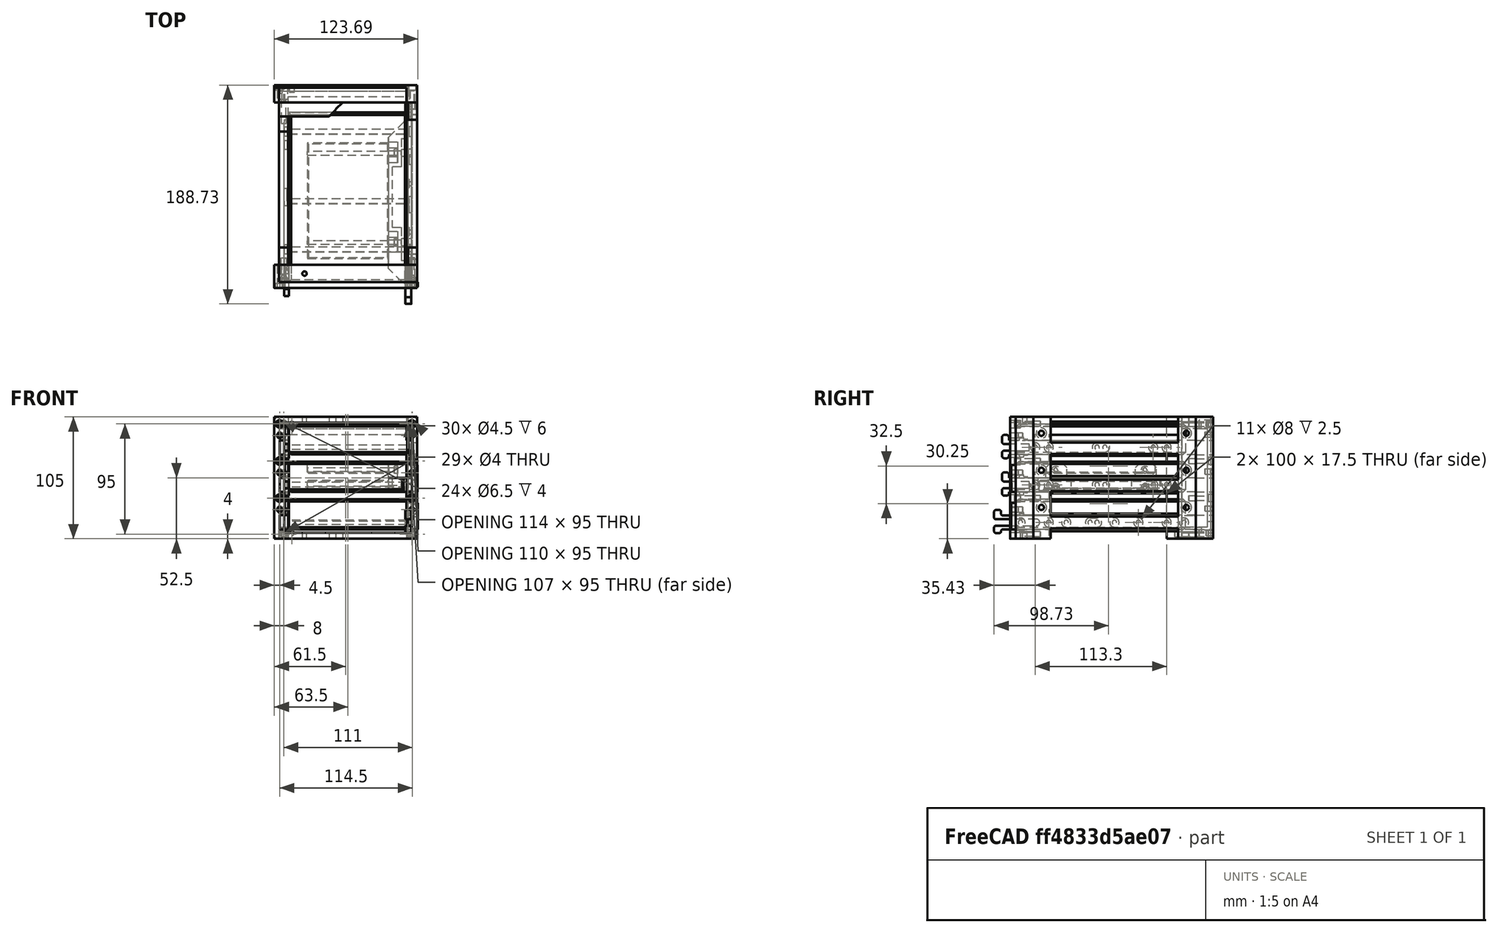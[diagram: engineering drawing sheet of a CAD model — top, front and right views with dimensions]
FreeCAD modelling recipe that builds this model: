
FCSTD DOCUMENT  (FreeCAD 1.0R39109 (Git))
Label: HDDEnclosure
License: All rights reserved
LicenseURL: http://en.wikipedia.org/wiki/All_rights_reserved
objects: Sketcher::SketchObject×66, PartDesign::Pocket×42, PartDesign::Pad×25, PartDesign::Body×19, PartDesign::Fillet×16, PartDesign::Chamfer×11, PartDesign::Hole×10, App::DocumentObjectGroup×3, Part::Mirroring×2, Mesh::Feature×1
note: 465 computed .brp shape members not serialized (recipe doc carries the construction recipe); baked Part::Feature solids carry a one-line shape summary decoded from their .brp

FEATURE [Mesh::Feature] HDD__Sled_Mk3
FEATURE [Sketcher::SketchObject] Sketch
  ArcFitTolerance = 1e-06
  AttachmentSupport = -> [XZ_Plane]
  FullyConstrained = false
  MakeInternals = false
  MapMode = 5
  Placement = pos=(0,0,0) rot=(1,0,0;1.5708rad)
  sketch-geometry (28):
    g0: LineSegment StartX=4 StartY=0 StartZ=0 EndX=-144.5 EndY=0 EndZ=0
    g1: LineSegment StartX=-144.5 StartY=0 StartZ=0 EndX=-144.5 EndY=-1.6 EndZ=0
    g2: LineSegment StartX=-144.5 StartY=-1.6 StartZ=0 EndX=-147.5 EndY=-1.6 EndZ=0
    g3: LineSegment StartX=-147.5 StartY=-1.6 StartZ=0 EndX=-147.5 EndY=0 EndZ=0
    g4: LineSegment StartX=-147.5 StartY=0 StartZ=0 EndX=-163.728 EndY=0 EndZ=0
    g5: LineSegment StartX=-163.728 StartY=0 StartZ=0 EndX=-163.728 EndY=-3.09041 EndZ=0
    g6: LineSegment StartX=-163.728 StartY=-3.09041 StartZ=0 EndX=-169.728 EndY=-3.09041 EndZ=0
    g7: LineSegment StartX=-169.728 StartY=-3.09041 StartZ=0 EndX=-169.728 EndY=3.2 EndZ=0
    g8: LineSegment StartX=-169.728 StartY=3.2 StartZ=0 EndX=-130.5 EndY=3.2 EndZ=0
    g9: LineSegment StartX=-130.5 StartY=3.2 StartZ=0 EndX=-130.5 EndY=8.8 EndZ=0
    g10: LineSegment StartX=-130.5 StartY=8.8 StartZ=0 EndX=-169.728 EndY=8.8 EndZ=0
    g11: LineSegment StartX=-169.728 StartY=8.8 StartZ=0 EndX=-169.728 EndY=16.6996 EndZ=0
    g12: LineSegment StartX=-169.728 StartY=16.6996 StartZ=0 EndX=-163.728 EndY=16.6996 EndZ=0
    g13: LineSegment StartX=-163.728 StartY=16.6996 StartZ=0 EndX=-163.728 EndY=12 EndZ=0
    g14: LineSegment StartX=-163.728 StartY=12 StartZ=0 EndX=-147.5 EndY=12 EndZ=0
    g15: LineSegment StartX=-147.5 StartY=12 StartZ=0 EndX=-147.5 EndY=13.6 EndZ=0
    g16: LineSegment StartX=-147.5 StartY=13.6 StartZ=0 EndX=-144.5 EndY=13.6 EndZ=0
    g17: LineSegment StartX=-144.5 StartY=13.6 StartZ=0 EndX=-144.5 EndY=12 EndZ=0
    g18: LineSegment StartX=-144.5 StartY=12 StartZ=0 EndX=4 EndY=12 EndZ=0
    g19: LineSegment StartX=4 StartY=12 StartZ=0 EndX=4 EndY=0 EndZ=0
    g20: LineSegment [constr] StartX=-177.942 StartY=12 StartZ=0 EndX=14.5003 EndY=12 EndZ=0
    g21: LineSegment [constr] StartX=-144.5 StartY=27.4193 StartZ=0 EndX=-144.5 EndY=-18.7719 EndZ=0
    g22: LineSegment [constr] StartX=-163.728 StartY=22.481 StartZ=0 EndX=-163.728 EndY=-16.4674 EndZ=0
    g23: LineSegment [constr] StartX=-169.728 StartY=19.6726 StartZ=0 EndX=-169.728 EndY=-22.0842 EndZ=0
    g24: Circle CenterX=-66 CenterY=6 CenterZ=0 NormalX=0 NormalY=0 NormalZ=1 AngleXU=0 Radius=1.9
    g25: Circle CenterX=-6 CenterY=6 CenterZ=0 NormalX=0 NormalY=0 NormalZ=1 AngleXU=0 Radius=1.9
    g26: LineSegment [constr] StartX=-174.191 StartY=6 StartZ=0 EndX=-2.85094 EndY=6 EndZ=0
    g27: Circle CenterX=-107.6 CenterY=6 CenterZ=0 NormalX=0 NormalY=0 NormalZ=1 AngleXU=0 Radius=1.9
  constraints (76):
    c: PointOnObject(g0,g-1)
    c: Coincident(g0,g1)
    c: Coincident(g1,g2)
    c: Coincident(g2,g3)
    c: PointOnObject(g3,g-1)
    c: Coincident(g3,g4)
    c: Horizontal(g4)
    c: Coincident(g4,g5)
    c: Coincident(g5,g6)
    c: Coincident(g6,g7)
    c: Coincident(g7,g8)
    c: Horizontal(g8)
    c: Coincident(g8,g9)
    c: Coincident(g9,g10)
    c: Horizontal(g10)
    c: Coincident(g10,g11)
    c: Coincident(g11,g12)
    c: Coincident(g12,g13)
    c: Coincident(g13,g14)
    c: Horizontal(g14)
    c: Coincident(g14,g15)
    c: Coincident(g15,g16)
    c: Horizontal(g16)
    c: Coincident(g16,g17)
    c: Coincident(g17,g18)
    c: Horizontal(g18)
    c: Coincident(g18,g19)
    c: Coincident(g19,g0)
    c: Vertical(g7)
    c: Vertical(g11)
    c: Horizontal(g12)
    c: Horizontal(g6)
    c: Horizontal(g20)
    c: PointOnObject(g17,g20)
    c: PointOnObject(g14,g20)
    c: DistanceY(g0,g20) = 12
    c: Vertical(g15)
    c: Vertical(g17)
    c: Vertical(g1)
    c: Vertical(g3)
    c: Horizontal(g2)
    c: Vertical(g21)
    c: PointOnObject(g0,g21)
    c: PointOnObject(g17,g21)
    c: DistanceX(g16,g16) = 3
    c: DistanceY(g15,g15) = 1.6
    c: DistanceX(g2,g2) = 3
    c: DistanceY(g3,g3) = 1.6
    c: Vertical(g13)
    c: Vertical(g5)
    c: Vertical(g22)
    c: Vertical(g23)
    c: PointOnObject(g7,g23)
    c: PointOnObject(g10,g23)
    c: PointOnObject(g13,g22)
    c: PointOnObject(g4,g22)
    c: DistanceX(g12,g12) = 6
    c: Vertical(g9)
    c: Distance(g8,g-1) = 3.2
    c: Distance(g9,g20) = 3.2
    c: Diameter(g24) = 3.8
    c: Diameter(g25) = 3.8
    c: Horizontal(g26)
    c: PointOnObject(g24,g26)
    c: PointOnObject(g25,g26)
    c: DistanceY(g0,g26) = 6
    c: DistanceX(g24,g25) = 60
    c: PointOnObject(g27,g26)
    c: Diameter(g27) = 3.8
    c: DistanceX(g27,g25) = 101.6
    c: DistanceX(g25,g0) = 10
    c: Horizontal(g0)
    c: Vertical(g19)
    c: Distance(g-1,g0) = 4
    c: DistanceX(g16,g9) = 14
    c: DistanceX(g9,g18) = 134.5
FEATURE [PartDesign::Pad] Pad
  Direction = (0,-1,2e-16)
  Length = 5
  Length2 = 6
  Placement = pos=(0,0,0) rot=(1,0,0;1.5708rad)
  Profile = -> Sketch
  ReferenceAxis = -> Sketch [N_Axis]
  Suppressed = false
  Type = 0
FEATURE [Sketcher::SketchObject] Sketch001
  ArcFitTolerance = 1e-06
  AttachmentSupport = -> [Pad]
  FullyConstrained = false
  MakeInternals = false
  MapMode = 5
  Placement = pos=(0,1.4e-15,0) rot=(-1,0,0;1.5708rad)
  sketch-geometry (4):
    g0: LineSegment [constr] StartX=-161.489 StartY=-6 StartZ=0 EndX=29.2517 EndY=-6 EndZ=0
    g1: Circle CenterX=-107.6 CenterY=-6 CenterZ=0 NormalX=0 NormalY=0 NormalZ=1 AngleXU=0 Radius=4
    g2: Circle CenterX=-66 CenterY=-6 CenterZ=0 NormalX=0 NormalY=0 NormalZ=1 AngleXU=0 Radius=4
    g3: Circle CenterX=-6 CenterY=-6 CenterZ=0 NormalX=0 NormalY=0 NormalZ=1 AngleXU=0 Radius=4
  constraints (11):
    c: Horizontal(g0)
    c: Distance(g-1,g0) = 6
    c: PointOnObject(g1,g0)
    c: PointOnObject(g2,g0)
    c: PointOnObject(g3,g0)
    c: DistanceX(g3,g-1) = 6
    c: DistanceX(g2,g3) = 60
    c: DistanceX(g1,g3) = 101.6
    c: Diameter(g1) = 8
    c: Equal(g2,g1)
    c: Equal(g3,g1)
FEATURE [PartDesign::Pocket] Pocket
  BaseFeature = -> Pad
  Direction = (0,-1,-2e-16)
  Length = 3
  Length2 = 5
  Placement = pos=(0,0,0) rot=(1,0,0;1.5708rad)
  Profile = -> Sketch001
  ReferenceAxis = -> Sketch001 [N_Axis]
  Suppressed = false
  Type = 0
FEATURE [PartDesign::Fillet] Fillet
  Base = -> Pocket [Edge5,Edge1]
  BaseFeature = -> Pocket
  Placement = pos=(0,0,0) rot=(1,0,0;1.5708rad)
  Radius = 2
  SupportTransform = false
  Suppressed = false
  UseAllEdges = false
FEATURE [PartDesign::Fillet] Fillet001
  Base = -> Fillet [Edge65,Edge63,Edge61,Edge59,Edge31,Edge58,Edge56,Edge3]
  BaseFeature = -> Fillet
  Placement = pos=(0,0,0) rot=(1,0,0;1.5708rad)
  Radius = 0.75
  SupportTransform = false
  Suppressed = false
  UseAllEdges = false
FEATURE [PartDesign::Fillet] Fillet002
  Base = -> Fillet001 [Edge83,Edge85,Edge87,Edge89,Edge96,Edge94,Edge92,Edge95]
  BaseFeature = -> Fillet001
  Placement = pos=(0,0,0) rot=(1,0,0;1.5708rad)
  Radius = 1.49
  SupportTransform = false
  Suppressed = false
  UseAllEdges = false
FEATURE [Sketcher::SketchObject] Sketch002
  ArcFitTolerance = 1e-06
  AttachmentSupport = -> [XZ_Plane001]
  FullyConstrained = false
  MakeInternals = false
  MapMode = 5
  Placement = pos=(0,0,0) rot=(1,0,0;1.5708rad)
  sketch-geometry (73):
    g0: LineSegment [constr] StartX=0 StartY=0 StartZ=0 EndX=123 EndY=0 EndZ=0
    g1: LineSegment StartX=123 StartY=0 StartZ=0 EndX=123 EndY=105 EndZ=0
    g2: LineSegment StartX=123 StartY=105 StartZ=0 EndX=0 EndY=105 EndZ=0
    g3: LineSegment StartX=9 StartY=5 StartZ=0 EndX=114 EndY=5 EndZ=0
    g4: LineSegment StartX=114 StartY=100 StartZ=0 EndX=9 EndY=100 EndZ=0
    g5: LineSegment [constr] StartX=190.257 StartY=65.8 StartZ=0 EndX=190.257 EndY=40.4 EndZ=0
    g6: LineSegment [constr] StartX=190.257 StartY=40.4 StartZ=0 EndX=291.857 EndY=40.4 EndZ=0
    g7: LineSegment [constr] StartX=291.857 StartY=40.4 StartZ=0 EndX=291.857 EndY=65.8 EndZ=0
    g8: LineSegment [constr] StartX=291.857 StartY=65.8 StartZ=0 EndX=190.257 EndY=65.8 EndZ=0
    g9: LineSegment [constr] StartX=184.257 StartY=52.4 StartZ=0 EndX=184.257 EndY=40.4 EndZ=0
    g10: LineSegment [constr] StartX=184.257 StartY=40.4 StartZ=0 EndX=190.257 EndY=40.4 EndZ=0
    g11: LineSegment [constr] StartX=190.257 StartY=40.4 StartZ=0 EndX=190.257 EndY=52.4 EndZ=0
    g12: LineSegment [constr] StartX=190.257 StartY=52.4 StartZ=0 EndX=184.257 EndY=52.4 EndZ=0
    g13: LineSegment [constr] StartX=291.857 StartY=52.4 StartZ=0 EndX=291.857 EndY=40.4 EndZ=0
    g14: LineSegment [constr] StartX=291.857 StartY=40.4 StartZ=0 EndX=297.857 EndY=40.4 EndZ=0
    g15: LineSegment [constr] StartX=297.857 StartY=40.4 StartZ=0 EndX=297.857 EndY=52.4 EndZ=0
    g16: LineSegment [constr] StartX=297.857 StartY=52.4 StartZ=0 EndX=291.857 EndY=52.4 EndZ=0
    g17: LineSegment [constr] StartX=163.474 StartY=98.2 StartZ=0 EndX=163.474 EndY=72.8 EndZ=0
    g18: LineSegment [constr] StartX=163.474 StartY=72.8 StartZ=0 EndX=265.074 EndY=72.8 EndZ=0
    g19: LineSegment [constr] StartX=265.074 StartY=72.8 StartZ=0 EndX=265.074 EndY=98.2 EndZ=0
    g20: LineSegment [constr] StartX=265.074 StartY=98.2 StartZ=0 EndX=163.474 EndY=98.2 EndZ=0
    g21: LineSegment [constr] StartX=157.474 StartY=84.8 StartZ=0 EndX=157.474 EndY=72.8 EndZ=0
    g22: LineSegment [constr] StartX=157.474 StartY=72.8 StartZ=0 EndX=163.474 EndY=72.8 EndZ=0
    g23: LineSegment [constr] StartX=163.474 StartY=72.8 StartZ=0 EndX=163.474 EndY=84.8 EndZ=0
    g24: LineSegment [constr] StartX=163.474 StartY=84.8 StartZ=0 EndX=157.474 EndY=84.8 EndZ=0
    g25: LineSegment [constr] StartX=265.074 StartY=84.8 StartZ=0 EndX=265.074 EndY=72.8 EndZ=0
    g26: LineSegment [constr] StartX=265.074 StartY=72.8 StartZ=0 EndX=271.074 EndY=72.8 EndZ=0
    g27: LineSegment [constr] StartX=271.074 StartY=72.8 StartZ=0 EndX=271.074 EndY=84.8 EndZ=0
    g28: LineSegment [constr] StartX=271.074 StartY=84.8 StartZ=0 EndX=265.074 EndY=84.8 EndZ=0
    g29: LineSegment [constr] StartX=208.539 StartY=33.4 StartZ=0 EndX=208.539 EndY=8 EndZ=0
    g30: LineSegment [constr] StartX=208.539 StartY=8 StartZ=0 EndX=310.139 EndY=8 EndZ=0
    g31: LineSegment [constr] StartX=310.139 StartY=8 StartZ=0 EndX=310.139 EndY=33.4 EndZ=0
    g32: LineSegment [constr] StartX=310.139 StartY=33.4 StartZ=0 EndX=208.539 EndY=33.4 EndZ=0
    g33: LineSegment [constr] StartX=202.539 StartY=20 StartZ=0 EndX=202.539 EndY=8 EndZ=0
    g34: LineSegment [constr] StartX=202.539 StartY=8 StartZ=0 EndX=208.539 EndY=8 EndZ=0
    g35: LineSegment [constr] StartX=208.539 StartY=8 StartZ=0 EndX=208.539 EndY=20 EndZ=0
    g36: LineSegment [constr] StartX=208.539 StartY=20 StartZ=0 EndX=202.539 EndY=20 EndZ=0
    g37: LineSegment [constr] StartX=310.139 StartY=20 StartZ=0 EndX=310.139 EndY=8 EndZ=0
    g38: LineSegment [constr] StartX=310.139 StartY=8 StartZ=0 EndX=316.139 EndY=8 EndZ=0
    g39: LineSegment [constr] StartX=316.139 StartY=8 StartZ=0 EndX=316.139 EndY=20 EndZ=0
    g40: LineSegment [constr] StartX=316.139 StartY=20 StartZ=0 EndX=310.139 EndY=20 EndZ=0
    g41: LineSegment StartX=0 StartY=0 StartZ=0 EndX=123 EndY=0 EndZ=0
    g42: LineSegment [constr] StartX=9 StartY=177.265 StartZ=0 EndX=9 EndY=-72.0652 EndZ=0
    g43: LineSegment [constr] StartX=114 StartY=141.11 StartZ=0 EndX=114 EndY=26.7674 EndZ=0
    g44: LineSegment StartX=9 StartY=100 StartZ=0 EndX=9 EndY=84.9 EndZ=0
    g45: LineSegment StartX=9 StartY=84.9 StartZ=0 EndX=4.5 EndY=84.9 EndZ=0
    g46: LineSegment StartX=4.5 StartY=84.9 StartZ=0 EndX=4.5 EndY=72.6 EndZ=0
    g47: LineSegment StartX=4.5 StartY=72.6 StartZ=0 EndX=9 EndY=72.6 EndZ=0
    g48: LineSegment StartX=9 StartY=72.6 StartZ=0 EndX=9 EndY=52.6 EndZ=0
    g49: LineSegment StartX=9 StartY=52.6 StartZ=0 EndX=4.5 EndY=52.6 EndZ=0
    g50: LineSegment StartX=4.5 StartY=52.6 StartZ=0 EndX=4.5 EndY=40.3 EndZ=0
    g51: LineSegment StartX=4.5 StartY=40.3 StartZ=0 EndX=9 EndY=40.3 EndZ=0
    g52: LineSegment StartX=9 StartY=40.3 StartZ=0 EndX=9 EndY=20.3 EndZ=0
    g53: LineSegment StartX=9 StartY=20.3 StartZ=0 EndX=4.5 EndY=20.3 EndZ=0
    g54: LineSegment StartX=4.5 StartY=20.3 StartZ=0 EndX=4.5 EndY=8 EndZ=0
    g55: LineSegment StartX=4.5 StartY=8 StartZ=0 EndX=9 EndY=8 EndZ=0
    g56: LineSegment StartX=9 StartY=8 StartZ=0 EndX=9 EndY=5 EndZ=0
    g57: LineSegment [constr] StartX=4.5 StartY=110.102 StartZ=0 EndX=4.5 EndY=-9.82312 EndZ=0
    g58: LineSegment StartX=114 StartY=100 StartZ=0 EndX=114 EndY=84.9 EndZ=0
    g59: LineSegment StartX=114 StartY=84.9 StartZ=0 EndX=118.5 EndY=84.9 EndZ=0
    g60: LineSegment StartX=118.5 StartY=84.9 StartZ=0 EndX=118.5 EndY=72.6 EndZ=0
    g61: LineSegment StartX=118.5 StartY=72.6 StartZ=0 EndX=114 EndY=72.6 EndZ=0
    g62: LineSegment StartX=114 StartY=72.6 StartZ=0 EndX=114 EndY=52.6 EndZ=0
    g63: LineSegment StartX=114 StartY=52.6 StartZ=0 EndX=118.5 EndY=52.6 EndZ=0
    g64: LineSegment StartX=118.5 StartY=52.6 StartZ=0 EndX=118.5 EndY=40.3 EndZ=0
    g65: LineSegment StartX=118.5 StartY=40.3 StartZ=0 EndX=114 EndY=40.3 EndZ=0
    g66: LineSegment StartX=114 StartY=40.3 StartZ=0 EndX=114 EndY=20.3 EndZ=0
    g67: LineSegment StartX=114 StartY=20.3 StartZ=0 EndX=118.5 EndY=20.3 EndZ=0
    g68: LineSegment StartX=118.5 StartY=20.3 StartZ=0 EndX=118.5 EndY=8 EndZ=0
    g69: LineSegment StartX=118.5 StartY=8 StartZ=0 EndX=114 EndY=8 EndZ=0
    g70: LineSegment StartX=114 StartY=8 StartZ=0 EndX=114 EndY=5 EndZ=0
    g71: LineSegment [constr] StartX=118.5 StartY=109.281 StartZ=0 EndX=118.5 EndY=-16.6316 EndZ=0
    g72: LineSegment StartX=0 StartY=105 StartZ=0 EndX=0 EndY=0 EndZ=0
  constraints (212):
    c: Coincident(g-1,g0)
    c: Horizontal(g0)
    c: Coincident(g0,g1)
    c: Vertical(g1)
    c: Coincident(g1,g2)
    c: PointOnObject(g2,g-2)
    c: Horizontal(g2)
    c: Horizontal(g3)
    c: Horizontal(g4)
    c: Coincident(g5,g6)
    c: Coincident(g6,g7)
    c: Coincident(g7,g8)
    c: Coincident(g8,g5)
    c: Vertical(g5)
    c: Vertical(g7)
    c: Horizontal(g6)
    c: Horizontal(g8)
    c: DistanceX(g8,g8) = 101.6
    c: DistanceY(g7,g7) = 25.4
    c: Coincident(g9,g10)
    c: Coincident(g10,g11)
    c: Coincident(g11,g12)
    c: Coincident(g12,g9)
    c: Vertical(g9)
    c: Vertical(g11)
    c: Horizontal(g10)
    c: Horizontal(g12)
    c: DistanceX(g12,g12) = 6
    c: DistanceY(g11,g11) = 12
    c: PointOnObject(g11,g5)
    c: Coincident(g13,g14)
    c: Coincident(g14,g15)
    c: Coincident(g15,g16)
    c: Coincident(g16,g13)
    c: Vertical(g13)
    c: Vertical(g15)
    c: Horizontal(g14)
    c: Horizontal(g16)
    c: DistanceX(g16,g16) = 6
    c: DistanceY(g15,g15) = 12
    c: PointOnObject(g13,g7)
    c: DistanceY(g5,g10) = 0
    c: DistanceY(g6,g13) = 0
    c: DistanceX(g3,g3) = 105
    c: Coincident(g17,g18)
    c: Coincident(g18,g19)
    c: Coincident(g19,g20)
    c: Coincident(g20,g17)
    c: Vertical(g17)
    c: Vertical(g19)
    c: Horizontal(g18)
    c: Horizontal(g20)
    c: DistanceX(g20,g20) = 101.6
    c: DistanceY(g19,g19) = 25.4
    c: Coincident(g21,g22)
    c: Coincident(g22,g23)
    c: Coincident(g23,g24)
    c: Coincident(g24,g21)
    c: Vertical(g21)
    c: Vertical(g23)
    c: Horizontal(g22)
    c: Horizontal(g24)
    c: DistanceX(g24,g24) = 6
    c: DistanceY(g23,g23) = 12
    c: PointOnObject(g23,g17)
    c: Coincident(g25,g26)
    c: Coincident(g26,g27)
    c: Coincident(g27,g28)
    c: Coincident(g28,g25)
    c: Vertical(g25)
    c: Vertical(g27)
    c: Horizontal(g26)
    c: Horizontal(g28)
    c: DistanceX(g28,g28) = 6
    c: DistanceY(g27,g27) = 12
    c: PointOnObject(g25,g19)
    c: DistanceY(g17,g22) = 0
    c: DistanceY(g18,g25) = 0
    c: Coincident(g29,g30)
    c: Coincident(g30,g31)
    c: Coincident(g31,g32)
    c: Coincident(g32,g29)
    c: Vertical(g29)
    c: Vertical(g31)
    c: Horizontal(g30)
    c: Horizontal(g32)
    c: DistanceX(g32,g32) = 101.6
    c: DistanceY(g31,g31) = 25.4
    c: Coincident(g33,g34)
    c: Coincident(g34,g35)
    c: Coincident(g35,g36)
    c: Coincident(g36,g33)
    c: Vertical(g33)
    c: Vertical(g35)
    c: Horizontal(g34)
    c: Horizontal(g36)
    c: DistanceX(g36,g36) = 6
    c: DistanceY(g35,g35) = 12
    c: PointOnObject(g35,g29)
    c: Coincident(g37,g38)
    c: Coincident(g38,g39)
    c: Coincident(g39,g40)
    c: Coincident(g40,g37)
    c: Vertical(g37)
    c: Vertical(g39)
    c: Horizontal(g38)
    c: Horizontal(g40)
    c: DistanceX(g40,g40) = 6
    c: DistanceY(g39,g39) = 12
    c: PointOnObject(g37,g31)
    c: DistanceY(g29,g34) = 0
    c: DistanceY(g30,g37) = 0
    c: DistanceY(g0,g29) = 8
    c: Distance(g32,g6) = 7
    c: Distance(g8,g18) = 7
    c: DistanceX(g0,g0) = 123
    c: Coincident(g41,g0)
    c: Coincident(g41,g0)
    c: Vertical(g43)
    c: Distance(g0,g43) = 9
    c: DistanceX(g0,g42) = 9
    c: PointOnObject(g3,g42)
    c: PointOnObject(g4,g42)
    c: PointOnObject(g3,g43)
    c: PointOnObject(g4,g43)
    c: Coincident(g4,g44)
    c: PointOnObject(g44,g42)
    c: Coincident(g44,g45)
    c: Horizontal(g45)
    c: Coincident(g45,g46)
    c: Vertical(g46)
    c: Coincident(g46,g47)
    c: PointOnObject(g47,g42)
    c: Horizontal(g47)
    c: Coincident(g47,g48)
    c: Symmetric(g42,g42,g48)
    c: Coincident(g48,g49)
    c: Horizontal(g49)
    c: Coincident(g49,g50)
    c: Vertical(g50)
    c: Coincident(g50,g51)
    c: Horizontal(g51)
    c: Coincident(g51,g52)
    c: Coincident(g52,g53)
    c: Coincident(g53,g54)
    c: Coincident(g54,g55)
    c: PointOnObject(g55,g42)
    c: Horizontal(g55)
    c: Coincident(g55,g56)
    c: Coincident(g56,g3)
    c: PointOnObject(g51,g42)
    c: Vertical(g52)
    c: Vertical(g54)
    c: Vertical(g57)
    c: PointOnObject(g45,g57)
    c: PointOnObject(g49,g57)
    c: PointOnObject(g53,g57)
    c: DistanceY(g50,g50) = 12.3
    c: DistanceY(g46,g46) = 12.3
    c: DistanceY(g54,g54) = 12.3
    c: Horizontal(g53)
    c: Vertical(g42)
    c: DistanceX(g57,g42) = 4.5
    c: DistanceY(g56,g56) = 3
    c: DistanceY(g52,g52) = 20
    c: DistanceY(g48,g48) = 20
    c: Coincident(g4,g58)
    c: Vertical(g58)
    c: Coincident(g58,g59)
    c: Horizontal(g59)
    c: Coincident(g59,g60)
    c: Coincident(g60,g61)
    c: Coincident(g61,g62)
    c: Coincident(g62,g63)
    c: Horizontal(g63)
    c: Coincident(g63,g64)
    c: Vertical(g64)
    c: Coincident(g64,g65)
    c: Horizontal(g65)
    c: Coincident(g65,g66)
    c: Vertical(g66)
    c: Coincident(g66,g67)
    c: Horizontal(g67)
    c: Coincident(g67,g68)
    c: Vertical(g68)
    c: Coincident(g68,g69)
    c: Horizontal(g69)
    c: Coincident(g69,g70)
    c: Coincident(g70,g3)
    c: PointOnObject(g62,g43)
    c: Vertical(g62)
    c: PointOnObject(g65,g43)
    c: Vertical(g60)
    c: Horizontal(g61)
    c: Vertical(g71)
    c: PointOnObject(g60,g71)
    c: PointOnObject(g64,g71)
    c: Vertical(g70)
    c: PointOnObject(g67,g71)
    c: DistanceY(g64,g64) = 12.3
    c: DistanceY(g60,g60) = 12.3
    c: DistanceY(g68,g68) = 12.3
    c: DistanceY(g66,g66) = 20
    c: DistanceY(g62,g62) = 20
    c: DistanceX(g43,g71) = 4.5
    c: Coincident(g2,g72)
    c: Coincident(g72,g0)
    c: DistanceY(g4,g1) = 5
    c: DistanceY(g17,g4) = 1.8
    c: DistanceY(g0,g3) = 5
    c: DistanceY(g3,g69) = 3
    c: DistanceY(g72,g72) = 105
FEATURE [PartDesign::Pad] Pad001
  Direction = (0,-1,2e-16)
  Length = 20
  Length2 = 10
  Placement = pos=(0,0,0) rot=(1,0,0;1.5708rad)
  Profile = -> Sketch002
  ReferenceAxis = -> Sketch002 [N_Axis]
  Suppressed = false
  Type = 0
FEATURE [PartDesign::Fillet] Fillet003
  Base = -> Fillet002 [Edge77,Edge73]
  BaseFeature = -> Fillet002
  Placement = pos=(0,0,0) rot=(1,0,0;1.5708rad)
  Radius = 2.5
  SupportTransform = false
  Suppressed = false
  UseAllEdges = false
FEATURE [PartDesign::Body] Body  label="sideFix"
  AllowCompound = false
  Group = -> [Sketch,Pad,Sketch001,Pocket,Fillet,Fillet001,Fillet002,Fillet003]
  Origin = -> Origin
  Placement = pos=(113,136,8) rot=(0,0,-1;4.71239rad)
  Tip = -> Fillet003
FEATURE [Sketcher::SketchObject] Sketch004
  ArcFitTolerance = 1e-06
  AttachmentSupport = -> [XZ_Plane002]
  FullyConstrained = false
  MakeInternals = false
  MapMode = 5
  Placement = pos=(0,0,0) rot=(1,0,0;1.5708rad)
  sketch-geometry (73):
    g0: LineSegment [constr] StartX=0 StartY=0 StartZ=0 EndX=123 EndY=0 EndZ=0
    g1: LineSegment StartX=123 StartY=0 StartZ=0 EndX=123 EndY=105 EndZ=0
    g2: LineSegment StartX=123 StartY=105 StartZ=0 EndX=0 EndY=105 EndZ=0
    g3: LineSegment StartX=9 StartY=5 StartZ=0 EndX=114 EndY=5 EndZ=0
    g4: LineSegment StartX=114 StartY=100 StartZ=0 EndX=9 EndY=100 EndZ=0
    g5: LineSegment [constr] StartX=190.257 StartY=65.8 StartZ=0 EndX=190.257 EndY=40.4 EndZ=0
    g6: LineSegment [constr] StartX=190.257 StartY=40.4 StartZ=0 EndX=291.857 EndY=40.4 EndZ=0
    g7: LineSegment [constr] StartX=291.857 StartY=40.4 StartZ=0 EndX=291.857 EndY=65.8 EndZ=0
    g8: LineSegment [constr] StartX=291.857 StartY=65.8 StartZ=0 EndX=190.257 EndY=65.8 EndZ=0
    g9: LineSegment [constr] StartX=184.257 StartY=52.4 StartZ=0 EndX=184.257 EndY=40.4 EndZ=0
    g10: LineSegment [constr] StartX=184.257 StartY=40.4 StartZ=0 EndX=190.257 EndY=40.4 EndZ=0
    g11: LineSegment [constr] StartX=190.257 StartY=40.4 StartZ=0 EndX=190.257 EndY=52.4 EndZ=0
    g12: LineSegment [constr] StartX=190.257 StartY=52.4 StartZ=0 EndX=184.257 EndY=52.4 EndZ=0
    g13: LineSegment [constr] StartX=291.857 StartY=52.4 StartZ=0 EndX=291.857 EndY=40.4 EndZ=0
    g14: LineSegment [constr] StartX=291.857 StartY=40.4 StartZ=0 EndX=297.857 EndY=40.4 EndZ=0
    g15: LineSegment [constr] StartX=297.857 StartY=40.4 StartZ=0 EndX=297.857 EndY=52.4 EndZ=0
    g16: LineSegment [constr] StartX=297.857 StartY=52.4 StartZ=0 EndX=291.857 EndY=52.4 EndZ=0
    g17: LineSegment [constr] StartX=163.474 StartY=98.2 StartZ=0 EndX=163.474 EndY=72.8 EndZ=0
    g18: LineSegment [constr] StartX=163.474 StartY=72.8 StartZ=0 EndX=265.074 EndY=72.8 EndZ=0
    g19: LineSegment [constr] StartX=265.074 StartY=72.8 StartZ=0 EndX=265.074 EndY=98.2 EndZ=0
    g20: LineSegment [constr] StartX=265.074 StartY=98.2 StartZ=0 EndX=163.474 EndY=98.2 EndZ=0
    g21: LineSegment [constr] StartX=157.474 StartY=84.8 StartZ=0 EndX=157.474 EndY=72.8 EndZ=0
    g22: LineSegment [constr] StartX=157.474 StartY=72.8 StartZ=0 EndX=163.474 EndY=72.8 EndZ=0
    g23: LineSegment [constr] StartX=163.474 StartY=72.8 StartZ=0 EndX=163.474 EndY=84.8 EndZ=0
    g24: LineSegment [constr] StartX=163.474 StartY=84.8 StartZ=0 EndX=157.474 EndY=84.8 EndZ=0
    g25: LineSegment [constr] StartX=265.074 StartY=84.8 StartZ=0 EndX=265.074 EndY=72.8 EndZ=0
    g26: LineSegment [constr] StartX=265.074 StartY=72.8 StartZ=0 EndX=271.074 EndY=72.8 EndZ=0
    g27: LineSegment [constr] StartX=271.074 StartY=72.8 StartZ=0 EndX=271.074 EndY=84.8 EndZ=0
    g28: LineSegment [constr] StartX=271.074 StartY=84.8 StartZ=0 EndX=265.074 EndY=84.8 EndZ=0
    g29: LineSegment [constr] StartX=208.539 StartY=33.4 StartZ=0 EndX=208.539 EndY=8 EndZ=0
    g30: LineSegment [constr] StartX=208.539 StartY=8 StartZ=0 EndX=310.139 EndY=8 EndZ=0
    g31: LineSegment [constr] StartX=310.139 StartY=8 StartZ=0 EndX=310.139 EndY=33.4 EndZ=0
    g32: LineSegment [constr] StartX=310.139 StartY=33.4 StartZ=0 EndX=208.539 EndY=33.4 EndZ=0
    g33: LineSegment [constr] StartX=202.539 StartY=20 StartZ=0 EndX=202.539 EndY=8 EndZ=0
    g34: LineSegment [constr] StartX=202.539 StartY=8 StartZ=0 EndX=208.539 EndY=8 EndZ=0
    g35: LineSegment [constr] StartX=208.539 StartY=8 StartZ=0 EndX=208.539 EndY=20 EndZ=0
    g36: LineSegment [constr] StartX=208.539 StartY=20 StartZ=0 EndX=202.539 EndY=20 EndZ=0
    g37: LineSegment [constr] StartX=310.139 StartY=20 StartZ=0 EndX=310.139 EndY=8 EndZ=0
    g38: LineSegment [constr] StartX=310.139 StartY=8 StartZ=0 EndX=316.139 EndY=8 EndZ=0
    g39: LineSegment [constr] StartX=316.139 StartY=8 StartZ=0 EndX=316.139 EndY=20 EndZ=0
    g40: LineSegment [constr] StartX=316.139 StartY=20 StartZ=0 EndX=310.139 EndY=20 EndZ=0
    g41: LineSegment StartX=0 StartY=0 StartZ=0 EndX=123 EndY=0 EndZ=0
    g42: LineSegment [constr] StartX=9 StartY=177.265 StartZ=0 EndX=9 EndY=-72.0652 EndZ=0
    g43: LineSegment [constr] StartX=114 StartY=141.11 StartZ=0 EndX=114 EndY=26.7674 EndZ=0
    g44: LineSegment StartX=9 StartY=100 StartZ=0 EndX=9 EndY=84.9 EndZ=0
    g45: LineSegment StartX=9 StartY=84.9 StartZ=0 EndX=4.5 EndY=84.9 EndZ=0
    g46: LineSegment StartX=4.5 StartY=84.9 StartZ=0 EndX=4.5 EndY=72.6 EndZ=0
    g47: LineSegment StartX=4.5 StartY=72.6 StartZ=0 EndX=9 EndY=72.6 EndZ=0
    g48: LineSegment StartX=9 StartY=72.6 StartZ=0 EndX=9 EndY=52.6 EndZ=0
    g49: LineSegment StartX=9 StartY=52.6 StartZ=0 EndX=4.5 EndY=52.6 EndZ=0
    g50: LineSegment StartX=4.5 StartY=52.6 StartZ=0 EndX=4.5 EndY=40.3 EndZ=0
    g51: LineSegment StartX=4.5 StartY=40.3 StartZ=0 EndX=9 EndY=40.3 EndZ=0
    g52: LineSegment StartX=9 StartY=40.3 StartZ=0 EndX=9 EndY=20.3 EndZ=0
    g53: LineSegment StartX=9 StartY=20.3 StartZ=0 EndX=4.5 EndY=20.3 EndZ=0
    g54: LineSegment StartX=4.5 StartY=20.3 StartZ=0 EndX=4.5 EndY=8 EndZ=0
    g55: LineSegment StartX=4.5 StartY=8 StartZ=0 EndX=9 EndY=8 EndZ=0
    g56: LineSegment StartX=9 StartY=8 StartZ=0 EndX=9 EndY=5 EndZ=0
    g57: LineSegment [constr] StartX=4.5 StartY=110.102 StartZ=0 EndX=4.5 EndY=-9.82312 EndZ=0
    g58: LineSegment StartX=114 StartY=100 StartZ=0 EndX=114 EndY=84.9 EndZ=0
    g59: LineSegment StartX=114 StartY=84.9 StartZ=0 EndX=118.5 EndY=84.9 EndZ=0
    g60: LineSegment StartX=118.5 StartY=84.9 StartZ=0 EndX=118.5 EndY=72.6 EndZ=0
    g61: LineSegment StartX=118.5 StartY=72.6 StartZ=0 EndX=114 EndY=72.6 EndZ=0
    g62: LineSegment StartX=114 StartY=72.6 StartZ=0 EndX=114 EndY=52.6 EndZ=0
    g63: LineSegment StartX=114 StartY=52.6 StartZ=0 EndX=118.5 EndY=52.6 EndZ=0
    g64: LineSegment StartX=118.5 StartY=52.6 StartZ=0 EndX=118.5 EndY=40.3 EndZ=0
    g65: LineSegment StartX=118.5 StartY=40.3 StartZ=0 EndX=114 EndY=40.3 EndZ=0
    g66: LineSegment StartX=114 StartY=40.3 StartZ=0 EndX=114 EndY=20.3 EndZ=0
    g67: LineSegment StartX=114 StartY=20.3 StartZ=0 EndX=118.5 EndY=20.3 EndZ=0
    g68: LineSegment StartX=118.5 StartY=20.3 StartZ=0 EndX=118.5 EndY=8 EndZ=0
    g69: LineSegment StartX=118.5 StartY=8 StartZ=0 EndX=114 EndY=8 EndZ=0
    g70: LineSegment StartX=114 StartY=8 StartZ=0 EndX=114 EndY=5 EndZ=0
    g71: LineSegment [constr] StartX=118.5 StartY=109.281 StartZ=0 EndX=118.5 EndY=-16.6316 EndZ=0
    g72: LineSegment StartX=0 StartY=105 StartZ=0 EndX=0 EndY=0 EndZ=0
  constraints (212):
    c: Coincident(g-1,g0)
    c: Horizontal(g0)
    c: Coincident(g0,g1)
    c: Vertical(g1)
    c: Coincident(g1,g2)
    c: PointOnObject(g2,g-2)
    c: Horizontal(g2)
    c: Horizontal(g3)
    c: Horizontal(g4)
    c: Coincident(g5,g6)
    c: Coincident(g6,g7)
    c: Coincident(g7,g8)
    c: Coincident(g8,g5)
    c: Vertical(g5)
    c: Vertical(g7)
    c: Horizontal(g6)
    c: Horizontal(g8)
    c: DistanceX(g8,g8) = 101.6
    c: DistanceY(g7,g7) = 25.4
    c: Coincident(g9,g10)
    c: Coincident(g10,g11)
    c: Coincident(g11,g12)
    c: Coincident(g12,g9)
    c: Vertical(g9)
    c: Vertical(g11)
    c: Horizontal(g10)
    c: Horizontal(g12)
    c: DistanceX(g12,g12) = 6
    c: DistanceY(g11,g11) = 12
    c: PointOnObject(g11,g5)
    c: Coincident(g13,g14)
    c: Coincident(g14,g15)
    c: Coincident(g15,g16)
    c: Coincident(g16,g13)
    c: Vertical(g13)
    c: Vertical(g15)
    c: Horizontal(g14)
    c: Horizontal(g16)
    c: DistanceX(g16,g16) = 6
    c: DistanceY(g15,g15) = 12
    c: PointOnObject(g13,g7)
    c: DistanceY(g5,g10) = 0
    c: DistanceY(g6,g13) = 0
    c: DistanceX(g3,g3) = 105
    c: Coincident(g17,g18)
    c: Coincident(g18,g19)
    c: Coincident(g19,g20)
    c: Coincident(g20,g17)
    c: Vertical(g17)
    c: Vertical(g19)
    c: Horizontal(g18)
    c: Horizontal(g20)
    c: DistanceX(g20,g20) = 101.6
    c: DistanceY(g19,g19) = 25.4
    c: Coincident(g21,g22)
    c: Coincident(g22,g23)
    c: Coincident(g23,g24)
    c: Coincident(g24,g21)
    c: Vertical(g21)
    c: Vertical(g23)
    c: Horizontal(g22)
    c: Horizontal(g24)
    c: DistanceX(g24,g24) = 6
    c: DistanceY(g23,g23) = 12
    c: PointOnObject(g23,g17)
    c: Coincident(g25,g26)
    c: Coincident(g26,g27)
    c: Coincident(g27,g28)
    c: Coincident(g28,g25)
    c: Vertical(g25)
    c: Vertical(g27)
    c: Horizontal(g26)
    c: Horizontal(g28)
    c: DistanceX(g28,g28) = 6
    c: DistanceY(g27,g27) = 12
    c: PointOnObject(g25,g19)
    c: DistanceY(g17,g22) = 0
    c: DistanceY(g18,g25) = 0
    c: Coincident(g29,g30)
    c: Coincident(g30,g31)
    c: Coincident(g31,g32)
    c: Coincident(g32,g29)
    c: Vertical(g29)
    c: Vertical(g31)
    c: Horizontal(g30)
    c: Horizontal(g32)
    c: DistanceX(g32,g32) = 101.6
    c: DistanceY(g31,g31) = 25.4
    c: Coincident(g33,g34)
    c: Coincident(g34,g35)
    c: Coincident(g35,g36)
    c: Coincident(g36,g33)
    c: Vertical(g33)
    c: Vertical(g35)
    c: Horizontal(g34)
    c: Horizontal(g36)
    c: DistanceX(g36,g36) = 6
    c: DistanceY(g35,g35) = 12
    c: PointOnObject(g35,g29)
    c: Coincident(g37,g38)
    c: Coincident(g38,g39)
    c: Coincident(g39,g40)
    c: Coincident(g40,g37)
    c: Vertical(g37)
    c: Vertical(g39)
    c: Horizontal(g38)
    c: Horizontal(g40)
    c: DistanceX(g40,g40) = 6
    c: DistanceY(g39,g39) = 12
    c: PointOnObject(g37,g31)
    c: DistanceY(g29,g34) = 0
    c: DistanceY(g30,g37) = 0
    c: DistanceY(g0,g29) = 8
    c: Distance(g32,g6) = 7
    c: Distance(g8,g18) = 7
    c: DistanceX(g0,g0) = 123
    c: Coincident(g41,g0)
    c: Coincident(g41,g0)
    c: Vertical(g43)
    c: Distance(g0,g43) = 9
    c: DistanceX(g0,g42) = 9
    c: PointOnObject(g3,g42)
    c: PointOnObject(g4,g42)
    c: PointOnObject(g3,g43)
    c: PointOnObject(g4,g43)
    c: Coincident(g4,g44)
    c: PointOnObject(g44,g42)
    c: Coincident(g44,g45)
    c: Horizontal(g45)
    c: Coincident(g45,g46)
    c: Vertical(g46)
    c: Coincident(g46,g47)
    c: PointOnObject(g47,g42)
    c: Horizontal(g47)
    c: Coincident(g47,g48)
    c: Symmetric(g42,g42,g48)
    c: Coincident(g48,g49)
    c: Horizontal(g49)
    c: Coincident(g49,g50)
    c: Vertical(g50)
    c: Coincident(g50,g51)
    c: Horizontal(g51)
    c: Coincident(g51,g52)
    c: Coincident(g52,g53)
    c: Coincident(g53,g54)
    c: Coincident(g54,g55)
    c: PointOnObject(g55,g42)
    c: Horizontal(g55)
    c: Coincident(g55,g56)
    c: Coincident(g56,g3)
    c: PointOnObject(g51,g42)
    c: Vertical(g52)
    c: Vertical(g54)
    c: Vertical(g57)
    c: PointOnObject(g45,g57)
    c: PointOnObject(g49,g57)
    c: PointOnObject(g53,g57)
    c: DistanceY(g50,g50) = 12.3
    c: DistanceY(g46,g46) = 12.3
    c: DistanceY(g54,g54) = 12.3
    c: Horizontal(g53)
    c: Vertical(g42)
    c: DistanceX(g57,g42) = 4.5
    c: DistanceY(g56,g56) = 3
    c: DistanceY(g52,g52) = 20
    c: DistanceY(g48,g48) = 20
    c: Coincident(g4,g58)
    c: Vertical(g58)
    c: Coincident(g58,g59)
    c: Horizontal(g59)
    c: Coincident(g59,g60)
    c: Coincident(g60,g61)
    c: Coincident(g61,g62)
    c: Coincident(g62,g63)
    c: Horizontal(g63)
    c: Coincident(g63,g64)
    c: Vertical(g64)
    c: Coincident(g64,g65)
    c: Horizontal(g65)
    c: Coincident(g65,g66)
    c: Vertical(g66)
    c: Coincident(g66,g67)
    c: Horizontal(g67)
    c: Coincident(g67,g68)
    c: Vertical(g68)
    c: Coincident(g68,g69)
    c: Horizontal(g69)
    c: Coincident(g69,g70)
    c: Coincident(g70,g3)
    c: PointOnObject(g62,g43)
    c: Vertical(g62)
    c: PointOnObject(g65,g43)
    c: Vertical(g60)
    c: Horizontal(g61)
    c: Vertical(g71)
    c: PointOnObject(g60,g71)
    c: PointOnObject(g64,g71)
    c: Vertical(g70)
    c: PointOnObject(g67,g71)
    c: DistanceY(g64,g64) = 12.3
    c: DistanceY(g60,g60) = 12.3
    c: DistanceY(g68,g68) = 12.3
    c: DistanceY(g66,g66) = 20
    c: DistanceY(g62,g62) = 20
    c: DistanceX(g43,g71) = 4.5
    c: Coincident(g2,g72)
    c: Coincident(g72,g0)
    c: DistanceY(g4,g1) = 5
    c: DistanceY(g17,g4) = 1.8
    c: DistanceY(g0,g3) = 5
    c: DistanceY(g3,g69) = 3
    c: DistanceY(g72,g72) = 105
FEATURE [PartDesign::Pad] Pad002
  Direction = (0,-1,2e-16)
  Length = 140
  Length2 = 10
  Placement = pos=(0,0,0) rot=(1,0,0;1.5708rad)
  Profile = -> Sketch004
  ReferenceAxis = -> Sketch004 [N_Axis]
  Suppressed = false
  Type = 0
FEATURE [Sketcher::SketchObject] Sketch005
  ArcFitTolerance = 1e-06
  AttachmentSupport = -> [Pad002]
  FullyConstrained = false
  MakeInternals = false
  MapMode = 5
  Placement = pos=(0,4.62e-14,105) rot=(0,0,1;3.14159rad)
  sketch-geometry (4):
    g0: LineSegment StartX=31.939 StartY=166.44 StartZ=0 EndX=-114 EndY=166.44 EndZ=0
    g1: LineSegment StartX=-114 StartY=166.44 StartZ=0 EndX=-114 EndY=-24.3217 EndZ=0
    g2: LineSegment StartX=-114 StartY=-24.3217 StartZ=0 EndX=31.939 EndY=-24.3217 EndZ=0
    g3: LineSegment StartX=31.939 StartY=-24.3217 StartZ=0 EndX=31.939 EndY=166.44 EndZ=0
  constraints (9):
    c: Coincident(g0,g1)
    c: Coincident(g1,g2)
    c: Coincident(g2,g3)
    c: Coincident(g3,g0)
    c: Horizontal(g0)
    c: Horizontal(g2)
    c: Vertical(g1)
    c: Vertical(g3)
    c: Distance(g-1,g1) = 114
FEATURE [PartDesign::Pocket] Pocket001
  BaseFeature = -> Pad002
  Direction = (0,0,-1)
  Length = 5
  Length2 = 5
  Placement = pos=(0,0,0) rot=(1,0,0;1.5708rad)
  Profile = -> Sketch005
  ReferenceAxis = -> Sketch005 [N_Axis]
  Suppressed = false
  Type = 1
FEATURE [Sketcher::SketchObject] Sketch006
  ArcFitTolerance = 1e-06
  AttachmentSupport = -> [Pocket001]
  FullyConstrained = false
  MakeInternals = false
  MapMode = 5
  Placement = pos=(114,0,0) rot=(0.707107,0,-0.707107;3.14159rad)
  sketch-geometry (19):
    g0: LineSegment StartX=-73 StartY=125 StartZ=0 EndX=-73 EndY=15 EndZ=0
    g1: LineSegment StartX=-73 StartY=15 StartZ=0 EndX=-51 EndY=15 EndZ=0
    g2: LineSegment StartX=-51 StartY=15 StartZ=0 EndX=-51 EndY=125 EndZ=0
    g3: LineSegment StartX=-51 StartY=125 StartZ=0 EndX=-73 EndY=125 EndZ=0
    g4: LineSegment StartX=-41 StartY=125 StartZ=0 EndX=-41 EndY=15 EndZ=0
    g5: LineSegment StartX=-41 StartY=15 StartZ=0 EndX=-19 EndY=15 EndZ=0
    g6: LineSegment StartX=-19 StartY=15 StartZ=0 EndX=-19 EndY=125 EndZ=0
    g7: LineSegment StartX=-19 StartY=125 StartZ=0 EndX=-41 EndY=125 EndZ=0
    g8: LineSegment StartX=-101 StartY=125 StartZ=0 EndX=-101 EndY=15 EndZ=0
    g9: LineSegment StartX=-101 StartY=15 StartZ=0 EndX=-83 EndY=15 EndZ=0
    g10: LineSegment StartX=-83 StartY=15 StartZ=0 EndX=-83 EndY=125 EndZ=0
    g11: LineSegment StartX=-83 StartY=125 StartZ=0 EndX=-101 EndY=125 EndZ=0
    g12: LineSegment StartX=-9 StartY=125 StartZ=0 EndX=-9 EndY=15 EndZ=0
    g13: LineSegment StartX=-9 StartY=15 StartZ=0 EndX=13 EndY=15 EndZ=0
    g14: LineSegment StartX=13 StartY=15 StartZ=0 EndX=13 EndY=125 EndZ=0
    g15: LineSegment StartX=13 StartY=125 StartZ=0 EndX=-9 EndY=125 EndZ=0
    g16: LineSegment [constr] StartX=-125.86 StartY=125 StartZ=0 EndX=26.0337 EndY=125 EndZ=0
    g17: LineSegment [constr] StartX=-133.161 StartY=15 StartZ=0 EndX=42.6244 EndY=15 EndZ=0
    g18: LineSegment [constr] StartX=-136.946 StartY=140 StartZ=0 EndX=57.8834 EndY=140 EndZ=0
  constraints (54):
    c: Coincident(g0,g1)
    c: Coincident(g1,g2)
    c: Coincident(g2,g3)
    c: Coincident(g3,g0)
    c: Vertical(g0)
    c: Vertical(g2)
    c: Horizontal(g1)
    c: Horizontal(g3)
    c: Coincident(g4,g5)
    c: Coincident(g5,g6)
    c: Coincident(g6,g7)
    c: Coincident(g7,g4)
    c: Vertical(g4)
    c: Vertical(g6)
    c: Horizontal(g5)
    c: Horizontal(g7)
    c: Coincident(g8,g9)
    c: Coincident(g9,g10)
    c: Coincident(g10,g11)
    c: Coincident(g11,g8)
    c: Vertical(g8)
    c: Vertical(g10)
    c: Horizontal(g9)
    c: Horizontal(g11)
    c: Coincident(g12,g13)
    c: Coincident(g13,g14)
    c: Coincident(g14,g15)
    c: Coincident(g15,g12)
    c: Vertical(g12)
    c: Vertical(g14)
    c: Horizontal(g13)
    c: Horizontal(g15)
    c: Horizontal(g16)
    c: PointOnObject(g12,g16)
    c: PointOnObject(g6,g16)
    c: PointOnObject(g2,g16)
    c: PointOnObject(g10,g16)
    c: Horizontal(g17)
    c: PointOnObject(g13,g17)
    c: PointOnObject(g5,g17)
    c: PointOnObject(g1,g17)
    c: PointOnObject(g9,g17)
    c: DistanceX(g5,g5) = 22
    c: DistanceX(g13,g13) = 22
    c: DistanceX(g1,g1) = 22
    c: DistanceX(g9,g9) = 18
    c: DistanceX(g1,g4) = 10
    c: DistanceX(g9,g0) = 10
    c: DistanceX(g5,g12) = 10
    c: DistanceX(g12,g-1) = 9
    c: DistanceY(g-1,g13) = 15
    c: Horizontal(g18)
    c: Distance(g-1,g18) = 140
    c: DistanceY(g16,g18) = 15
FEATURE [PartDesign::Pocket] Pocket002
  BaseFeature = -> Pocket001
  Direction = (1,0,2e-16)
  Length = 5
  Length2 = 5
  Placement = pos=(0,0,0) rot=(1,0,0;1.5708rad)
  Profile = -> Sketch006
  ReferenceAxis = -> Sketch006 [N_Axis]
  Suppressed = false
  Type = 1
FEATURE [Sketcher::SketchObject] Sketch007
  ArcFitTolerance = 1e-06
  AttachmentSupport = -> [Pocket002]
  FullyConstrained = false
  MakeInternals = false
  MapMode = 5
  Placement = pos=(114,0,0) rot=(0.707107,0,-0.707107;3.14159rad)
  sketch-geometry (11):
    g0: LineSegment [constr] StartX=-134.595 StartY=8 StartZ=0 EndX=9.49005 EndY=8 EndZ=0
    g1: LineSegment [constr] StartX=-130.483 StartY=133 StartZ=0 EndX=15.9048 EndY=133 EndZ=0
    g2: Circle CenterX=-59 CenterY=8 CenterZ=0 NormalX=0 NormalY=0 NormalZ=1 AngleXU=0 Radius=2.25
    g3: Circle CenterX=-91 CenterY=8 CenterZ=0 NormalX=0 NormalY=0 NormalZ=1 AngleXU=0 Radius=2.25
    g4: Circle CenterX=-27 CenterY=8 CenterZ=0 NormalX=0 NormalY=0 NormalZ=1 AngleXU=0 Radius=2.25
    g5: Circle CenterX=-91 CenterY=133 CenterZ=0 NormalX=0 NormalY=0 NormalZ=1 AngleXU=0 Radius=2.25
    g6: Circle CenterX=-59 CenterY=133 CenterZ=0 NormalX=0 NormalY=0 NormalZ=1 AngleXU=0 Radius=2.25
    g7: Circle CenterX=-27 CenterY=133 CenterZ=0 NormalX=0 NormalY=0 NormalZ=1 AngleXU=0 Radius=2.25
    g8: LineSegment [constr] StartX=-91 StartY=-16.0974 StartZ=0 EndX=-91 EndY=178.155 EndZ=0
    g9: LineSegment [constr] StartX=-59 StartY=-19.5515 StartZ=0 EndX=-59 EndY=212.696 EndZ=0
    g10: LineSegment [constr] StartX=-27 StartY=-14.6171 StartZ=0 EndX=-27 EndY=203.32 EndZ=0
  constraints (27):
    c: Horizontal(g0)
    c: Horizontal(g1)
    c: DistanceY(g0,g1) = 125
    c: DistanceY(g-1,g0) = 8
    c: PointOnObject(g2,g0)
    c: PointOnObject(g3,g0)
    c: Diameter(g3) = 4.5
    c: Equal(g3,g2)
    c: Equal(g3,g4)
    c: PointOnObject(g5,g1)
    c: PointOnObject(g6,g1)
    c: Equal(g5,g3)
    c: Equal(g6,g3)
    c: Equal(g7,g3)
    c: PointOnObject(g7,g1)
    c: Vertical(g8)
    c: Vertical(g9)
    c: Vertical(g10)
    c: PointOnObject(g4,g10)
    c: PointOnObject(g7,g10)
    c: PointOnObject(g6,g9)
    c: PointOnObject(g2,g9)
    c: PointOnObject(g5,g8)
    c: PointOnObject(g3,g8)
    c: DistanceX(g9,g10) = 32
    c: DistanceX(g8,g9) = 32
    c: DistanceX(g10,g-1) = 27
FEATURE [PartDesign::Pocket] Pocket003
  BaseFeature = -> Pocket002
  Direction = (1,0,2e-16)
  Length = 5
  Length2 = 5
  Placement = pos=(0,0,0) rot=(1,0,0;1.5708rad)
  Profile = -> Sketch007
  ReferenceAxis = -> Sketch007 [N_Axis]
  Suppressed = false
  Type = 1
FEATURE [PartDesign::Hole] Hole
  BaseFeature = -> Pocket003
  CustomThreadClearance = 0
  Depth = 4
  DepthType = 0
  Diameter = 9
  DrillForDepth = false
  DrillPoint = 0
  DrillPointAngle = 118
  HoleCutCountersinkAngle = 90
  HoleCutCustomValues = false
  HoleCutDepth = 0
  HoleCutDiameter = 0
  HoleCutType = 0
  ModelThread = false
  Placement = pos=(0,0,0) rot=(1,0,0;1.5708rad)
  Profile = -> Pocket003 [Edge133,Edge101,Edge99,Edge77,Edge79,Edge81]
  Reversed = true
  Suppressed = false
  Tapered = false
  TaperedAngle = 90
  ThreadClass = 0
  ThreadDepth = 4
  ThreadDepthType = 0
  ThreadDirection = 0
  ThreadFit = 0
  ThreadSize = 0
  ThreadType = 0
  Threaded = false
  UseCustomThreadClearance = false
FEATURE [Sketcher::SketchObject] Sketch008
  ArcFitTolerance = 1e-06
  AttachmentSupport = -> [Hole]
  FullyConstrained = false
  MakeInternals = false
  MapMode = 5
  Placement = pos=(0,-140,0) rot=(1,0,0;1.5708rad)
  sketch-geometry (6):
    g0: LineSegment [constr] StartX=118.5 StartY=105.765 StartZ=0 EndX=118.5 EndY=-12.1036 EndZ=0
    g1: Circle CenterX=118.5 CenterY=99 CenterZ=0 NormalX=0 NormalY=0 NormalZ=1 AngleXU=0 Radius=2.25
    g2: Circle CenterX=118.5 CenterY=67 CenterZ=0 NormalX=0 NormalY=0 NormalZ=1 AngleXU=0 Radius=2.25
    g3: Circle CenterX=118.5 CenterY=35 CenterZ=0 NormalX=0 NormalY=0 NormalZ=1 AngleXU=0 Radius=2.25
    g4: LineSegment [constr] StartX=123 StartY=116.723 StartZ=0 EndX=123 EndY=-13.1596 EndZ=0
    g5: Circle CenterX=118.5 CenterY=4 CenterZ=0 NormalX=0 NormalY=0 NormalZ=1 AngleXU=0 Radius=2.25
  constraints (16):
    c: Vertical(g0)
    c: PointOnObject(g1,g0)
    c: PointOnObject(g2,g0)
    c: PointOnObject(g3,g0)
    c: Diameter(g1) = 4.5
    c: Equal(g2,g1)
    c: Equal(g3,g1)
    c: Distance(g3,g-1) = 35
    c: Distance(g3,g2) = 32
    c: Distance(g2,g1) = 32
    c: Vertical(g4)
    c: DistanceX(g-1,g4) = 123
    c: Distance(g4,g0) = 4.5
    c: PointOnObject(g5,g0)
    c: Equal(g5,g3)
    c: DistanceY(g5,g3) = 31
FEATURE [PartDesign::Pocket] Pocket004
  BaseFeature = -> Hole
  Direction = (0,1,-2e-16)
  Length = 6
  Length2 = 5
  Placement = pos=(0,0,0) rot=(1,0,0;1.5708rad)
  Profile = -> Sketch008
  ReferenceAxis = -> Sketch008 [N_Axis]
  Suppressed = false
  Type = 0
FEATURE [Sketcher::SketchObject] Sketch009
  ArcFitTolerance = 1e-06
  AttachmentSupport = -> [Pocket004]
  FullyConstrained = false
  MakeInternals = false
  MapMode = 5
  Placement = pos=(0,1.16e-14,0) rot=(-1,0,0;1.5708rad)
  sketch-geometry (7):
    g0: LineSegment [constr] StartX=123 StartY=-122.065 StartZ=0 EndX=123 EndY=37.961 EndZ=0
    g1: LineSegment [constr] StartX=118.5 StartY=22.969 StartZ=0 EndX=118.5 EndY=-156.969 EndZ=0
    g2: Circle CenterX=118.5 CenterY=-99 CenterZ=0 NormalX=0 NormalY=0 NormalZ=1 AngleXU=0 Radius=2.25
    g3: Circle CenterX=118.5 CenterY=-67 CenterZ=0 NormalX=0 NormalY=0 NormalZ=1 AngleXU=0 Radius=2.25
    g4: Circle CenterX=118.5 CenterY=-35 CenterZ=0 NormalX=0 NormalY=0 NormalZ=1 AngleXU=0 Radius=2.25
    g5: LineSegment [constr] StartX=156.833 StartY=-4 StartZ=0 EndX=80.1669 EndY=-4 EndZ=0
    g6: Circle CenterX=118.5 CenterY=-4 CenterZ=0 NormalX=0 NormalY=0 NormalZ=1 AngleXU=0 Radius=2.25
  constraints (18):
    c: Vertical(g0)
    c: Vertical(g1)
    c: Distance(g-1,g0) = 123
    c: Distance(g0,g1) = 4.5
    c: PointOnObject(g2,g1)
    c: Symmetric(g1,g1,g3)
    c: PointOnObject(g4,g1)
    c: Distance(g4,g-1) = 35
    c: DistanceY(g3,g4) = 32
    c: DistanceY(g2,g3) = 32
    c: Diameter(g2) = 4.5
    c: Equal(g3,g2)
    c: Equal(g4,g2)
    c: Horizontal(g5)
    c: Distance(g4,g5) = 31
    c: Symmetric(g5,g5,g6)
    c: Equal(g2,g6)
    c: PointOnObject(g6,g1)
FEATURE [PartDesign::Pocket] Pocket005
  BaseFeature = -> Pocket004
  Direction = (0,-1,-2e-16)
  Length = 6
  Length2 = 5
  Placement = pos=(0,0,0) rot=(1,0,0;1.5708rad)
  Profile = -> Sketch009
  ReferenceAxis = -> Sketch009 [N_Axis]
  Suppressed = false
  Type = 0
FEATURE [Sketcher::SketchObject] Sketch010
  ArcFitTolerance = 1e-06
  AttachmentSupport = -> [Pad001]
  FullyConstrained = false
  MakeInternals = false
  MapMode = 5
  Placement = pos=(0,-20,0) rot=(1,0,0;1.5708rad)
  sketch-geometry (12):
    g0: LineSegment [constr] StartX=118.5 StartY=132.158 StartZ=0 EndX=118.5 EndY=-19.1161 EndZ=0
    g1: LineSegment [constr] StartX=4.5 StartY=125.192 StartZ=0 EndX=4.5 EndY=-14.1399 EndZ=0
    g2: LineSegment [constr] StartX=123 StartY=132.755 StartZ=0 EndX=123 EndY=-31.2578 EndZ=0
    g3: LineSegment [constr] StartX=-16.8458 StartY=99 StartZ=0 EndX=200.114 EndY=99 EndZ=0
    g4: LineSegment [constr] StartX=159.309 StartY=67 StartZ=0 EndX=-18.2391 EndY=67 EndZ=0
    g5: LineSegment [constr] StartX=16.0716 StartY=35 StartZ=0 EndX=220.928 EndY=35 EndZ=0
    g6: Circle CenterX=4.5 CenterY=99 CenterZ=0 NormalX=0 NormalY=0 NormalZ=1 AngleXU=0 Radius=2
    g7: Circle CenterX=4.5 CenterY=67 CenterZ=0 NormalX=0 NormalY=0 NormalZ=1 AngleXU=0 Radius=2
    g8: Circle CenterX=4.5 CenterY=35 CenterZ=0 NormalX=0 NormalY=0 NormalZ=1 AngleXU=0 Radius=2
    g9: Circle CenterX=118.5 CenterY=35 CenterZ=0 NormalX=0 NormalY=0 NormalZ=1 AngleXU=0 Radius=2
    g10: Circle CenterX=118.5 CenterY=67 CenterZ=0 NormalX=0 NormalY=0 NormalZ=1 AngleXU=0 Radius=2
    g11: Circle CenterX=118.5 CenterY=99 CenterZ=0 NormalX=0 NormalY=0 NormalZ=1 AngleXU=0 Radius=2
  constraints (30):
    c: Vertical(g0)
    c: Vertical(g1)
    c: Vertical(g2)
    c: Distance(g2,g-2) = 123
    c: Distance(g0,g2) = 4.5
    c: Distance(g-2,g1) = 4.5
    c: Horizontal(g3)
    c: Horizontal(g4)
    c: Horizontal(g5)
    c: Distance(g-1,g5) = 35
    c: Distance(g5,g4) = 32
    c: Distance(g4,g3) = 32
    c: PointOnObject(g6,g3)
    c: PointOnObject(g6,g1)
    c: Diameter(g6) = 4
    c: PointOnObject(g7,g4)
    c: PointOnObject(g8,g5)
    c: Symmetric(g5,g5,g9)
    c: PointOnObject(g10,g4)
    c: PointOnObject(g11,g3)
    c: Equal(g7,g6)
    c: Equal(g6,g8)
    c: Equal(g9,g6)
    c: Equal(g10,g6)
    c: Equal(g11,g6)
    c: PointOnObject(g7,g1)
    c: PointOnObject(g8,g1)
    c: PointOnObject(g9,g0)
    c: PointOnObject(g10,g0)
    c: PointOnObject(g11,g0)
FEATURE [PartDesign::Pocket] Pocket006
  BaseFeature = -> Pad001
  Direction = (0,1,-2e-16)
  Length = 5
  Length2 = 5
  Placement = pos=(0,0,0) rot=(1,0,0;1.5708rad)
  Profile = -> Sketch010
  ReferenceAxis = -> Sketch010 [N_Axis]
  Suppressed = false
  Type = 1
FEATURE [PartDesign::Hole] Hole001
  BaseFeature = -> Pocket006
  CustomThreadClearance = 0
  Depth = 4
  DepthType = 0
  Diameter = 6.5
  DrillForDepth = false
  DrillPoint = 0
  DrillPointAngle = 118
  HoleCutCountersinkAngle = 90
  HoleCutCustomValues = false
  HoleCutDepth = 0
  HoleCutDiameter = 0
  HoleCutType = 0
  ModelThread = false
  Placement = pos=(0,0,0) rot=(1,0,0;1.5708rad)
  Profile = -> Pocket006 [Edge77,Edge76,Edge47,Edge78,Edge79,Edge80]
  Reversed = true
  Suppressed = false
  Tapered = false
  TaperedAngle = 90
  ThreadClass = 0
  ThreadDepth = 4
  ThreadDepthType = 0
  ThreadDirection = 0
  ThreadFit = 0
  ThreadSize = 0
  ThreadType = 0
  Threaded = false
  UseCustomThreadClearance = false
FEATURE [Sketcher::SketchObject] Sketch011
  ArcFitTolerance = 1e-06
  AttachmentSupport = -> [Hole001]
  FullyConstrained = false
  MakeInternals = false
  MapMode = 5
  Placement = pos=(114,0,0) rot=(0.707107,0,-0.707107;3.14159rad)
  sketch-geometry (15):
    g0: LineSegment StartX=-22.5 StartY=12 StartZ=0 EndX=-22.5 EndY=8 EndZ=0
    g1: LineSegment StartX=-22.5 StartY=8 StartZ=0 EndX=-5.5 EndY=8 EndZ=0
    g2: LineSegment StartX=-5.5 StartY=8 StartZ=0 EndX=-5.5 EndY=12 EndZ=0
    g3: LineSegment StartX=-5.5 StartY=12 StartZ=0 EndX=-22.5 EndY=12 EndZ=0
    g4: LineSegment [constr] StartX=8.51359 StartY=8 StartZ=0 EndX=-80.9516 EndY=8 EndZ=0
    g5: LineSegment StartX=-55 StartY=12 StartZ=0 EndX=-55 EndY=8 EndZ=0
    g6: LineSegment StartX=-55 StartY=8 StartZ=0 EndX=-38 EndY=8 EndZ=0
    g7: LineSegment StartX=-38 StartY=8 StartZ=0 EndX=-38 EndY=12 EndZ=0
    g8: LineSegment StartX=-38 StartY=12 StartZ=0 EndX=-55 EndY=12 EndZ=0
    g9: LineSegment StartX=-87.5 StartY=8 StartZ=0 EndX=-70.5 EndY=8 EndZ=0
    g10: LineSegment StartX=-70.5 StartY=8 StartZ=0 EndX=-70.5 EndY=12 EndZ=0
    g11: LineSegment StartX=-70.5 StartY=12 StartZ=0 EndX=-87.5 EndY=12 EndZ=0
    g12: LineSegment StartX=-87.5 StartY=12 StartZ=0 EndX=-87.5 EndY=8 EndZ=0
    g13: LineSegment [constr] StartX=-91.0714 StartY=12 StartZ=0 EndX=35.9561 EndY=12 EndZ=0
    g14: LineSegment [constr] StartX=-5 StartY=36.091 StartZ=0 EndX=-5 EndY=-17.7362 EndZ=0
  constraints (42):
    c: Coincident(g0,g1)
    c: Coincident(g1,g2)
    c: Coincident(g2,g3)
    c: Coincident(g3,g0)
    c: Vertical(g0)
    c: Vertical(g2)
    c: Horizontal(g1)
    c: Horizontal(g3)
    c: Horizontal(g4)
    c: PointOnObject(g1,g4)
    c: Coincident(g5,g6)
    c: Coincident(g6,g7)
    c: Coincident(g7,g8)
    c: Coincident(g8,g5)
    c: Vertical(g5)
    c: Vertical(g7)
    c: Horizontal(g6)
    c: Horizontal(g8)
    c: Coincident(g9,g10)
    c: Coincident(g10,g11)
    c: Coincident(g11,g12)
    c: Coincident(g12,g9)
    c: Horizontal(g9)
    c: Horizontal(g11)
    c: Vertical(g10)
    c: Vertical(g12)
    c: PointOnObject(g9,g4)
    c: PointOnObject(g6,g4)
    c: DistanceY(g-1,g4) = 8
    c: Horizontal(g13)
    c: PointOnObject(g10,g13)
    c: PointOnObject(g5,g13)
    c: PointOnObject(g0,g13)
    c: Distance(g4,g13) = 4
    c: DistanceX(g3,g3) = 17
    c: Vertical(g14)
    c: Distance(g14,g-2) = 5
    c: Distance(g1,g14) = 0.5
    c: DistanceX(g8,g8) = 17
    c: DistanceX(g7,g0) = 15.5
    c: Distance(g10,g5) = 15.5
    c: DistanceX(g11,g11) = 17
FEATURE [PartDesign::Pocket] Pocket007
  BaseFeature = -> Hole001
  Direction = (1,0,2e-16)
  Length = 4.5
  Length2 = 109.5
  Placement = pos=(0,0,0) rot=(1,0,0;1.5708rad)
  Profile = -> Sketch011
  ReferenceAxis = -> Sketch011 [N_Axis]
  Suppressed = false
  Type = 4
FEATURE [PartDesign::Fillet] Fillet004
  Base = -> Pocket007 [Edge164,Edge217,Edge134,Edge207,Edge104,Edge197,Edge106,Edge198,Edge136,Edge208,Edge166,Edge218,Edge199,Edge126,Edge189,Edge96,Edge209,Edge156,Edge211,Edge158,Edge201,Edge128,Edge191,Edge98]
  BaseFeature = -> Pocket007
  Placement = pos=(0,0,0) rot=(1,0,0;1.5708rad)
  Radius = 1
  SupportTransform = false
  Suppressed = false
  UseAllEdges = false
FEATURE [Sketcher::SketchObject] Sketch012
  ArcFitTolerance = 1e-06
  AttachmentSupport = -> [XZ_Plane003]
  FullyConstrained = false
  MakeInternals = false
  MapMode = 5
  Placement = pos=(0,0,0) rot=(1,0,0;1.5708rad)
  sketch-geometry (73):
    g0: LineSegment [constr] StartX=0 StartY=0 StartZ=0 EndX=123 EndY=0 EndZ=0
    g1: LineSegment StartX=123 StartY=0 StartZ=0 EndX=123 EndY=105 EndZ=0
    g2: LineSegment StartX=123 StartY=105 StartZ=0 EndX=0 EndY=105 EndZ=0
    g3: LineSegment StartX=9 StartY=5 StartZ=0 EndX=114 EndY=5 EndZ=0
    g4: LineSegment StartX=114 StartY=100 StartZ=0 EndX=9 EndY=100 EndZ=0
    g5: LineSegment [constr] StartX=190.257 StartY=65.8 StartZ=0 EndX=190.257 EndY=40.4 EndZ=0
    g6: LineSegment [constr] StartX=190.257 StartY=40.4 StartZ=0 EndX=291.857 EndY=40.4 EndZ=0
    g7: LineSegment [constr] StartX=291.857 StartY=40.4 StartZ=0 EndX=291.857 EndY=65.8 EndZ=0
    g8: LineSegment [constr] StartX=291.857 StartY=65.8 StartZ=0 EndX=190.257 EndY=65.8 EndZ=0
    g9: LineSegment [constr] StartX=184.257 StartY=52.4 StartZ=0 EndX=184.257 EndY=40.4 EndZ=0
    g10: LineSegment [constr] StartX=184.257 StartY=40.4 StartZ=0 EndX=190.257 EndY=40.4 EndZ=0
    g11: LineSegment [constr] StartX=190.257 StartY=40.4 StartZ=0 EndX=190.257 EndY=52.4 EndZ=0
    g12: LineSegment [constr] StartX=190.257 StartY=52.4 StartZ=0 EndX=184.257 EndY=52.4 EndZ=0
    g13: LineSegment [constr] StartX=291.857 StartY=52.4 StartZ=0 EndX=291.857 EndY=40.4 EndZ=0
    g14: LineSegment [constr] StartX=291.857 StartY=40.4 StartZ=0 EndX=297.857 EndY=40.4 EndZ=0
    g15: LineSegment [constr] StartX=297.857 StartY=40.4 StartZ=0 EndX=297.857 EndY=52.4 EndZ=0
    g16: LineSegment [constr] StartX=297.857 StartY=52.4 StartZ=0 EndX=291.857 EndY=52.4 EndZ=0
    g17: LineSegment [constr] StartX=163.474 StartY=98.2 StartZ=0 EndX=163.474 EndY=72.8 EndZ=0
    g18: LineSegment [constr] StartX=163.474 StartY=72.8 StartZ=0 EndX=265.074 EndY=72.8 EndZ=0
    g19: LineSegment [constr] StartX=265.074 StartY=72.8 StartZ=0 EndX=265.074 EndY=98.2 EndZ=0
    g20: LineSegment [constr] StartX=265.074 StartY=98.2 StartZ=0 EndX=163.474 EndY=98.2 EndZ=0
    g21: LineSegment [constr] StartX=157.474 StartY=84.8 StartZ=0 EndX=157.474 EndY=72.8 EndZ=0
    g22: LineSegment [constr] StartX=157.474 StartY=72.8 StartZ=0 EndX=163.474 EndY=72.8 EndZ=0
    g23: LineSegment [constr] StartX=163.474 StartY=72.8 StartZ=0 EndX=163.474 EndY=84.8 EndZ=0
    g24: LineSegment [constr] StartX=163.474 StartY=84.8 StartZ=0 EndX=157.474 EndY=84.8 EndZ=0
    g25: LineSegment [constr] StartX=265.074 StartY=84.8 StartZ=0 EndX=265.074 EndY=72.8 EndZ=0
    g26: LineSegment [constr] StartX=265.074 StartY=72.8 StartZ=0 EndX=271.074 EndY=72.8 EndZ=0
    g27: LineSegment [constr] StartX=271.074 StartY=72.8 StartZ=0 EndX=271.074 EndY=84.8 EndZ=0
    g28: LineSegment [constr] StartX=271.074 StartY=84.8 StartZ=0 EndX=265.074 EndY=84.8 EndZ=0
    g29: LineSegment [constr] StartX=208.539 StartY=33.4 StartZ=0 EndX=208.539 EndY=8 EndZ=0
    g30: LineSegment [constr] StartX=208.539 StartY=8 StartZ=0 EndX=310.139 EndY=8 EndZ=0
    g31: LineSegment [constr] StartX=310.139 StartY=8 StartZ=0 EndX=310.139 EndY=33.4 EndZ=0
    g32: LineSegment [constr] StartX=310.139 StartY=33.4 StartZ=0 EndX=208.539 EndY=33.4 EndZ=0
    g33: LineSegment [constr] StartX=202.539 StartY=20 StartZ=0 EndX=202.539 EndY=8 EndZ=0
    g34: LineSegment [constr] StartX=202.539 StartY=8 StartZ=0 EndX=208.539 EndY=8 EndZ=0
    g35: LineSegment [constr] StartX=208.539 StartY=8 StartZ=0 EndX=208.539 EndY=20 EndZ=0
    g36: LineSegment [constr] StartX=208.539 StartY=20 StartZ=0 EndX=202.539 EndY=20 EndZ=0
    g37: LineSegment [constr] StartX=310.139 StartY=20 StartZ=0 EndX=310.139 EndY=8 EndZ=0
    g38: LineSegment [constr] StartX=310.139 StartY=8 StartZ=0 EndX=316.139 EndY=8 EndZ=0
    g39: LineSegment [constr] StartX=316.139 StartY=8 StartZ=0 EndX=316.139 EndY=20 EndZ=0
    g40: LineSegment [constr] StartX=316.139 StartY=20 StartZ=0 EndX=310.139 EndY=20 EndZ=0
    g41: LineSegment StartX=0 StartY=0 StartZ=0 EndX=123 EndY=0 EndZ=0
    g42: LineSegment [constr] StartX=9 StartY=177.265 StartZ=0 EndX=9 EndY=-72.0652 EndZ=0
    g43: LineSegment [constr] StartX=114 StartY=141.11 StartZ=0 EndX=114 EndY=26.7674 EndZ=0
    g44: LineSegment StartX=9 StartY=100 StartZ=0 EndX=9 EndY=84.9 EndZ=0
    g45: LineSegment StartX=9 StartY=84.9 StartZ=0 EndX=8 EndY=84.9 EndZ=0
    g46: LineSegment StartX=8 StartY=84.9 StartZ=0 EndX=8 EndY=72.6 EndZ=0
    g47: LineSegment StartX=8 StartY=72.6 StartZ=0 EndX=9 EndY=72.6 EndZ=0
    g48: LineSegment StartX=9 StartY=72.6 StartZ=0 EndX=9 EndY=52.6 EndZ=0
    g49: LineSegment StartX=9 StartY=52.6 StartZ=0 EndX=8 EndY=52.6 EndZ=0
    g50: LineSegment StartX=8 StartY=52.6 StartZ=0 EndX=8 EndY=40.3 EndZ=0
    g51: LineSegment StartX=8 StartY=40.3 StartZ=0 EndX=9 EndY=40.3 EndZ=0
    g52: LineSegment StartX=9 StartY=40.3 StartZ=0 EndX=9 EndY=20.3 EndZ=0
    g53: LineSegment StartX=9 StartY=20.3 StartZ=0 EndX=8 EndY=20.3 EndZ=0
    g54: LineSegment StartX=8 StartY=20.3 StartZ=0 EndX=8 EndY=8 EndZ=0
    g55: LineSegment StartX=8 StartY=8 StartZ=0 EndX=9 EndY=8 EndZ=0
    g56: LineSegment StartX=9 StartY=8 StartZ=0 EndX=9 EndY=5 EndZ=0
    g57: LineSegment [constr] StartX=8 StartY=110.102 StartZ=0 EndX=8 EndY=-9.82312 EndZ=0
    g58: LineSegment StartX=114 StartY=100 StartZ=0 EndX=114 EndY=84.9 EndZ=0
    g59: LineSegment StartX=114 StartY=84.9 StartZ=0 EndX=115 EndY=84.9 EndZ=0
    g60: LineSegment StartX=115 StartY=84.9 StartZ=0 EndX=115 EndY=72.6 EndZ=0
    g61: LineSegment StartX=115 StartY=72.6 StartZ=0 EndX=114 EndY=72.6 EndZ=0
    g62: LineSegment StartX=114 StartY=72.6 StartZ=0 EndX=114 EndY=52.6 EndZ=0
    g63: LineSegment StartX=114 StartY=52.6 StartZ=0 EndX=115 EndY=52.6 EndZ=0
    g64: LineSegment StartX=115 StartY=52.6 StartZ=0 EndX=115 EndY=40.3 EndZ=0
    g65: LineSegment StartX=115 StartY=40.3 StartZ=0 EndX=114 EndY=40.3 EndZ=0
    g66: LineSegment StartX=114 StartY=40.3 StartZ=0 EndX=114 EndY=20.3 EndZ=0
    g67: LineSegment StartX=114 StartY=20.3 StartZ=0 EndX=115 EndY=20.3 EndZ=0
    g68: LineSegment StartX=115 StartY=20.3 StartZ=0 EndX=115 EndY=8 EndZ=0
    g69: LineSegment StartX=115 StartY=8 StartZ=0 EndX=114 EndY=8 EndZ=0
    g70: LineSegment StartX=114 StartY=8 StartZ=0 EndX=114 EndY=5 EndZ=0
    g71: LineSegment [constr] StartX=115 StartY=112.118 StartZ=0 EndX=115 EndY=-16.6316 EndZ=0
    g72: LineSegment StartX=0 StartY=105 StartZ=0 EndX=0 EndY=0 EndZ=0
  constraints (212):
    c: Coincident(g-1,g0)
    c: Horizontal(g0)
    c: Coincident(g0,g1)
    c: Vertical(g1)
    c: Coincident(g1,g2)
    c: PointOnObject(g2,g-2)
    c: Horizontal(g2)
    c: Horizontal(g3)
    c: Horizontal(g4)
    c: Coincident(g5,g6)
    c: Coincident(g6,g7)
    c: Coincident(g7,g8)
    c: Coincident(g8,g5)
    c: Vertical(g5)
    c: Vertical(g7)
    c: Horizontal(g6)
    c: Horizontal(g8)
    c: DistanceX(g8,g8) = 101.6
    c: DistanceY(g7,g7) = 25.4
    c: Coincident(g9,g10)
    c: Coincident(g10,g11)
    c: Coincident(g11,g12)
    c: Coincident(g12,g9)
    c: Vertical(g9)
    c: Vertical(g11)
    c: Horizontal(g10)
    c: Horizontal(g12)
    c: DistanceX(g12,g12) = 6
    c: DistanceY(g11,g11) = 12
    c: PointOnObject(g11,g5)
    c: Coincident(g13,g14)
    c: Coincident(g14,g15)
    c: Coincident(g15,g16)
    c: Coincident(g16,g13)
    c: Vertical(g13)
    c: Vertical(g15)
    c: Horizontal(g14)
    c: Horizontal(g16)
    c: DistanceX(g16,g16) = 6
    c: DistanceY(g15,g15) = 12
    c: PointOnObject(g13,g7)
    c: DistanceY(g5,g10) = 0
    c: DistanceY(g6,g13) = 0
    c: DistanceX(g3,g3) = 105
    c: Coincident(g17,g18)
    c: Coincident(g18,g19)
    c: Coincident(g19,g20)
    c: Coincident(g20,g17)
    c: Vertical(g17)
    c: Vertical(g19)
    c: Horizontal(g18)
    c: Horizontal(g20)
    c: DistanceX(g20,g20) = 101.6
    c: DistanceY(g19,g19) = 25.4
    c: Coincident(g21,g22)
    c: Coincident(g22,g23)
    c: Coincident(g23,g24)
    c: Coincident(g24,g21)
    c: Vertical(g21)
    c: Vertical(g23)
    c: Horizontal(g22)
    c: Horizontal(g24)
    c: DistanceX(g24,g24) = 6
    c: DistanceY(g23,g23) = 12
    c: PointOnObject(g23,g17)
    c: Coincident(g25,g26)
    c: Coincident(g26,g27)
    c: Coincident(g27,g28)
    c: Coincident(g28,g25)
    c: Vertical(g25)
    c: Vertical(g27)
    c: Horizontal(g26)
    c: Horizontal(g28)
    c: DistanceX(g28,g28) = 6
    c: DistanceY(g27,g27) = 12
    c: PointOnObject(g25,g19)
    c: DistanceY(g17,g22) = 0
    c: DistanceY(g18,g25) = 0
    c: Coincident(g29,g30)
    c: Coincident(g30,g31)
    c: Coincident(g31,g32)
    c: Coincident(g32,g29)
    c: Vertical(g29)
    c: Vertical(g31)
    c: Horizontal(g30)
    c: Horizontal(g32)
    c: DistanceX(g32,g32) = 101.6
    c: DistanceY(g31,g31) = 25.4
    c: Coincident(g33,g34)
    c: Coincident(g34,g35)
    c: Coincident(g35,g36)
    c: Coincident(g36,g33)
    c: Vertical(g33)
    c: Vertical(g35)
    c: Horizontal(g34)
    c: Horizontal(g36)
    c: DistanceX(g36,g36) = 6
    c: DistanceY(g35,g35) = 12
    c: PointOnObject(g35,g29)
    c: Coincident(g37,g38)
    c: Coincident(g38,g39)
    c: Coincident(g39,g40)
    c: Coincident(g40,g37)
    c: Vertical(g37)
    c: Vertical(g39)
    c: Horizontal(g38)
    c: Horizontal(g40)
    c: DistanceX(g40,g40) = 6
    c: DistanceY(g39,g39) = 12
    c: PointOnObject(g37,g31)
    c: DistanceY(g29,g34) = 0
    c: DistanceY(g30,g37) = 0
    c: DistanceY(g0,g29) = 8
    c: Distance(g32,g6) = 7
    c: Distance(g8,g18) = 7
    c: DistanceX(g0,g0) = 123
    c: Coincident(g41,g0)
    c: Coincident(g41,g0)
    c: Vertical(g43)
    c: Distance(g0,g43) = 9
    c: DistanceX(g0,g42) = 9
    c: PointOnObject(g3,g42)
    c: PointOnObject(g4,g42)
    c: PointOnObject(g3,g43)
    c: PointOnObject(g4,g43)
    c: Coincident(g4,g44)
    c: PointOnObject(g44,g42)
    c: Coincident(g44,g45)
    c: Horizontal(g45)
    c: Coincident(g45,g46)
    c: Vertical(g46)
    c: Coincident(g46,g47)
    c: PointOnObject(g47,g42)
    c: Horizontal(g47)
    c: Coincident(g47,g48)
    c: Symmetric(g42,g42,g48)
    c: Coincident(g48,g49)
    c: Horizontal(g49)
    c: Coincident(g49,g50)
    c: Vertical(g50)
    c: Coincident(g50,g51)
    c: Horizontal(g51)
    c: Coincident(g51,g52)
    c: Coincident(g52,g53)
    c: Coincident(g53,g54)
    c: Coincident(g54,g55)
    c: PointOnObject(g55,g42)
    c: Horizontal(g55)
    c: Coincident(g55,g56)
    c: Coincident(g56,g3)
    c: PointOnObject(g51,g42)
    c: Vertical(g52)
    c: Vertical(g54)
    c: Vertical(g57)
    c: PointOnObject(g45,g57)
    c: PointOnObject(g49,g57)
    c: PointOnObject(g53,g57)
    c: DistanceY(g50,g50) = 12.3
    c: DistanceY(g46,g46) = 12.3
    c: DistanceY(g54,g54) = 12.3
    c: Horizontal(g53)
    c: Vertical(g42)
    c: DistanceX(g57,g42) = 1
    c: DistanceY(g56,g56) = 3
    c: DistanceY(g52,g52) = 20
    c: DistanceY(g48,g48) = 20
    c: Coincident(g4,g58)
    c: Vertical(g58)
    c: Coincident(g58,g59)
    c: Horizontal(g59)
    c: Coincident(g59,g60)
    c: Coincident(g60,g61)
    c: Coincident(g61,g62)
    c: Coincident(g62,g63)
    c: Horizontal(g63)
    c: Coincident(g63,g64)
    c: Vertical(g64)
    c: Coincident(g64,g65)
    c: Horizontal(g65)
    c: Coincident(g65,g66)
    c: Vertical(g66)
    c: Coincident(g66,g67)
    c: Horizontal(g67)
    c: Coincident(g67,g68)
    c: Vertical(g68)
    c: Coincident(g68,g69)
    c: Horizontal(g69)
    c: Coincident(g69,g70)
    c: Coincident(g70,g3)
    c: PointOnObject(g62,g43)
    c: Vertical(g62)
    c: PointOnObject(g65,g43)
    c: Vertical(g60)
    c: Horizontal(g61)
    c: Vertical(g71)
    c: PointOnObject(g60,g71)
    c: PointOnObject(g64,g71)
    c: Vertical(g70)
    c: PointOnObject(g67,g71)
    c: DistanceY(g64,g64) = 12.3
    c: DistanceY(g60,g60) = 12.3
    c: DistanceY(g68,g68) = 12.3
    c: DistanceY(g66,g66) = 20
    c: DistanceY(g62,g62) = 20
    c: DistanceX(g43,g71) = 1
    c: Coincident(g2,g72)
    c: Coincident(g72,g0)
    c: DistanceY(g4,g1) = 5
    c: DistanceY(g17,g4) = 1.8
    c: DistanceY(g0,g3) = 5
    c: DistanceY(g3,g69) = 3
    c: DistanceY(g72,g72) = 105
FEATURE [PartDesign::Pad] Pad003
  Direction = (0,-1,2e-16)
  Length = 15
  Length2 = 10
  Placement = pos=(0,0,0) rot=(1,0,0;1.5708rad)
  Profile = -> Sketch012
  ReferenceAxis = -> Sketch012 [N_Axis]
  Suppressed = false
  Type = 0
FEATURE [Sketcher::SketchObject] Sketch013
  ArcFitTolerance = 1e-06
  AttachmentSupport = -> [Pad003]
  FullyConstrained = false
  MakeInternals = false
  MapMode = 5
  Placement = pos=(0,-15,0) rot=(1,0,0;1.5708rad)
  sketch-geometry (12):
    g0: LineSegment [constr] StartX=118.5 StartY=132.158 StartZ=0 EndX=118.5 EndY=-19.1161 EndZ=0
    g1: LineSegment [constr] StartX=4.5 StartY=125.192 StartZ=0 EndX=4.5 EndY=-14.1399 EndZ=0
    g2: LineSegment [constr] StartX=123 StartY=132.755 StartZ=0 EndX=123 EndY=-31.2578 EndZ=0
    g3: LineSegment [constr] StartX=-16.8458 StartY=99 StartZ=0 EndX=200.114 EndY=99 EndZ=0
    g4: LineSegment [constr] StartX=159.309 StartY=67 StartZ=0 EndX=-18.2391 EndY=67 EndZ=0
    g5: LineSegment [constr] StartX=16.0716 StartY=35 StartZ=0 EndX=220.928 EndY=35 EndZ=0
    g6: Circle CenterX=4.5 CenterY=99 CenterZ=0 NormalX=0 NormalY=0 NormalZ=1 AngleXU=0 Radius=2
    g7: Circle CenterX=4.5 CenterY=67 CenterZ=0 NormalX=0 NormalY=0 NormalZ=1 AngleXU=0 Radius=2
    g8: Circle CenterX=4.5 CenterY=35 CenterZ=0 NormalX=0 NormalY=0 NormalZ=1 AngleXU=0 Radius=2
    g9: Circle CenterX=118.5 CenterY=35 CenterZ=0 NormalX=0 NormalY=0 NormalZ=1 AngleXU=0 Radius=2
    g10: Circle CenterX=118.5 CenterY=67 CenterZ=0 NormalX=0 NormalY=0 NormalZ=1 AngleXU=0 Radius=2
    g11: Circle CenterX=118.5 CenterY=99 CenterZ=0 NormalX=0 NormalY=0 NormalZ=1 AngleXU=0 Radius=2
  constraints (30):
    c: Vertical(g0)
    c: Vertical(g1)
    c: Vertical(g2)
    c: Distance(g2,g-2) = 123
    c: Distance(g0,g2) = 4.5
    c: Distance(g-2,g1) = 4.5
    c: Horizontal(g3)
    c: Horizontal(g4)
    c: Horizontal(g5)
    c: Distance(g-1,g5) = 35
    c: Distance(g5,g4) = 32
    c: Distance(g4,g3) = 32
    c: PointOnObject(g6,g3)
    c: PointOnObject(g6,g1)
    c: Diameter(g6) = 4
    c: PointOnObject(g7,g4)
    c: PointOnObject(g8,g5)
    c: Symmetric(g5,g5,g9)
    c: PointOnObject(g10,g4)
    c: PointOnObject(g11,g3)
    c: Equal(g7,g6)
    c: Equal(g6,g8)
    c: Equal(g9,g6)
    c: Equal(g10,g6)
    c: Equal(g11,g6)
    c: PointOnObject(g7,g1)
    c: PointOnObject(g8,g1)
    c: PointOnObject(g9,g0)
    c: PointOnObject(g10,g0)
    c: PointOnObject(g11,g0)
FEATURE [PartDesign::Pocket] Pocket008
  BaseFeature = -> Pad003
  Direction = (0,1,-2e-16)
  Length = 5
  Length2 = 5
  Placement = pos=(0,0,0) rot=(1,0,0;1.5708rad)
  Profile = -> Sketch013
  ReferenceAxis = -> Sketch013 [N_Axis]
  Suppressed = false
  Type = 1
FEATURE [PartDesign::Hole] Hole002
  BaseFeature = -> Pocket008
  CustomThreadClearance = 0
  Depth = 4
  DepthType = 0
  Diameter = 6.5
  DrillForDepth = false
  DrillPoint = 0
  DrillPointAngle = 118
  HoleCutCountersinkAngle = 90
  HoleCutCustomValues = false
  HoleCutDepth = 0
  HoleCutDiameter = 6.1
  HoleCutType = 0
  ModelThread = false
  Placement = pos=(0,0,0) rot=(1,0,0;1.5708rad)
  Profile = -> Pocket008 [Edge77,Edge76,Edge47,Edge78,Edge79,Edge80]
  Reversed = true
  Suppressed = false
  Tapered = false
  TaperedAngle = 90
  ThreadClass = 0
  ThreadDepth = 4
  ThreadDepthType = 0
  ThreadDirection = 0
  ThreadFit = 0
  ThreadSize = 0
  ThreadType = 0
  Threaded = false
  UseCustomThreadClearance = false
FEATURE [Sketcher::SketchObject] Sketch014
  ArcFitTolerance = 1e-06
  AttachmentSupport = -> [Hole002]
  FullyConstrained = false
  MakeInternals = false
  MapMode = 5
  Placement = pos=(0,-15,0) rot=(1,0,0;1.5708rad)
  sketch-geometry (5):
    g0: LineSegment [constr] StartX=123 StartY=114.172 StartZ=0 EndX=123 EndY=-10.073 EndZ=0
    g1: LineSegment [constr] StartX=118.5 StartY=117.112 StartZ=0 EndX=118.5 EndY=-11.479 EndZ=0
    g2: Circle CenterX=118.5 CenterY=90 CenterZ=0 NormalX=0 NormalY=0 NormalZ=1 AngleXU=0 Radius=2.25
    g3: Circle CenterX=118.5 CenterY=58 CenterZ=0 NormalX=0 NormalY=0 NormalZ=1 AngleXU=0 Radius=2.25
    g4: Circle CenterX=118.5 CenterY=26 CenterZ=0 NormalX=0 NormalY=0 NormalZ=1 AngleXU=0 Radius=2.25
  constraints (13):
    c: Vertical(g0)
    c: DistanceX(g-1,g0) = 123
    c: Vertical(g1)
    c: Distance(g1,g0) = 4.5
    c: PointOnObject(g2,g1)
    c: PointOnObject(g3,g1)
    c: PointOnObject(g4,g1)
    c: Diameter(g2) = 4.5
    c: Equal(g3,g2)
    c: Equal(g4,g2)
    c: Distance(g4,g-1) = 26
    c: DistanceY(g4,g3) = 32
    c: DistanceY(g3,g2) = 32
FEATURE [PartDesign::Pocket] Pocket009
  BaseFeature = -> Hole002
  Direction = (0,1,-2e-16)
  Length = 7
  Length2 = 5
  Placement = pos=(0,0,0) rot=(1,0,0;1.5708rad)
  Profile = -> Sketch014
  ReferenceAxis = -> Sketch014 [N_Axis]
  Suppressed = false
  Type = 0
FEATURE [Sketcher::SketchObject] Sketch015
  ArcFitTolerance = 1e-06
  AttachmentSupport = -> [Fillet004]
  FullyConstrained = false
  MakeInternals = false
  MapMode = 5
  Placement = pos=(0,-20,0) rot=(1,0,0;1.5708rad)
  sketch-geometry (12):
    g0: LineSegment [constr] StartX=123 StartY=116.907 StartZ=0 EndX=123 EndY=-9.24195 EndZ=0
    g1: LineSegment [constr] StartX=4.5 StartY=128.929 StartZ=0 EndX=4.5 EndY=-14.8625 EndZ=0
    g2: LineSegment [constr] StartX=118.5 StartY=127.055 StartZ=0 EndX=118.5 EndY=-28.7576 EndZ=0
    g3: LineSegment [constr] StartX=-17.8127 StartY=89 StartZ=0 EndX=144.558 EndY=89 EndZ=0
    g4: LineSegment [constr] StartX=141.903 StartY=57 StartZ=0 EndX=-28.8976 EndY=57 EndZ=0
    g5: LineSegment [constr] StartX=-17.2081 StartY=25 StartZ=0 EndX=254.208 EndY=25 EndZ=0
    g6: Circle CenterX=4.5 CenterY=89 CenterZ=0 NormalX=0 NormalY=0 NormalZ=1 AngleXU=0 Radius=2.25
    g7: Circle CenterX=4.5 CenterY=57 CenterZ=0 NormalX=0 NormalY=0 NormalZ=1 AngleXU=0 Radius=2.25
    g8: Circle CenterX=4.5 CenterY=25 CenterZ=0 NormalX=0 NormalY=0 NormalZ=1 AngleXU=0 Radius=2.25
    g9: Circle CenterX=118.5 CenterY=25 CenterZ=0 NormalX=0 NormalY=0 NormalZ=1 AngleXU=0 Radius=2.25
    g10: Circle CenterX=118.5 CenterY=57 CenterZ=0 NormalX=0 NormalY=0 NormalZ=1 AngleXU=0 Radius=2.25
    g11: Circle CenterX=118.5 CenterY=89 CenterZ=0 NormalX=0 NormalY=0 NormalZ=1 AngleXU=0 Radius=2.25
  constraints (30):
    c: Vertical(g0)
    c: Vertical(g1)
    c: Vertical(g2)
    c: DistanceX(g2,g0) = 4.5
    c: DistanceX(g-1,g0) = 123
    c: Distance(g-1,g1) = 4.5
    c: Horizontal(g3)
    c: Horizontal(g4)
    c: Horizontal(g5)
    c: DistanceY(g-1,g5) = 25
    c: DistanceY(g5,g4) = 32
    c: DistanceY(g4,g3) = 32
    c: PointOnObject(g6,g3)
    c: PointOnObject(g7,g4)
    c: PointOnObject(g8,g5)
    c: Symmetric(g5,g5,g9)
    c: PointOnObject(g10,g4)
    c: PointOnObject(g11,g3)
    c: Diameter(g6) = 4.5
    c: Equal(g7,g6)
    c: Equal(g6,g8)
    c: Equal(g10,g6)
    c: Equal(g9,g6)
    c: Equal(g11,g6)
    c: PointOnObject(g6,g1)
    c: PointOnObject(g7,g1)
    c: PointOnObject(g8,g1)
    c: PointOnObject(g9,g2)
    c: PointOnObject(g10,g2)
    c: PointOnObject(g11,g2)
FEATURE [PartDesign::Pocket] Pocket010
  BaseFeature = -> Fillet004
  Direction = (0,1,-2e-16)
  Length = 7
  Length2 = 5
  Placement = pos=(0,0,0) rot=(1,0,0;1.5708rad)
  Profile = -> Sketch015
  ReferenceAxis = -> Sketch015 [N_Axis]
  Suppressed = false
  Type = 0
FEATURE [PartDesign::Fillet] Fillet005
  Base = -> Pocket010 [Edge112,Edge114,Edge111,Edge113]
  BaseFeature = -> Pocket010
  Placement = pos=(0,0,0) rot=(1,0,0;1.5708rad)
  Radius = 2
  SupportTransform = false
  Suppressed = false
  UseAllEdges = false
FEATURE [PartDesign::Body] Body001  label="Front"
  AllowCompound = false
  Group = -> [Sketch002,Pad001,Sketch010,Pocket006,Hole001,Sketch011,Pocket007,Fillet004,Sketch015,Pocket010,Fillet005]
  Origin = -> Origin001
  Tip = -> Fillet005
FEATURE [PartDesign::Fillet] Fillet006
  Base = -> Pocket005 [Edge3,Edge7,Edge2]
  BaseFeature = -> Pocket005
  Placement = pos=(0,0,0) rot=(1,0,0;1.5708rad)
  Radius = 2
  SupportTransform = false
  Suppressed = false
  UseAllEdges = false
FEATURE [PartDesign::Body] Body002  label="SideV1"
  AllowCompound = false
  Group = -> [Sketch004,Pad002,Sketch005,Pocket001,Sketch006,Pocket002,Sketch007,Pocket003,Hole,Sketch008,Pocket004,Sketch009,Pocket005,Fillet006]
  Origin = -> Origin002
  Placement = pos=(0,140,0) rot=(0,0,1;0rad)
  Tip = -> Fillet006
FEATURE [PartDesign::Fillet] Fillet007
  Base = -> Pocket009 [Edge5,Edge8,Edge1,Edge2]
  BaseFeature = -> Pocket009
  Placement = pos=(0,0,0) rot=(1,0,0;1.5708rad)
  Radius = 2
  SupportTransform = false
  Suppressed = false
  UseAllEdges = false
FEATURE [PartDesign::Body] Body003  label="Back"
  AllowCompound = false
  Group = -> [Sketch012,Pad003,Sketch013,Pocket008,Hole002,Sketch014,Pocket009,Fillet007]
  Origin = -> Origin003
  Placement = pos=(123,140,0) rot=(0,0,1;3.14159rad)
  Tip = -> Fillet007
FEATURE [Sketcher::SketchObject] Sketch016
  ArcFitTolerance = 1e-06
  AttachmentSupport = -> [XZ_Plane004]
  FullyConstrained = false
  MakeInternals = false
  MapMode = 5
  Placement = pos=(0,0,0) rot=(1,0,0;1.5708rad)
  sketch-geometry (73):
    g0: LineSegment [constr] StartX=0 StartY=0 StartZ=0 EndX=123 EndY=0 EndZ=0
    g1: LineSegment StartX=123 StartY=0 StartZ=0 EndX=123 EndY=105 EndZ=0
    g2: LineSegment StartX=123 StartY=105 StartZ=0 EndX=0 EndY=105 EndZ=0
    g3: LineSegment StartX=9 StartY=5 StartZ=0 EndX=114 EndY=5 EndZ=0
    g4: LineSegment StartX=114 StartY=100 StartZ=0 EndX=9 EndY=100 EndZ=0
    g5: LineSegment [constr] StartX=190.257 StartY=65.8 StartZ=0 EndX=190.257 EndY=40.4 EndZ=0
    g6: LineSegment [constr] StartX=190.257 StartY=40.4 StartZ=0 EndX=291.857 EndY=40.4 EndZ=0
    g7: LineSegment [constr] StartX=291.857 StartY=40.4 StartZ=0 EndX=291.857 EndY=65.8 EndZ=0
    g8: LineSegment [constr] StartX=291.857 StartY=65.8 StartZ=0 EndX=190.257 EndY=65.8 EndZ=0
    g9: LineSegment [constr] StartX=184.257 StartY=52.4 StartZ=0 EndX=184.257 EndY=40.4 EndZ=0
    g10: LineSegment [constr] StartX=184.257 StartY=40.4 StartZ=0 EndX=190.257 EndY=40.4 EndZ=0
    g11: LineSegment [constr] StartX=190.257 StartY=40.4 StartZ=0 EndX=190.257 EndY=52.4 EndZ=0
    g12: LineSegment [constr] StartX=190.257 StartY=52.4 StartZ=0 EndX=184.257 EndY=52.4 EndZ=0
    g13: LineSegment [constr] StartX=291.857 StartY=52.4 StartZ=0 EndX=291.857 EndY=40.4 EndZ=0
    g14: LineSegment [constr] StartX=291.857 StartY=40.4 StartZ=0 EndX=297.857 EndY=40.4 EndZ=0
    g15: LineSegment [constr] StartX=297.857 StartY=40.4 StartZ=0 EndX=297.857 EndY=52.4 EndZ=0
    g16: LineSegment [constr] StartX=297.857 StartY=52.4 StartZ=0 EndX=291.857 EndY=52.4 EndZ=0
    g17: LineSegment [constr] StartX=163.474 StartY=98.2 StartZ=0 EndX=163.474 EndY=72.8 EndZ=0
    g18: LineSegment [constr] StartX=163.474 StartY=72.8 StartZ=0 EndX=265.074 EndY=72.8 EndZ=0
    g19: LineSegment [constr] StartX=265.074 StartY=72.8 StartZ=0 EndX=265.074 EndY=98.2 EndZ=0
    g20: LineSegment [constr] StartX=265.074 StartY=98.2 StartZ=0 EndX=163.474 EndY=98.2 EndZ=0
    g21: LineSegment [constr] StartX=157.474 StartY=84.8 StartZ=0 EndX=157.474 EndY=72.8 EndZ=0
    g22: LineSegment [constr] StartX=157.474 StartY=72.8 StartZ=0 EndX=163.474 EndY=72.8 EndZ=0
    g23: LineSegment [constr] StartX=163.474 StartY=72.8 StartZ=0 EndX=163.474 EndY=84.8 EndZ=0
    g24: LineSegment [constr] StartX=163.474 StartY=84.8 StartZ=0 EndX=157.474 EndY=84.8 EndZ=0
    g25: LineSegment [constr] StartX=265.074 StartY=84.8 StartZ=0 EndX=265.074 EndY=72.8 EndZ=0
    g26: LineSegment [constr] StartX=265.074 StartY=72.8 StartZ=0 EndX=271.074 EndY=72.8 EndZ=0
    g27: LineSegment [constr] StartX=271.074 StartY=72.8 StartZ=0 EndX=271.074 EndY=84.8 EndZ=0
    g28: LineSegment [constr] StartX=271.074 StartY=84.8 StartZ=0 EndX=265.074 EndY=84.8 EndZ=0
    g29: LineSegment [constr] StartX=208.539 StartY=33.4 StartZ=0 EndX=208.539 EndY=8 EndZ=0
    g30: LineSegment [constr] StartX=208.539 StartY=8 StartZ=0 EndX=310.139 EndY=8 EndZ=0
    g31: LineSegment [constr] StartX=310.139 StartY=8 StartZ=0 EndX=310.139 EndY=33.4 EndZ=0
    g32: LineSegment [constr] StartX=310.139 StartY=33.4 StartZ=0 EndX=208.539 EndY=33.4 EndZ=0
    g33: LineSegment [constr] StartX=202.539 StartY=20 StartZ=0 EndX=202.539 EndY=8 EndZ=0
    g34: LineSegment [constr] StartX=202.539 StartY=8 StartZ=0 EndX=208.539 EndY=8 EndZ=0
    g35: LineSegment [constr] StartX=208.539 StartY=8 StartZ=0 EndX=208.539 EndY=20 EndZ=0
    g36: LineSegment [constr] StartX=208.539 StartY=20 StartZ=0 EndX=202.539 EndY=20 EndZ=0
    g37: LineSegment [constr] StartX=310.139 StartY=20 StartZ=0 EndX=310.139 EndY=8 EndZ=0
    g38: LineSegment [constr] StartX=310.139 StartY=8 StartZ=0 EndX=316.139 EndY=8 EndZ=0
    g39: LineSegment [constr] StartX=316.139 StartY=8 StartZ=0 EndX=316.139 EndY=20 EndZ=0
    g40: LineSegment [constr] StartX=316.139 StartY=20 StartZ=0 EndX=310.139 EndY=20 EndZ=0
    g41: LineSegment StartX=0 StartY=0 StartZ=0 EndX=123 EndY=0 EndZ=0
    g42: LineSegment [constr] StartX=9 StartY=177.265 StartZ=0 EndX=9 EndY=-72.0652 EndZ=0
    g43: LineSegment [constr] StartX=114 StartY=141.11 StartZ=0 EndX=114 EndY=26.7674 EndZ=0
    g44: LineSegment StartX=9 StartY=100 StartZ=0 EndX=9 EndY=84.9 EndZ=0
    g45: LineSegment StartX=9 StartY=84.9 StartZ=0 EndX=8 EndY=84.9 EndZ=0
    g46: LineSegment StartX=8 StartY=84.9 StartZ=0 EndX=8 EndY=72.6 EndZ=0
    g47: LineSegment StartX=8 StartY=72.6 StartZ=0 EndX=9 EndY=72.6 EndZ=0
    g48: LineSegment StartX=9 StartY=72.6 StartZ=0 EndX=9 EndY=52.6 EndZ=0
    g49: LineSegment StartX=9 StartY=52.6 StartZ=0 EndX=8 EndY=52.6 EndZ=0
    g50: LineSegment StartX=8 StartY=52.6 StartZ=0 EndX=8 EndY=40.3 EndZ=0
    g51: LineSegment StartX=8 StartY=40.3 StartZ=0 EndX=9 EndY=40.3 EndZ=0
    g52: LineSegment StartX=9 StartY=40.3 StartZ=0 EndX=9 EndY=20.3 EndZ=0
    g53: LineSegment StartX=9 StartY=20.3 StartZ=0 EndX=8 EndY=20.3 EndZ=0
    g54: LineSegment StartX=8 StartY=20.3 StartZ=0 EndX=8 EndY=8 EndZ=0
    g55: LineSegment StartX=8 StartY=8 StartZ=0 EndX=9 EndY=8 EndZ=0
    g56: LineSegment StartX=9 StartY=8 StartZ=0 EndX=9 EndY=5 EndZ=0
    g57: LineSegment [constr] StartX=8 StartY=110.102 StartZ=0 EndX=8 EndY=-9.82312 EndZ=0
    g58: LineSegment StartX=114 StartY=100 StartZ=0 EndX=114 EndY=84.9 EndZ=0
    g59: LineSegment StartX=114 StartY=84.9 StartZ=0 EndX=115 EndY=84.9 EndZ=0
    g60: LineSegment StartX=115 StartY=84.9 StartZ=0 EndX=115 EndY=72.6 EndZ=0
    g61: LineSegment StartX=115 StartY=72.6 StartZ=0 EndX=114 EndY=72.6 EndZ=0
    g62: LineSegment StartX=114 StartY=72.6 StartZ=0 EndX=114 EndY=52.6 EndZ=0
    g63: LineSegment StartX=114 StartY=52.6 StartZ=0 EndX=115 EndY=52.6 EndZ=0
    g64: LineSegment StartX=115 StartY=52.6 StartZ=0 EndX=115 EndY=40.3 EndZ=0
    g65: LineSegment StartX=115 StartY=40.3 StartZ=0 EndX=114 EndY=40.3 EndZ=0
    g66: LineSegment StartX=114 StartY=40.3 StartZ=0 EndX=114 EndY=20.3 EndZ=0
    g67: LineSegment StartX=114 StartY=20.3 StartZ=0 EndX=115 EndY=20.3 EndZ=0
    g68: LineSegment StartX=115 StartY=20.3 StartZ=0 EndX=115 EndY=8 EndZ=0
    g69: LineSegment StartX=115 StartY=8 StartZ=0 EndX=114 EndY=8 EndZ=0
    g70: LineSegment StartX=114 StartY=8 StartZ=0 EndX=114 EndY=5 EndZ=0
    g71: LineSegment [constr] StartX=115 StartY=112.118 StartZ=0 EndX=115 EndY=-16.6316 EndZ=0
    g72: LineSegment StartX=0 StartY=105 StartZ=0 EndX=0 EndY=0 EndZ=0
  constraints (212):
    c: Coincident(g-1,g0)
    c: Horizontal(g0)
    c: Coincident(g0,g1)
    c: Vertical(g1)
    c: Coincident(g1,g2)
    c: PointOnObject(g2,g-2)
    c: Horizontal(g2)
    c: Horizontal(g3)
    c: Horizontal(g4)
    c: Coincident(g5,g6)
    c: Coincident(g6,g7)
    c: Coincident(g7,g8)
    c: Coincident(g8,g5)
    c: Vertical(g5)
    c: Vertical(g7)
    c: Horizontal(g6)
    c: Horizontal(g8)
    c: DistanceX(g8,g8) = 101.6
    c: DistanceY(g7,g7) = 25.4
    c: Coincident(g9,g10)
    c: Coincident(g10,g11)
    c: Coincident(g11,g12)
    c: Coincident(g12,g9)
    c: Vertical(g9)
    c: Vertical(g11)
    c: Horizontal(g10)
    c: Horizontal(g12)
    c: DistanceX(g12,g12) = 6
    c: DistanceY(g11,g11) = 12
    c: PointOnObject(g11,g5)
    c: Coincident(g13,g14)
    c: Coincident(g14,g15)
    c: Coincident(g15,g16)
    c: Coincident(g16,g13)
    c: Vertical(g13)
    c: Vertical(g15)
    c: Horizontal(g14)
    c: Horizontal(g16)
    c: DistanceX(g16,g16) = 6
    c: DistanceY(g15,g15) = 12
    c: PointOnObject(g13,g7)
    c: DistanceY(g5,g10) = 0
    c: DistanceY(g6,g13) = 0
    c: DistanceX(g3,g3) = 105
    c: Coincident(g17,g18)
    c: Coincident(g18,g19)
    c: Coincident(g19,g20)
    c: Coincident(g20,g17)
    c: Vertical(g17)
    c: Vertical(g19)
    c: Horizontal(g18)
    c: Horizontal(g20)
    c: DistanceX(g20,g20) = 101.6
    c: DistanceY(g19,g19) = 25.4
    c: Coincident(g21,g22)
    c: Coincident(g22,g23)
    c: Coincident(g23,g24)
    c: Coincident(g24,g21)
    c: Vertical(g21)
    c: Vertical(g23)
    c: Horizontal(g22)
    c: Horizontal(g24)
    c: DistanceX(g24,g24) = 6
    c: DistanceY(g23,g23) = 12
    c: PointOnObject(g23,g17)
    c: Coincident(g25,g26)
    c: Coincident(g26,g27)
    c: Coincident(g27,g28)
    c: Coincident(g28,g25)
    c: Vertical(g25)
    c: Vertical(g27)
    c: Horizontal(g26)
    c: Horizontal(g28)
    c: DistanceX(g28,g28) = 6
    c: DistanceY(g27,g27) = 12
    c: PointOnObject(g25,g19)
    c: DistanceY(g17,g22) = 0
    c: DistanceY(g18,g25) = 0
    c: Coincident(g29,g30)
    c: Coincident(g30,g31)
    c: Coincident(g31,g32)
    c: Coincident(g32,g29)
    c: Vertical(g29)
    c: Vertical(g31)
    c: Horizontal(g30)
    c: Horizontal(g32)
    c: DistanceX(g32,g32) = 101.6
    c: DistanceY(g31,g31) = 25.4
    c: Coincident(g33,g34)
    c: Coincident(g34,g35)
    c: Coincident(g35,g36)
    c: Coincident(g36,g33)
    c: Vertical(g33)
    c: Vertical(g35)
    c: Horizontal(g34)
    c: Horizontal(g36)
    c: DistanceX(g36,g36) = 6
    c: DistanceY(g35,g35) = 12
    c: PointOnObject(g35,g29)
    c: Coincident(g37,g38)
    c: Coincident(g38,g39)
    c: Coincident(g39,g40)
    c: Coincident(g40,g37)
    c: Vertical(g37)
    c: Vertical(g39)
    c: Horizontal(g38)
    c: Horizontal(g40)
    c: DistanceX(g40,g40) = 6
    c: DistanceY(g39,g39) = 12
    c: PointOnObject(g37,g31)
    c: DistanceY(g29,g34) = 0
    c: DistanceY(g30,g37) = 0
    c: DistanceY(g0,g29) = 8
    c: Distance(g32,g6) = 7
    c: Distance(g8,g18) = 7
    c: DistanceX(g0,g0) = 123
    c: Coincident(g41,g0)
    c: Coincident(g41,g0)
    c: Vertical(g43)
    c: Distance(g0,g43) = 9
    c: DistanceX(g0,g42) = 9
    c: PointOnObject(g3,g42)
    c: PointOnObject(g4,g42)
    c: PointOnObject(g3,g43)
    c: PointOnObject(g4,g43)
    c: Coincident(g4,g44)
    c: PointOnObject(g44,g42)
    c: Coincident(g44,g45)
    c: Horizontal(g45)
    c: Coincident(g45,g46)
    c: Vertical(g46)
    c: Coincident(g46,g47)
    c: PointOnObject(g47,g42)
    c: Horizontal(g47)
    c: Coincident(g47,g48)
    c: Symmetric(g42,g42,g48)
    c: Coincident(g48,g49)
    c: Horizontal(g49)
    c: Coincident(g49,g50)
    c: Vertical(g50)
    c: Coincident(g50,g51)
    c: Horizontal(g51)
    c: Coincident(g51,g52)
    c: Coincident(g52,g53)
    c: Coincident(g53,g54)
    c: Coincident(g54,g55)
    c: PointOnObject(g55,g42)
    c: Horizontal(g55)
    c: Coincident(g55,g56)
    c: Coincident(g56,g3)
    c: PointOnObject(g51,g42)
    c: Vertical(g52)
    c: Vertical(g54)
    c: Vertical(g57)
    c: PointOnObject(g45,g57)
    c: PointOnObject(g49,g57)
    c: PointOnObject(g53,g57)
    c: DistanceY(g50,g50) = 12.3
    c: DistanceY(g46,g46) = 12.3
    c: DistanceY(g54,g54) = 12.3
    c: Horizontal(g53)
    c: Vertical(g42)
    c: DistanceX(g57,g42) = 1
    c: DistanceY(g56,g56) = 3
    c: DistanceY(g52,g52) = 20
    c: DistanceY(g48,g48) = 20
    c: Coincident(g4,g58)
    c: Vertical(g58)
    c: Coincident(g58,g59)
    c: Horizontal(g59)
    c: Coincident(g59,g60)
    c: Coincident(g60,g61)
    c: Coincident(g61,g62)
    c: Coincident(g62,g63)
    c: Horizontal(g63)
    c: Coincident(g63,g64)
    c: Vertical(g64)
    c: Coincident(g64,g65)
    c: Horizontal(g65)
    c: Coincident(g65,g66)
    c: Vertical(g66)
    c: Coincident(g66,g67)
    c: Horizontal(g67)
    c: Coincident(g67,g68)
    c: Vertical(g68)
    c: Coincident(g68,g69)
    c: Horizontal(g69)
    c: Coincident(g69,g70)
    c: Coincident(g70,g3)
    c: PointOnObject(g62,g43)
    c: Vertical(g62)
    c: PointOnObject(g65,g43)
    c: Vertical(g60)
    c: Horizontal(g61)
    c: Vertical(g71)
    c: PointOnObject(g60,g71)
    c: PointOnObject(g64,g71)
    c: Vertical(g70)
    c: PointOnObject(g67,g71)
    c: DistanceY(g64,g64) = 12.3
    c: DistanceY(g60,g60) = 12.3
    c: DistanceY(g68,g68) = 12.3
    c: DistanceY(g66,g66) = 20
    c: DistanceY(g62,g62) = 20
    c: DistanceX(g43,g71) = 1
    c: Coincident(g2,g72)
    c: Coincident(g72,g0)
    c: DistanceY(g4,g1) = 5
    c: DistanceY(g17,g4) = 1.8
    c: DistanceY(g0,g3) = 5
    c: DistanceY(g3,g69) = 3
    c: DistanceY(g72,g72) = 105
FEATURE [PartDesign::Pad] Pad004
  Direction = (0,-1,2e-16)
  Length = 15
  Length2 = 10
  Placement = pos=(0,0,0) rot=(1,0,0;1.5708rad)
  Profile = -> Sketch016
  ReferenceAxis = -> Sketch016 [N_Axis]
  Suppressed = false
  Type = 0
FEATURE [Sketcher::SketchObject] Sketch017
  ArcFitTolerance = 1e-06
  AttachmentSupport = -> [Pad004]
  FullyConstrained = false
  MakeInternals = false
  MapMode = 5
  Placement = pos=(0,-15,0) rot=(1,0,0;1.5708rad)
  sketch-geometry (9):
    g0: LineSegment [constr] StartX=118.5 StartY=132.158 StartZ=0 EndX=118.5 EndY=-19.1161 EndZ=0
    g1: LineSegment [constr] StartX=4.5 StartY=125.192 StartZ=0 EndX=4.5 EndY=-14.1399 EndZ=0
    g2: LineSegment [constr] StartX=123 StartY=132.755 StartZ=0 EndX=123 EndY=-31.2578 EndZ=0
    g3: LineSegment [constr] StartX=-16.8458 StartY=99 StartZ=0 EndX=200.114 EndY=99 EndZ=0
    g4: LineSegment [constr] StartX=159.309 StartY=67 StartZ=0 EndX=-18.2391 EndY=67 EndZ=0
    g5: LineSegment [constr] StartX=16.0716 StartY=35 StartZ=0 EndX=220.928 EndY=35 EndZ=0
    g6: Circle CenterX=4.5 CenterY=99 CenterZ=0 NormalX=0 NormalY=0 NormalZ=1 AngleXU=0 Radius=2
    g7: Circle CenterX=4.5 CenterY=67 CenterZ=0 NormalX=0 NormalY=0 NormalZ=1 AngleXU=0 Radius=2
    g8: Circle CenterX=4.5 CenterY=35 CenterZ=0 NormalX=0 NormalY=0 NormalZ=1 AngleXU=0 Radius=2
  constraints (21):
    c: Vertical(g0)
    c: Vertical(g1)
    c: Vertical(g2)
    c: Distance(g2,g-2) = 123
    c: Distance(g0,g2) = 4.5
    c: Distance(g-2,g1) = 4.5
    c: Horizontal(g3)
    c: Horizontal(g4)
    c: Horizontal(g5)
    c: Distance(g-1,g5) = 35
    c: Distance(g5,g4) = 32
    c: Distance(g4,g3) = 32
    c: PointOnObject(g6,g3)
    c: PointOnObject(g6,g1)
    c: Diameter(g6) = 4
    c: PointOnObject(g7,g4)
    c: PointOnObject(g8,g5)
    c: Equal(g7,g6)
    c: Equal(g6,g8)
    c: PointOnObject(g7,g1)
    c: PointOnObject(g8,g1)
FEATURE [PartDesign::Pocket] Pocket011
  BaseFeature = -> Pad004
  Direction = (0,1,-2e-16)
  Length = 5
  Length2 = 5
  Placement = pos=(0,0,0) rot=(1,0,0;1.5708rad)
  Profile = -> Sketch017
  ReferenceAxis = -> Sketch017 [N_Axis]
  Suppressed = false
  Type = 1
FEATURE [Sketcher::SketchObject] Sketch018
  ArcFitTolerance = 1e-06
  FullyConstrained = false
  MakeInternals = false
  MapMode = 5
  Placement = pos=(0,-15,0) rot=(1,0,0;1.5708rad)
  sketch-geometry (5):
    g0: LineSegment [constr] StartX=123 StartY=114.172 StartZ=0 EndX=123 EndY=-10.073 EndZ=0
    g1: LineSegment [constr] StartX=118.5 StartY=117.112 StartZ=0 EndX=118.5 EndY=-11.479 EndZ=0
    g2: Circle CenterX=118.5 CenterY=90 CenterZ=0 NormalX=0 NormalY=0 NormalZ=1 AngleXU=0 Radius=1.5
    g3: Circle CenterX=118.5 CenterY=58 CenterZ=0 NormalX=0 NormalY=0 NormalZ=1 AngleXU=0 Radius=1.5
    g4: Circle CenterX=118.5 CenterY=26 CenterZ=0 NormalX=0 NormalY=0 NormalZ=1 AngleXU=0 Radius=1.5
  constraints (13):
    c: Vertical(g0)
    c: DistanceX(g-1,g0) = 123
    c: Vertical(g1)
    c: Distance(g1,g0) = 4.5
    c: PointOnObject(g2,g1)
    c: PointOnObject(g3,g1)
    c: PointOnObject(g4,g1)
    c: Diameter(g2) = 3
    c: Equal(g3,g2)
    c: Equal(g4,g2)
    c: Distance(g4,g-1) = 26
    c: DistanceY(g4,g3) = 32
    c: DistanceY(g3,g2) = 32
FEATURE [PartDesign::Pocket] Pocket012
  BaseFeature = -> Pocket011
  Direction = (0,1,-2e-16)
  Length = 7
  Length2 = 5
  Placement = pos=(0,0,0) rot=(1,0,0;1.5708rad)
  Profile = -> Sketch018
  ReferenceAxis = -> Sketch018 [N_Axis]
  Suppressed = false
  Type = 0
FEATURE [PartDesign::Hole] Hole003
  BaseFeature = -> Pocket012
  CustomThreadClearance = 0
  Depth = 4
  DepthType = 0
  Diameter = 6.5
  DrillForDepth = false
  DrillPoint = 1
  DrillPointAngle = 118
  HoleCutCountersinkAngle = 90
  HoleCutCustomValues = false
  HoleCutDepth = 0
  HoleCutDiameter = 0
  HoleCutType = 0
  ModelThread = false
  Placement = pos=(0,0,0) rot=(1,0,0;1.5708rad)
  Profile = -> Pocket012 [Edge46,Edge45,Edge44]
  Reversed = true
  Suppressed = false
  Tapered = false
  TaperedAngle = 90
  ThreadClass = 0
  ThreadDepth = 4
  ThreadDepthType = 0
  ThreadDirection = 0
  ThreadFit = 0
  ThreadSize = 0
  ThreadType = 0
  Threaded = false
  UseCustomThreadClearance = false
FEATURE [Sketcher::SketchObject] Sketch019
  ArcFitTolerance = 1e-06
  AttachmentSupport = -> [Hole003]
  FullyConstrained = false
  MakeInternals = false
  MapMode = 5
  Placement = pos=(123,0,0) rot=(0.707107,0,0.707107;3.14159rad)
  sketch-geometry (4):
    g0: LineSegment StartX=-19.7729 StartY=-14.1652 StartZ=0 EndX=141.281 EndY=-14.1652 EndZ=0
    g1: LineSegment StartX=141.281 StartY=-14.1652 StartZ=0 EndX=141.281 EndY=12.7235 EndZ=0
    g2: LineSegment StartX=141.281 StartY=12.7235 StartZ=0 EndX=-19.7729 EndY=12.7235 EndZ=0
    g3: LineSegment StartX=-19.7729 StartY=12.7235 StartZ=0 EndX=-19.7729 EndY=-14.1652 EndZ=0
  constraints (8):
    c: Coincident(g0,g1)
    c: Coincident(g1,g2)
    c: Coincident(g2,g3)
    c: Coincident(g3,g0)
    c: Horizontal(g0)
    c: Horizontal(g2)
    c: Vertical(g1)
    c: Vertical(g3)
FEATURE [PartDesign::Pocket] Pocket013
  BaseFeature = -> Hole003
  Direction = (-1,0,2e-16)
  Length = 114
  Length2 = 5
  Placement = pos=(0,0,0) rot=(1,0,0;1.5708rad)
  Profile = -> Sketch019
  ReferenceAxis = -> Sketch019 [N_Axis]
  Suppressed = false
  Type = 0
FEATURE [PartDesign::Body] Body004  label="BackTemplate"
  AllowCompound = false
  Group = -> [Sketch016,Pad004,Sketch017,Pocket011,Sketch018,Pocket012,Hole003,Sketch019,Pocket013]
  Origin = -> Origin004
  Placement = pos=(123,140,0) rot=(0,0,1;3.14159rad)
  Tip = -> Pocket013
FEATURE [Sketcher::SketchObject] Sketch020
  ArcFitTolerance = 1e-06
  AttachmentSupport = -> [XZ_Plane005]
  FullyConstrained = false
  MakeInternals = false
  MapMode = 5
  Placement = pos=(0,0,0) rot=(1,0,0;1.5708rad)
  sketch-geometry (10):
    g0: LineSegment [constr] StartX=0 StartY=0 StartZ=0 EndX=119 EndY=0 EndZ=0
    g1: LineSegment StartX=119 StartY=0 StartZ=0 EndX=119 EndY=105 EndZ=0
    g2: LineSegment StartX=119 StartY=105 StartZ=0 EndX=0 EndY=105 EndZ=0
    g3: LineSegment StartX=8 StartY=15 StartZ=0 EndX=111 EndY=15 EndZ=0
    g4: LineSegment StartX=111 StartY=90 StartZ=0 EndX=8 EndY=90 EndZ=0
    g5: LineSegment StartX=0 StartY=0 StartZ=0 EndX=119 EndY=0 EndZ=0
    g6: LineSegment [constr] StartX=8 StartY=177.265 StartZ=0 EndX=8 EndY=-72.0652 EndZ=0
    g7: LineSegment StartX=0 StartY=105 StartZ=0 EndX=0 EndY=0 EndZ=0
    g8: LineSegment StartX=8 StartY=90 StartZ=0 EndX=8 EndY=15 EndZ=0
    g9: LineSegment StartX=111 StartY=90 StartZ=0 EndX=111 EndY=15 EndZ=0
  constraints (28):
    c: Coincident(g-1,g0)
    c: Horizontal(g0)
    c: Coincident(g0,g1)
    c: Vertical(g1)
    c: Coincident(g1,g2)
    c: PointOnObject(g2,g-2)
    c: Horizontal(g2)
    c: Horizontal(g3)
    c: Horizontal(g4)
    c: DistanceX(g3,g3) = 103
    c: DistanceX(g0,g0) = 119
    c: Coincident(g5,g0)
    c: Coincident(g5,g0)
    c: DistanceX(g0,g6) = 8
    c: PointOnObject(g3,g6)
    c: PointOnObject(g4,g6)
    c: Vertical(g6)
    c: Coincident(g2,g7)
    c: Coincident(g7,g0)
    c: DistanceY(g4,g1) = 15
    c: DistanceY(g0,g3) = 15
    c: DistanceY(g7,g7) = 105
    c: Coincident(g8,g4)
    c: Coincident(g8,g3)
    c: Coincident(g9,g4)
    c: Coincident(g9,g3)
    c: Vertical(g9)
    c: DistanceX(g4,g1) = 8
FEATURE [PartDesign::Pad] Pad005
  Direction = (0,-1,2e-16)
  Length = 15
  Length2 = 12
  Placement = pos=(0,0,0) rot=(1,0,0;1.5708rad)
  Profile = -> Sketch020
  ReferenceAxis = -> Sketch020 [N_Axis]
  Suppressed = false
  Type = 4
FEATURE [Sketcher::SketchObject] Sketch021
  ArcFitTolerance = 1e-06
  AttachmentSupport = -> [Pad005]
  FullyConstrained = false
  MakeInternals = false
  MapMode = 5
  Placement = pos=(0,-15,0) rot=(1,0,0;1.5708rad)
  sketch-geometry (16):
    g0: LineSegment [constr] StartX=115 StartY=132.158 StartZ=0 EndX=115 EndY=-19.1161 EndZ=0
    g1: LineSegment [constr] StartX=4 StartY=125.192 StartZ=0 EndX=4 EndY=-14.1399 EndZ=0
    g2: LineSegment [constr] StartX=119 StartY=132.755 StartZ=0 EndX=119 EndY=-31.2578 EndZ=0
    g3: LineSegment [constr] StartX=-16.8458 StartY=99 StartZ=0 EndX=200.114 EndY=99 EndZ=0
    g4: LineSegment [constr] StartX=159.309 StartY=67 StartZ=0 EndX=-18.2391 EndY=67 EndZ=0
    g5: LineSegment [constr] StartX=-17.8692 StartY=35 StartZ=0 EndX=186.988 EndY=35 EndZ=0
    g6: Circle CenterX=4 CenterY=99 CenterZ=0 NormalX=0 NormalY=0 NormalZ=1 AngleXU=0 Radius=2
    g7: Circle CenterX=4 CenterY=67 CenterZ=0 NormalX=0 NormalY=0 NormalZ=1 AngleXU=0 Radius=2
    g8: Circle CenterX=4 CenterY=35 CenterZ=0 NormalX=0 NormalY=0 NormalZ=1 AngleXU=0 Radius=2
    g9: Circle CenterX=115 CenterY=99 CenterZ=0 NormalX=0 NormalY=0 NormalZ=1 AngleXU=0 Radius=2
    g10: Circle CenterX=4 CenterY=4 CenterZ=0 NormalX=0 NormalY=0 NormalZ=1 AngleXU=0 Radius=2
    g11: LineSegment [constr] StartX=-10.5271 StartY=4 StartZ=0 EndX=156.661 EndY=4 EndZ=0
    g12: Circle CenterX=115 CenterY=4 CenterZ=0 NormalX=0 NormalY=0 NormalZ=1 AngleXU=0 Radius=2
    g13: Circle [constr] CenterX=108 CenterY=99 CenterZ=0 NormalX=0 NormalY=0 NormalZ=1 AngleXU=0 Radius=2.25
    g14: Circle [constr] CenterX=108 CenterY=4 CenterZ=0 NormalX=0 NormalY=0 NormalZ=1 AngleXU=0 Radius=2.25
    g15: LineSegment [constr] StartX=108 StartY=116.17 StartZ=0 EndX=108 EndY=-2.21069 EndZ=0
  constraints (41):
    c: Vertical(g0)
    c: Vertical(g1)
    c: Vertical(g2)
    c: Distance(g2,g-2) = 119
    c: Distance(g0,g2) = 4
    c: Distance(g-2,g1) = 4
    c: Horizontal(g3)
    c: Horizontal(g4)
    c: Horizontal(g5)
    c: Distance(g5,g4) = 32
    c: Distance(g4,g3) = 32
    c: PointOnObject(g6,g3)
    c: PointOnObject(g6,g1)
    c: Diameter(g6) = 4
    c: PointOnObject(g7,g4)
    c: PointOnObject(g8,g5)
    c: PointOnObject(g9,g3)
    c: Equal(g7,g6)
    c: Equal(g6,g8)
    c: Equal(g9,g6)
    c: PointOnObject(g7,g1)
    c: PointOnObject(g8,g1)
    c: PointOnObject(g9,g0)
    c: PointOnObject(g10,g1)
    c: Equal(g10,g6)
    c: Horizontal(g11)
    c: PointOnObject(g10,g11)
    c: PointOnObject(g12,g0)
    c: Equal(g12,g6)
    c: PointOnObject(g12,g11)
    c: PointOnObject(g13,g3)
    c: PointOnObject(g14,g11)
    c: Equal(g14,g13)
    c: Vertical(g15)
    c: PointOnObject(g14,g15)
    c: PointOnObject(g13,g15)
    c: Distance(g13,g-2) = 108
    c: DistanceY(g-1,g13) = 99
    c: DistanceY(g-1,g5) = 35
    c: Distance(g5,g11) = 31
    c: DistanceX(g13,g0) = 7
FEATURE [PartDesign::Pocket] Pocket014
  BaseFeature = -> Pad005
  Direction = (0,1,-2e-16)
  Length = 5
  Length2 = 5
  Placement = pos=(0,0,0) rot=(1,0,0;1.5708rad)
  Profile = -> Sketch021
  ReferenceAxis = -> Sketch021 [N_Axis]
  Suppressed = false
  Type = 1
FEATURE [Sketcher::SketchObject] Sketch022
  ArcFitTolerance = 1e-06
  AttachmentSupport = -> [Pocket014]
  FullyConstrained = false
  MakeInternals = false
  MapMode = 5
  Placement = pos=(0,4.62e-14,105) rot=(0,0,1;3.14159rad)
  sketch-geometry (4):
    g0: LineSegment StartX=-70 StartY=0 StartZ=0 EndX=-70 EndY=-24.7514 EndZ=0
    g1: LineSegment StartX=-70 StartY=-24.7514 StartZ=0 EndX=20.744 EndY=-24.7514 EndZ=0
    g2: LineSegment StartX=20.744 StartY=-24.7514 StartZ=0 EndX=20.744 EndY=0 EndZ=0
    g3: LineSegment StartX=20.744 StartY=0 StartZ=0 EndX=-70 EndY=0 EndZ=0
  constraints (10):
    c: Coincident(g0,g1)
    c: Coincident(g1,g2)
    c: Coincident(g2,g3)
    c: Coincident(g3,g0)
    c: Vertical(g0)
    c: Vertical(g2)
    c: Horizontal(g1)
    c: Horizontal(g3)
    c: PointOnObject(g0,g-1)
    c: Distance(g-1,g0) = 70
FEATURE [PartDesign::Pocket] Pocket015
  BaseFeature = -> Pocket014
  Direction = (0,0,-1)
  Length = 5
  Length2 = 5
  Placement = pos=(0,0,0) rot=(1,0,0;1.5708rad)
  Profile = -> Sketch022
  ReferenceAxis = -> Sketch022 [N_Axis]
  Suppressed = false
  Type = 1
FEATURE [Sketcher::SketchObject] Sketch023
  ArcFitTolerance = 1e-06
  AttachmentSupport = -> [Pocket015]
  FullyConstrained = false
  MakeInternals = false
  MapMode = 5
  Placement = pos=(119,0,0) rot=(0.707107,0,0.707107;3.14159rad)
  sketch-geometry (6):
    g0: LineSegment StartX=10 StartY=-21.0217 StartZ=0 EndX=95 EndY=-21.0217 EndZ=0
    g1: LineSegment StartX=95 StartY=-21.0217 StartZ=0 EndX=95 EndY=10 EndZ=0
    g2: LineSegment StartX=95 StartY=10 StartZ=0 EndX=10 EndY=10 EndZ=0
    g3: LineSegment StartX=10 StartY=10 StartZ=0 EndX=10 EndY=-21.0217 EndZ=0
    g4: LineSegment [constr] StartX=-8.75085 StartY=15 StartZ=0 EndX=136.896 EndY=15 EndZ=0
    g5: LineSegment [constr] StartX=105 StartY=30.135 StartZ=0 EndX=105 EndY=-23.4946 EndZ=0
  constraints (15):
    c: Coincident(g0,g1)
    c: Coincident(g1,g2)
    c: Coincident(g2,g3)
    c: Coincident(g3,g0)
    c: Horizontal(g0)
    c: Horizontal(g2)
    c: Vertical(g1)
    c: Vertical(g3)
    c: Horizontal(g4)
    c: DistanceY(g-1,g4) = 15
    c: DistanceY(g-1,g2) = 10
    c: DistanceX(g-1,g2) = 10
    c: Vertical(g5)
    c: DistanceX(g-1,g5) = 105
    c: DistanceX(g1,g5) = 10
FEATURE [PartDesign::Pocket] Pocket016
  BaseFeature = -> Pocket015
  Direction = (-1,0,2e-16)
  Length = 111
  Length2 = 5
  Placement = pos=(0,0,0) rot=(1,0,0;1.5708rad)
  Profile = -> Sketch023
  ReferenceAxis = -> Sketch023 [N_Axis]
  Suppressed = false
  Type = 0
FEATURE [Sketcher::SketchObject] Sketch024
  ArcFitTolerance = 1e-06
  AttachmentSupport = -> [Pocket015]
  FullyConstrained = false
  MakeInternals = false
  MapMode = 5
  Placement = pos=(0,12,0) rot=(-1,0,0;1.5708rad)
  sketch-geometry (7):
    g0: LineSegment StartX=8 StartY=-5 StartZ=0 EndX=8 EndY=-100 EndZ=0
    g1: LineSegment StartX=8 StartY=-100 StartZ=0 EndX=111 EndY=-100 EndZ=0
    g2: LineSegment StartX=111 StartY=-100 StartZ=0 EndX=111 EndY=-5 EndZ=0
    g3: LineSegment StartX=111 StartY=-5 StartZ=0 EndX=8 EndY=-5 EndZ=0
    g4: LineSegment [constr] StartX=-9.73418 StartY=-105 StartZ=0 EndX=147.848 EndY=-105 EndZ=0
    g5: LineSegment [constr] StartX=8 StartY=7.3796 StartZ=0 EndX=8 EndY=-122.229 EndZ=0
    g6: LineSegment [constr] StartX=119 StartY=24.0612 StartZ=0 EndX=119 EndY=-121.799 EndZ=0
  constraints (19):
    c: Coincident(g0,g1)
    c: Coincident(g1,g2)
    c: Coincident(g2,g3)
    c: Coincident(g3,g0)
    c: Vertical(g0)
    c: Vertical(g2)
    c: Horizontal(g1)
    c: Horizontal(g3)
    c: DistanceY(g0,g-1) = 5
    c: Horizontal(g4)
    c: Distance(g-1,g4) = 105
    c: Distance(g1,g4) = 5
    c: Vertical(g5)
    c: DistanceX(g-1,g5) = 8
    c: PointOnObject(g0,g5)
    c: DistanceX(g3,g3) = 103
    c: Vertical(g6)
    c: Distance(g-1,g6) = 119
    c: DistanceX(g2,g6) = 8
FEATURE [PartDesign::Pocket] Pocket017
  BaseFeature = -> Pocket016
  Direction = (0,-1,-2e-16)
  Length = 17
  Length2 = 5
  Placement = pos=(0,0,0) rot=(1,0,0;1.5708rad)
  Profile = -> Sketch024
  ReferenceAxis = -> Sketch024 [N_Axis]
  Suppressed = false
  Type = 0
FEATURE [Sketcher::SketchObject] Sketch025
  ArcFitTolerance = 1e-06
  AttachmentSupport = -> [Pocket017]
  FullyConstrained = false
  MakeInternals = false
  MapMode = 5
  Placement = pos=(0,-15,0) rot=(1,0,0;1.5708rad)
  sketch-geometry (5):
    g0: LineSegment [constr] StartX=108 StartY=124.39 StartZ=0 EndX=108 EndY=-25.1728 EndZ=0
    g1: LineSegment [constr] StartX=40.7408 StartY=5 StartZ=0 EndX=175.259 EndY=5 EndZ=0
    g2: LineSegment [constr] StartX=-13.4232 StartY=99 StartZ=0 EndX=157.959 EndY=99 EndZ=0
    g3: Circle CenterX=108 CenterY=99 CenterZ=0 NormalX=0 NormalY=0 NormalZ=1 AngleXU=0 Radius=2.25
    g4: Circle CenterX=108 CenterY=5 CenterZ=0 NormalX=0 NormalY=0 NormalZ=1 AngleXU=0 Radius=2.25
  constraints (12):
    c: Vertical(g0)
    c: Distance(g-1,g0) = 108
    c: Horizontal(g1)
    c: Distance(g-1,g1) = 5
    c: Horizontal(g2)
    c: Distance(g-1,g2) = 99
    c: PointOnObject(g3,g2)
    c: Diameter(g3) = 4.5
    c: Symmetric(g1,g1,g4)
    c: Equal(g4,g3)
    c: PointOnObject(g3,g0)
    c: PointOnObject(g4,g0)
FEATURE [PartDesign::Pocket] Pocket018
  BaseFeature = -> Pocket017
  Direction = (0,1,-2e-16)
  Length = 6
  Length2 = 5
  Placement = pos=(0,0,0) rot=(1,0,0;1.5708rad)
  Profile = -> Sketch025
  ReferenceAxis = -> Sketch025 [N_Axis]
  Suppressed = false
  Type = 0
FEATURE [Sketcher::SketchObject] Sketch026
  ArcFitTolerance = 1e-06
  AttachmentSupport = -> [XZ_Plane006]
  FullyConstrained = false
  MakeInternals = false
  MapMode = 5
  Placement = pos=(0,0,0) rot=(1,0,0;1.5708rad)
  sketch-geometry (73):
    g0: LineSegment [constr] StartX=0 StartY=0 StartZ=0 EndX=122 EndY=0 EndZ=0
    g1: LineSegment StartX=122 StartY=0 StartZ=0 EndX=122 EndY=105 EndZ=0
    g2: LineSegment StartX=122 StartY=105 StartZ=0 EndX=0 EndY=105 EndZ=0
    g3: LineSegment StartX=8 StartY=5 StartZ=0 EndX=113 EndY=5 EndZ=0
    g4: LineSegment StartX=113 StartY=100 StartZ=0 EndX=8 EndY=100 EndZ=0
    g5: LineSegment [constr] StartX=190.257 StartY=65.8 StartZ=0 EndX=190.257 EndY=40.4 EndZ=0
    g6: LineSegment [constr] StartX=190.257 StartY=40.4 StartZ=0 EndX=291.857 EndY=40.4 EndZ=0
    g7: LineSegment [constr] StartX=291.857 StartY=40.4 StartZ=0 EndX=291.857 EndY=65.8 EndZ=0
    g8: LineSegment [constr] StartX=291.857 StartY=65.8 StartZ=0 EndX=190.257 EndY=65.8 EndZ=0
    g9: LineSegment [constr] StartX=184.257 StartY=52.4 StartZ=0 EndX=184.257 EndY=40.4 EndZ=0
    g10: LineSegment [constr] StartX=184.257 StartY=40.4 StartZ=0 EndX=190.257 EndY=40.4 EndZ=0
    g11: LineSegment [constr] StartX=190.257 StartY=40.4 StartZ=0 EndX=190.257 EndY=52.4 EndZ=0
    g12: LineSegment [constr] StartX=190.257 StartY=52.4 StartZ=0 EndX=184.257 EndY=52.4 EndZ=0
    g13: LineSegment [constr] StartX=291.857 StartY=52.4 StartZ=0 EndX=291.857 EndY=40.4 EndZ=0
    g14: LineSegment [constr] StartX=291.857 StartY=40.4 StartZ=0 EndX=297.857 EndY=40.4 EndZ=0
    g15: LineSegment [constr] StartX=297.857 StartY=40.4 StartZ=0 EndX=297.857 EndY=52.4 EndZ=0
    g16: LineSegment [constr] StartX=297.857 StartY=52.4 StartZ=0 EndX=291.857 EndY=52.4 EndZ=0
    g17: LineSegment [constr] StartX=163.474 StartY=98.2 StartZ=0 EndX=163.474 EndY=72.8 EndZ=0
    g18: LineSegment [constr] StartX=163.474 StartY=72.8 StartZ=0 EndX=265.074 EndY=72.8 EndZ=0
    g19: LineSegment [constr] StartX=265.074 StartY=72.8 StartZ=0 EndX=265.074 EndY=98.2 EndZ=0
    g20: LineSegment [constr] StartX=265.074 StartY=98.2 StartZ=0 EndX=163.474 EndY=98.2 EndZ=0
    g21: LineSegment [constr] StartX=157.474 StartY=84.8 StartZ=0 EndX=157.474 EndY=72.8 EndZ=0
    g22: LineSegment [constr] StartX=157.474 StartY=72.8 StartZ=0 EndX=163.474 EndY=72.8 EndZ=0
    g23: LineSegment [constr] StartX=163.474 StartY=72.8 StartZ=0 EndX=163.474 EndY=84.8 EndZ=0
    g24: LineSegment [constr] StartX=163.474 StartY=84.8 StartZ=0 EndX=157.474 EndY=84.8 EndZ=0
    g25: LineSegment [constr] StartX=265.074 StartY=84.8 StartZ=0 EndX=265.074 EndY=72.8 EndZ=0
    g26: LineSegment [constr] StartX=265.074 StartY=72.8 StartZ=0 EndX=271.074 EndY=72.8 EndZ=0
    g27: LineSegment [constr] StartX=271.074 StartY=72.8 StartZ=0 EndX=271.074 EndY=84.8 EndZ=0
    g28: LineSegment [constr] StartX=271.074 StartY=84.8 StartZ=0 EndX=265.074 EndY=84.8 EndZ=0
    g29: LineSegment [constr] StartX=208.539 StartY=33.4 StartZ=0 EndX=208.539 EndY=8 EndZ=0
    g30: LineSegment [constr] StartX=208.539 StartY=8 StartZ=0 EndX=310.139 EndY=8 EndZ=0
    g31: LineSegment [constr] StartX=310.139 StartY=8 StartZ=0 EndX=310.139 EndY=33.4 EndZ=0
    g32: LineSegment [constr] StartX=310.139 StartY=33.4 StartZ=0 EndX=208.539 EndY=33.4 EndZ=0
    g33: LineSegment [constr] StartX=202.539 StartY=20 StartZ=0 EndX=202.539 EndY=8 EndZ=0
    g34: LineSegment [constr] StartX=202.539 StartY=8 StartZ=0 EndX=208.539 EndY=8 EndZ=0
    g35: LineSegment [constr] StartX=208.539 StartY=8 StartZ=0 EndX=208.539 EndY=20 EndZ=0
    g36: LineSegment [constr] StartX=208.539 StartY=20 StartZ=0 EndX=202.539 EndY=20 EndZ=0
    g37: LineSegment [constr] StartX=310.139 StartY=20 StartZ=0 EndX=310.139 EndY=8 EndZ=0
    g38: LineSegment [constr] StartX=310.139 StartY=8 StartZ=0 EndX=316.139 EndY=8 EndZ=0
    g39: LineSegment [constr] StartX=316.139 StartY=8 StartZ=0 EndX=316.139 EndY=20 EndZ=0
    g40: LineSegment [constr] StartX=316.139 StartY=20 StartZ=0 EndX=310.139 EndY=20 EndZ=0
    g41: LineSegment StartX=0 StartY=0 StartZ=0 EndX=122 EndY=0 EndZ=0
    g42: LineSegment [constr] StartX=8 StartY=177.265 StartZ=0 EndX=8 EndY=-72.0652 EndZ=0
    g43: LineSegment [constr] StartX=113 StartY=141.11 StartZ=0 EndX=113 EndY=26.7674 EndZ=0
    g44: LineSegment StartX=8 StartY=100 StartZ=0 EndX=8 EndY=84.9 EndZ=0
    g45: LineSegment StartX=8 StartY=84.9 StartZ=0 EndX=4 EndY=84.9 EndZ=0
    g46: LineSegment StartX=4 StartY=84.9 StartZ=0 EndX=4 EndY=72.6 EndZ=0
    g47: LineSegment StartX=4 StartY=72.6 StartZ=0 EndX=8 EndY=72.6 EndZ=0
    g48: LineSegment StartX=8 StartY=72.6 StartZ=0 EndX=8 EndY=52.6 EndZ=0
    g49: LineSegment StartX=8 StartY=52.6 StartZ=0 EndX=4 EndY=52.6 EndZ=0
    g50: LineSegment StartX=4 StartY=52.6 StartZ=0 EndX=4 EndY=40.3 EndZ=0
    g51: LineSegment StartX=4 StartY=40.3 StartZ=0 EndX=8 EndY=40.3 EndZ=0
    g52: LineSegment StartX=8 StartY=40.3 StartZ=0 EndX=8 EndY=20.3 EndZ=0
    g53: LineSegment StartX=8 StartY=20.3 StartZ=0 EndX=4 EndY=20.3 EndZ=0
    g54: LineSegment StartX=4 StartY=20.3 StartZ=0 EndX=4 EndY=8 EndZ=0
    g55: LineSegment StartX=4 StartY=8 StartZ=0 EndX=8 EndY=8 EndZ=0
    g56: LineSegment StartX=8 StartY=8 StartZ=0 EndX=8 EndY=5 EndZ=0
    g57: LineSegment [constr] StartX=4 StartY=110.102 StartZ=0 EndX=4 EndY=-9.82312 EndZ=0
    g58: LineSegment StartX=113 StartY=100 StartZ=0 EndX=113 EndY=84.9 EndZ=0
    g59: LineSegment StartX=113 StartY=84.9 StartZ=0 EndX=117.5 EndY=84.9 EndZ=0
    g60: LineSegment StartX=117.5 StartY=84.9 StartZ=0 EndX=117.5 EndY=72.6 EndZ=0
    g61: LineSegment StartX=117.5 StartY=72.6 StartZ=0 EndX=113 EndY=72.6 EndZ=0
    g62: LineSegment StartX=113 StartY=72.6 StartZ=0 EndX=113 EndY=52.6 EndZ=0
    g63: LineSegment StartX=113 StartY=52.6 StartZ=0 EndX=117.5 EndY=52.6 EndZ=0
    g64: LineSegment StartX=117.5 StartY=52.6 StartZ=0 EndX=117.5 EndY=40.3 EndZ=0
    g65: LineSegment StartX=117.5 StartY=40.3 StartZ=0 EndX=113 EndY=40.3 EndZ=0
    g66: LineSegment StartX=113 StartY=40.3 StartZ=0 EndX=113 EndY=20.3 EndZ=0
    g67: LineSegment StartX=113 StartY=20.3 StartZ=0 EndX=117.5 EndY=20.3 EndZ=0
    g68: LineSegment StartX=117.5 StartY=20.3 StartZ=0 EndX=117.5 EndY=8 EndZ=0
    g69: LineSegment StartX=117.5 StartY=8 StartZ=0 EndX=113 EndY=8 EndZ=0
    g70: LineSegment StartX=113 StartY=8 StartZ=0 EndX=113 EndY=5 EndZ=0
    g71: LineSegment [constr] StartX=117.5 StartY=131.25 StartZ=0 EndX=117.5 EndY=5.33727 EndZ=0
    g72: LineSegment StartX=0 StartY=105 StartZ=0 EndX=0 EndY=0 EndZ=0
  constraints (212):
    c: Coincident(g-1,g0)
    c: Horizontal(g0)
    c: Coincident(g0,g1)
    c: Vertical(g1)
    c: Coincident(g1,g2)
    c: PointOnObject(g2,g-2)
    c: Horizontal(g2)
    c: Horizontal(g3)
    c: Horizontal(g4)
    c: Coincident(g5,g6)
    c: Coincident(g6,g7)
    c: Coincident(g7,g8)
    c: Coincident(g8,g5)
    c: Vertical(g5)
    c: Vertical(g7)
    c: Horizontal(g6)
    c: Horizontal(g8)
    c: DistanceX(g8,g8) = 101.6
    c: DistanceY(g7,g7) = 25.4
    c: Coincident(g9,g10)
    c: Coincident(g10,g11)
    c: Coincident(g11,g12)
    c: Coincident(g12,g9)
    c: Vertical(g9)
    c: Vertical(g11)
    c: Horizontal(g10)
    c: Horizontal(g12)
    c: DistanceX(g12,g12) = 6
    c: DistanceY(g11,g11) = 12
    c: PointOnObject(g11,g5)
    c: Coincident(g13,g14)
    c: Coincident(g14,g15)
    c: Coincident(g15,g16)
    c: Coincident(g16,g13)
    c: Vertical(g13)
    c: Vertical(g15)
    c: Horizontal(g14)
    c: Horizontal(g16)
    c: DistanceX(g16,g16) = 6
    c: DistanceY(g15,g15) = 12
    c: PointOnObject(g13,g7)
    c: DistanceY(g5,g10) = 0
    c: DistanceY(g6,g13) = 0
    c: DistanceX(g3,g3) = 105
    c: Coincident(g17,g18)
    c: Coincident(g18,g19)
    c: Coincident(g19,g20)
    c: Coincident(g20,g17)
    c: Vertical(g17)
    c: Vertical(g19)
    c: Horizontal(g18)
    c: Horizontal(g20)
    c: DistanceX(g20,g20) = 101.6
    c: DistanceY(g19,g19) = 25.4
    c: Coincident(g21,g22)
    c: Coincident(g22,g23)
    c: Coincident(g23,g24)
    c: Coincident(g24,g21)
    c: Vertical(g21)
    c: Vertical(g23)
    c: Horizontal(g22)
    c: Horizontal(g24)
    c: DistanceX(g24,g24) = 6
    c: DistanceY(g23,g23) = 12
    c: PointOnObject(g23,g17)
    c: Coincident(g25,g26)
    c: Coincident(g26,g27)
    c: Coincident(g27,g28)
    c: Coincident(g28,g25)
    c: Vertical(g25)
    c: Vertical(g27)
    c: Horizontal(g26)
    c: Horizontal(g28)
    c: DistanceX(g28,g28) = 6
    c: DistanceY(g27,g27) = 12
    c: PointOnObject(g25,g19)
    c: DistanceY(g17,g22) = 0
    c: DistanceY(g18,g25) = 0
    c: Coincident(g29,g30)
    c: Coincident(g30,g31)
    c: Coincident(g31,g32)
    c: Coincident(g32,g29)
    c: Vertical(g29)
    c: Vertical(g31)
    c: Horizontal(g30)
    c: Horizontal(g32)
    c: DistanceX(g32,g32) = 101.6
    c: DistanceY(g31,g31) = 25.4
    c: Coincident(g33,g34)
    c: Coincident(g34,g35)
    c: Coincident(g35,g36)
    c: Coincident(g36,g33)
    c: Vertical(g33)
    c: Vertical(g35)
    c: Horizontal(g34)
    c: Horizontal(g36)
    c: DistanceX(g36,g36) = 6
    c: DistanceY(g35,g35) = 12
    c: PointOnObject(g35,g29)
    c: Coincident(g37,g38)
    c: Coincident(g38,g39)
    c: Coincident(g39,g40)
    c: Coincident(g40,g37)
    c: Vertical(g37)
    c: Vertical(g39)
    c: Horizontal(g38)
    c: Horizontal(g40)
    c: DistanceX(g40,g40) = 6
    c: DistanceY(g39,g39) = 12
    c: PointOnObject(g37,g31)
    c: DistanceY(g29,g34) = 0
    c: DistanceY(g30,g37) = 0
    c: DistanceY(g0,g29) = 8
    c: Distance(g32,g6) = 7
    c: Distance(g8,g18) = 7
    c: DistanceX(g0,g0) = 122
    c: Coincident(g41,g0)
    c: Coincident(g41,g0)
    c: Vertical(g43)
    c: Distance(g0,g43) = 9
    c: DistanceX(g0,g42) = 8
    c: PointOnObject(g3,g42)
    c: PointOnObject(g4,g42)
    c: PointOnObject(g3,g43)
    c: PointOnObject(g4,g43)
    c: Coincident(g4,g44)
    c: PointOnObject(g44,g42)
    c: Coincident(g44,g45)
    c: Horizontal(g45)
    c: Coincident(g45,g46)
    c: Vertical(g46)
    c: Coincident(g46,g47)
    c: PointOnObject(g47,g42)
    c: Horizontal(g47)
    c: Coincident(g47,g48)
    c: Symmetric(g42,g42,g48)
    c: Coincident(g48,g49)
    c: Horizontal(g49)
    c: Coincident(g49,g50)
    c: Vertical(g50)
    c: Coincident(g50,g51)
    c: Horizontal(g51)
    c: Coincident(g51,g52)
    c: Coincident(g52,g53)
    c: Coincident(g53,g54)
    c: Coincident(g54,g55)
    c: PointOnObject(g55,g42)
    c: Horizontal(g55)
    c: Coincident(g55,g56)
    c: Coincident(g56,g3)
    c: PointOnObject(g51,g42)
    c: Vertical(g52)
    c: Vertical(g54)
    c: Vertical(g57)
    c: PointOnObject(g45,g57)
    c: PointOnObject(g49,g57)
    c: PointOnObject(g53,g57)
    c: DistanceY(g50,g50) = 12.3
    c: DistanceY(g46,g46) = 12.3
    c: DistanceY(g54,g54) = 12.3
    c: Horizontal(g53)
    c: Vertical(g42)
    c: DistanceX(g57,g42) = 4
    c: DistanceY(g56,g56) = 3
    c: DistanceY(g52,g52) = 20
    c: DistanceY(g48,g48) = 20
    c: Coincident(g4,g58)
    c: Vertical(g58)
    c: Coincident(g58,g59)
    c: Horizontal(g59)
    c: Coincident(g59,g60)
    c: Coincident(g60,g61)
    c: Coincident(g61,g62)
    c: Coincident(g62,g63)
    c: Horizontal(g63)
    c: Coincident(g63,g64)
    c: Vertical(g64)
    c: Coincident(g64,g65)
    c: Horizontal(g65)
    c: Coincident(g65,g66)
    c: Vertical(g66)
    c: Coincident(g66,g67)
    c: Horizontal(g67)
    c: Coincident(g67,g68)
    c: Vertical(g68)
    c: Coincident(g68,g69)
    c: Horizontal(g69)
    c: Coincident(g69,g70)
    c: Coincident(g70,g3)
    c: PointOnObject(g62,g43)
    c: Vertical(g62)
    c: PointOnObject(g65,g43)
    c: Vertical(g60)
    c: Horizontal(g61)
    c: Vertical(g71)
    c: PointOnObject(g60,g71)
    c: PointOnObject(g64,g71)
    c: Vertical(g70)
    c: PointOnObject(g67,g71)
    c: DistanceY(g64,g64) = 12.3
    c: DistanceY(g60,g60) = 12.3
    c: DistanceY(g68,g68) = 12.3
    c: DistanceY(g66,g66) = 20
    c: DistanceY(g62,g62) = 20
    c: DistanceX(g43,g71) = 4.5
    c: Coincident(g2,g72)
    c: Coincident(g72,g0)
    c: DistanceY(g4,g1) = 5
    c: DistanceY(g17,g4) = 1.8
    c: DistanceY(g0,g3) = 5
    c: DistanceY(g3,g69) = 3
    c: DistanceY(g72,g72) = 105
FEATURE [PartDesign::Pad] Pad006
  Direction = (0,-1,2e-16)
  Length = 128
  Length2 = 10
  Placement = pos=(0,0,0) rot=(1,0,0;1.5708rad)
  Profile = -> Sketch026
  ReferenceAxis = -> Sketch026 [N_Axis]
  Suppressed = false
  Type = 0
FEATURE [Sketcher::SketchObject] Sketch027
  ArcFitTolerance = 1e-06
  AttachmentSupport = -> [Pad006]
  FullyConstrained = false
  MakeInternals = false
  MapMode = 5
  Placement = pos=(0,4.62e-14,105) rot=(0,0,1;3.14159rad)
  sketch-geometry (5):
    g0: LineSegment StartX=31.939 StartY=166.44 StartZ=0 EndX=-114 EndY=166.44 EndZ=0
    g1: LineSegment StartX=-114 StartY=166.44 StartZ=0 EndX=-114 EndY=-24.3217 EndZ=0
    g2: LineSegment StartX=-114 StartY=-24.3217 StartZ=0 EndX=31.939 EndY=-24.3217 EndZ=0
    g3: LineSegment StartX=31.939 StartY=-24.3217 StartZ=0 EndX=31.939 EndY=166.44 EndZ=0
    g4: LineSegment [constr] StartX=-122 StartY=139.982 StartZ=0 EndX=-122 EndY=-33.6905 EndZ=0
  constraints (12):
    c: Coincident(g0,g1)
    c: Coincident(g1,g2)
    c: Coincident(g2,g3)
    c: Coincident(g3,g0)
    c: Horizontal(g0)
    c: Horizontal(g2)
    c: Vertical(g1)
    c: Vertical(g3)
    c: Distance(g-1,g1) = 114
    c: Vertical(g4)
    c: DistanceX(g4,g-1) = 122
    c: DistanceX(g4,g1) = 8
FEATURE [PartDesign::Pocket] Pocket019
  BaseFeature = -> Pad006
  Direction = (0,0,-1)
  Length = 5
  Length2 = 5
  Placement = pos=(0,0,0) rot=(1,0,0;1.5708rad)
  Profile = -> Sketch027
  ReferenceAxis = -> Sketch027 [N_Axis]
  Suppressed = false
  Type = 1
FEATURE [Sketcher::SketchObject] Sketch028
  ArcFitTolerance = 1e-06
  AttachmentSupport = -> [Pocket019]
  FullyConstrained = false
  MakeInternals = false
  MapMode = 5
  Placement = pos=(114,0,0) rot=(0.707107,0,-0.707107;3.14159rad)
  sketch-geometry (25):
    g0: LineSegment StartX=-71.5 StartY=115 StartZ=0 EndX=-71.5 EndY=15 EndZ=0
    g1: LineSegment StartX=-71.5 StartY=15 StartZ=0 EndX=-54 EndY=15 EndZ=0
    g2: LineSegment StartX=-54 StartY=15 StartZ=0 EndX=-54 EndY=115 EndZ=0
    g3: LineSegment StartX=-54 StartY=115 StartZ=0 EndX=-71.5 EndY=115 EndZ=0
    g4: LineSegment StartX=-39 StartY=115 StartZ=0 EndX=-39 EndY=15 EndZ=0
    g5: LineSegment StartX=-39 StartY=15 StartZ=0 EndX=-21.5 EndY=15 EndZ=0
    g6: LineSegment StartX=-21.5 StartY=15 StartZ=0 EndX=-21.5 EndY=115 EndZ=0
    g7: LineSegment StartX=-21.5 StartY=115 StartZ=0 EndX=-39 EndY=115 EndZ=0
    g8: LineSegment StartX=-114.5 StartY=115 StartZ=0 EndX=-114.5 EndY=15 EndZ=0
    g9: LineSegment StartX=-114.5 StartY=15 StartZ=0 EndX=-89.5 EndY=15 EndZ=0
    g10: LineSegment StartX=-89.5 StartY=15 StartZ=0 EndX=-89.5 EndY=115 EndZ=0
    g11: LineSegment StartX=-89.5 StartY=115 StartZ=0 EndX=-114.5 EndY=115 EndZ=0
    g12: LineSegment StartX=-6.5 StartY=115 StartZ=0 EndX=-6.5 EndY=15 EndZ=0
    g13: LineSegment StartX=-6.5 StartY=15 StartZ=0 EndX=15.5 EndY=15 EndZ=0
    g14: LineSegment StartX=15.5 StartY=15 StartZ=0 EndX=15.5 EndY=115 EndZ=0
    g15: LineSegment StartX=15.5 StartY=115 StartZ=0 EndX=-6.5 EndY=115 EndZ=0
    g16: LineSegment [constr] StartX=-125.86 StartY=115 StartZ=0 EndX=26.0337 EndY=115 EndZ=0
    g17: LineSegment [constr] StartX=-133.161 StartY=15 StartZ=0 EndX=42.6244 EndY=15 EndZ=0
    g18: LineSegment [constr] StartX=-136.946 StartY=130 StartZ=0 EndX=57.8834 EndY=130 EndZ=0
    g19: LineSegment [constr] StartX=-40.4378 StartY=159.765 StartZ=0 EndX=-40.4378 EndY=-27.8418 EndZ=0
    g20: LineSegment [constr] StartX=-52.4378 StartY=160.511 StartZ=0 EndX=-52.4378 EndY=-23.1796 EndZ=0
    g21: LineSegment [constr] StartX=-72.7649 StartY=166.851 StartZ=0 EndX=-72.7649 EndY=-20.7553 EndZ=0
    g22: LineSegment [constr] StartX=-84.7649 StartY=166.851 StartZ=0 EndX=-84.7649 EndY=-20.1958 EndZ=0
    g23: LineSegment [constr] StartX=-19.9889 StartY=166.478 StartZ=0 EndX=-19.9889 EndY=-20.3823 EndZ=0
    g24: LineSegment [constr] StartX=-7.98889 StartY=166.292 StartZ=0 EndX=-7.98889 EndY=-11.9904 EndZ=0
  constraints (63):
    c: Coincident(g0,g1)
    c: Coincident(g1,g2)
    c: Coincident(g2,g3)
    c: Coincident(g3,g0)
    c: Vertical(g0)
    c: Vertical(g2)
    c: Horizontal(g1)
    c: Horizontal(g3)
    c: Coincident(g4,g5)
    c: Coincident(g5,g6)
    c: Coincident(g6,g7)
    c: Coincident(g7,g4)
    c: Vertical(g4)
    c: Vertical(g6)
    c: Horizontal(g5)
    c: Horizontal(g7)
    c: Coincident(g8,g9)
    c: Coincident(g9,g10)
    c: Coincident(g10,g11)
    c: Coincident(g11,g8)
    c: Vertical(g8)
    c: Vertical(g10)
    c: Horizontal(g9)
    c: Horizontal(g11)
    c: Coincident(g12,g13)
    c: Coincident(g13,g14)
    c: Coincident(g14,g15)
    c: Coincident(g15,g12)
    c: Vertical(g12)
    c: Vertical(g14)
    c: Horizontal(g13)
    c: Horizontal(g15)
    c: Horizontal(g16)
    c: PointOnObject(g12,g16)
    c: PointOnObject(g6,g16)
    c: PointOnObject(g2,g16)
    c: PointOnObject(g10,g16)
    c: Horizontal(g17)
    c: PointOnObject(g13,g17)
    c: PointOnObject(g5,g17)
    c: PointOnObject(g1,g17)
    c: PointOnObject(g9,g17)
    c: DistanceX(g5,g5) = 17.5
    c: DistanceX(g13,g13) = 22
    c: DistanceX(g1,g1) = 17.5
    c: DistanceX(g9,g9) = 25
    c: DistanceX(g1,g4) = 15
    c: DistanceX(g9,g0) = 18
    c: DistanceX(g5,g12) = 15
    c: DistanceX(g12,g-1) = 6.5
    c: DistanceY(g-1,g13) = 15
    c: Horizontal(g18)
    c: Distance(g-1,g18) = 130
    c: DistanceY(g16,g18) = 15
    c: Vertical(g19)
    c: Vertical(g20)
    c: Vertical(g21)
    c: Vertical(g22)
    c: Vertical(g23)
    c: Vertical(g24)
    c: Distance(g19,g20) = 12
    c: Distance(g24,g23) = 12
    c: Distance(g22,g21) = 12
FEATURE [PartDesign::Pocket] Pocket020
  BaseFeature = -> Pocket019
  Direction = (1,0,2e-16)
  Length = 5
  Length2 = 5
  Placement = pos=(0,0,0) rot=(1,0,0;1.5708rad)
  Profile = -> Sketch028
  ReferenceAxis = -> Sketch028 [N_Axis]
  Suppressed = false
  Type = 1
FEATURE [Sketcher::SketchObject] Sketch029
  ArcFitTolerance = 1e-06
  AttachmentSupport = -> [Pocket020]
  FullyConstrained = false
  MakeInternals = false
  MapMode = 5
  Placement = pos=(114,0,0) rot=(0.707107,0,-0.707107;3.14159rad)
  sketch-geometry (5):
    g0: LineSegment [constr] StartX=-108.999 StartY=128 StartZ=0 EndX=36.7428 EndY=128 EndZ=0
    g1: LineSegment StartX=-100.706 StartY=128 StartZ=0 EndX=-100.706 EndY=125 EndZ=0
    g2: LineSegment StartX=-100.706 StartY=125 StartZ=0 EndX=-2.16393 EndY=125 EndZ=0
    g3: LineSegment StartX=-2.16393 StartY=125 StartZ=0 EndX=-2.16393 EndY=128 EndZ=0
    g4: LineSegment StartX=-2.16393 StartY=128 StartZ=0 EndX=-100.706 EndY=128 EndZ=0
  constraints (12):
    c: Horizontal(g0)
    c: DistanceY(g-1,g0) = 128
    c: Coincident(g1,g2)
    c: Coincident(g2,g3)
    c: Coincident(g3,g4)
    c: Coincident(g4,g1)
    c: Vertical(g1)
    c: Vertical(g3)
    c: Horizontal(g2)
    c: Horizontal(g4)
    c: PointOnObject(g1,g0)
    c: DistanceY(g3,g3) = 3
FEATURE [PartDesign::Pad] Pad007
  BaseFeature = -> Pocket020
  Direction = (-1,0,-2e-16)
  Length = 7
  Length2 = 10
  Placement = pos=(0,0,0) rot=(1,0,0;1.5708rad)
  Profile = -> Sketch029
  ReferenceAxis = -> Sketch029 [N_Axis]
  Reversed = true
  Suppressed = false
  Type = 0
FEATURE [Sketcher::SketchObject] Sketch030
  ArcFitTolerance = 1e-06
  AttachmentSupport = -> [Pad007]
  FullyConstrained = false
  MakeInternals = false
  MapMode = 5
  Placement = pos=(0,1.16e-14,0) rot=(-1,0,0;1.5708rad)
  sketch-geometry (9):
    g0: LineSegment [constr] StartX=118 StartY=-116.011 StartZ=0 EndX=118 EndY=24.4142 EndZ=0
    g1: LineSegment [constr] StartX=151.305 StartY=-99 StartZ=0 EndX=-46.3715 EndY=-99 EndZ=0
    g2: LineSegment [constr] StartX=-15.7875 StartY=-67 StartZ=0 EndX=147.389 EndY=-67 EndZ=0
    g3: LineSegment [constr] StartX=139.37 StartY=-35 StartZ=0 EndX=-40.5904 EndY=-35 EndZ=0
    g4: LineSegment [constr] StartX=128.173 StartY=-4 StartZ=0 EndX=-37.4283 EndY=-4 EndZ=0
    g5: Circle CenterX=118 CenterY=-99 CenterZ=0 NormalX=0 NormalY=0 NormalZ=1 AngleXU=0 Radius=2.25
    g6: Circle CenterX=118 CenterY=-67 CenterZ=0 NormalX=0 NormalY=0 NormalZ=1 AngleXU=0 Radius=2.25
    g7: Circle CenterX=118 CenterY=-35 CenterZ=0 NormalX=0 NormalY=0 NormalZ=1 AngleXU=0 Radius=2.25
    g8: Circle CenterX=118 CenterY=-4 CenterZ=0 NormalX=0 NormalY=0 NormalZ=1 AngleXU=0 Radius=2.25
  constraints (22):
    c: Vertical(g0)
    c: Distance(g-1,g0) = 118
    c: Horizontal(g1)
    c: Horizontal(g2)
    c: Horizontal(g3)
    c: Distance(g-1,g3) = 35
    c: DistanceY(g2,g3) = 32
    c: DistanceY(g1,g2) = 32
    c: Horizontal(g4)
    c: DistanceY(g3,g4) = 31
    c: PointOnObject(g5,g1)
    c: PointOnObject(g6,g2)
    c: PointOnObject(g7,g3)
    c: Diameter(g7) = 4.5
    c: Equal(g6,g7)
    c: Equal(g5,g7)
    c: PointOnObject(g7,g0)
    c: PointOnObject(g6,g0)
    c: PointOnObject(g5,g0)
    c: PointOnObject(g8,g4)
    c: Equal(g8,g7)
    c: PointOnObject(g8,g0)
FEATURE [PartDesign::Pocket] Pocket021
  BaseFeature = -> Pad007
  Direction = (0,-1,-2e-16)
  Length = 6
  Length2 = 5
  Placement = pos=(0,0,0) rot=(1,0,0;1.5708rad)
  Profile = -> Sketch030
  ReferenceAxis = -> Sketch030 [N_Axis]
  Suppressed = false
  Type = 0
FEATURE [Sketcher::SketchObject] Sketch031
  ArcFitTolerance = 1e-06
  AttachmentSupport = -> [Pocket021]
  FullyConstrained = false
  MakeInternals = false
  MapMode = 5
  Placement = pos=(0,-128,0) rot=(1,0,0;1.5708rad)
  sketch-geometry (7):
    g0: LineSegment [constr] StartX=118 StartY=118.341 StartZ=0 EndX=118 EndY=-18.5409 EndZ=0
    g1: LineSegment [constr] StartX=-8.12958 StartY=35 StartZ=0 EndX=153.104 EndY=35 EndZ=0
    g2: LineSegment [constr] StartX=-11.3359 StartY=67 StartZ=0 EndX=162.417 EndY=67 EndZ=0
    g3: LineSegment [constr] StartX=-12.0993 StartY=99 StartZ=0 EndX=154.936 EndY=99 EndZ=0
    g4: LineSegment [constr] StartX=-7.06079 StartY=4 StartZ=0 EndX=169.746 EndY=4 EndZ=0
    g5: Circle CenterX=118 CenterY=99 CenterZ=0 NormalX=0 NormalY=0 NormalZ=1 AngleXU=0 Radius=2.25
    g6: Circle CenterX=118 CenterY=4 CenterZ=0 NormalX=0 NormalY=0 NormalZ=1 AngleXU=0 Radius=2.25
  constraints (16):
    c: Vertical(g0)
    c: Distance(g-1,g0) = 118
    c: Horizontal(g1)
    c: Horizontal(g2)
    c: Horizontal(g3)
    c: Distance(g2,g1) = 32
    c: Distance(g3,g2) = 32
    c: DistanceY(g-1,g1) = 35
    c: Horizontal(g4)
    c: DistanceY(g4,g1) = 31
    c: PointOnObject(g5,g3)
    c: PointOnObject(g6,g4)
    c: Diameter(g6) = 4.5
    c: Equal(g5,g6)
    c: PointOnObject(g6,g0)
    c: PointOnObject(g5,g0)
FEATURE [PartDesign::Pocket] Pocket022
  BaseFeature = -> Pocket021
  Direction = (0,1,-2e-16)
  Length = 6
  Length2 = 5
  Placement = pos=(0,0,0) rot=(1,0,0;1.5708rad)
  Profile = -> Sketch031
  ReferenceAxis = -> Sketch031 [N_Axis]
  Suppressed = false
  Type = 0
FEATURE [PartDesign::Body] Body006  label="SideV2Short"
  AllowCompound = false
  Group = -> [Sketch026,Pad006,Sketch027,Pocket019,Sketch028,Pocket020,Sketch029,Pad007,Sketch030,Pocket021,Sketch031,Pocket022]
  Origin = -> Origin006
  Placement = pos=(126,-7.07e-14,0) rot=(0,0,-1;3.14159rad)
  Tip = -> Pocket022
FEATURE [PartDesign::Hole] Hole004
  BaseFeature = -> Pocket018
  CustomThreadClearance = 0
  Depth = 4
  DepthType = 0
  Diameter = 6.5
  DrillForDepth = false
  DrillPoint = 0
  DrillPointAngle = 9
  HoleCutCountersinkAngle = 90
  HoleCutCustomValues = false
  HoleCutDepth = 0
  HoleCutDiameter = 0
  HoleCutType = 0
  ModelThread = false
  Placement = pos=(0,0,0) rot=(1,0,0;1.5708rad)
  Profile = -> Pocket018 [Edge40,Edge41,Edge42,Edge43]
  Reversed = true
  Suppressed = false
  Tapered = false
  TaperedAngle = 90
  ThreadClass = 0
  ThreadDepth = 4
  ThreadDepthType = 0
  ThreadDirection = 0
  ThreadFit = 0
  ThreadSize = 0
  ThreadType = 0
  Threaded = false
  UseCustomThreadClearance = false
FEATURE [PartDesign::Hole] Hole005
  BaseFeature = -> Hole004
  CustomThreadClearance = 0
  Depth = 12
  DepthType = 0
  Diameter = 6.5
  DrillForDepth = false
  DrillPoint = 0
  DrillPointAngle = 118
  HoleCutCountersinkAngle = 90
  HoleCutCustomValues = false
  HoleCutDepth = 0
  HoleCutDiameter = 6.6
  HoleCutType = 0
  ModelThread = false
  Placement = pos=(0,0,0) rot=(1,0,0;1.5708rad)
  Profile = -> Hole004 [Edge45,Edge51]
  Reversed = true
  Suppressed = false
  Tapered = false
  TaperedAngle = 90
  ThreadClass = 0
  ThreadDepth = 12
  ThreadDepthType = 0
  ThreadDirection = 0
  ThreadFit = 0
  ThreadSize = 0
  ThreadType = 0
  Threaded = false
  UseCustomThreadClearance = false
FEATURE [App::DocumentObjectGroup] Group  label="v1"
  Group = -> [Body001,Body,Body002,Body003,Body004]
FEATURE [Sketcher::SketchObject] Sketch032
  ArcFitTolerance = 1e-06
  AttachmentSupport = -> [XZ_Plane007]
  FullyConstrained = false
  MakeInternals = false
  MapMode = 5
  Placement = pos=(0,0,0) rot=(1,0,0;1.5708rad)
  sketch-geometry (73):
    g0: LineSegment [constr] StartX=0 StartY=0 StartZ=0 EndX=122 EndY=0 EndZ=0
    g1: LineSegment StartX=122 StartY=0 StartZ=0 EndX=122 EndY=105 EndZ=0
    g2: LineSegment StartX=122 StartY=105 StartZ=0 EndX=0 EndY=105 EndZ=0
    g3: LineSegment StartX=8 StartY=5 StartZ=0 EndX=113 EndY=5 EndZ=0
    g4: LineSegment StartX=113 StartY=100 StartZ=0 EndX=8 EndY=100 EndZ=0
    g5: LineSegment [constr] StartX=190.257 StartY=65.8 StartZ=0 EndX=190.257 EndY=40.4 EndZ=0
    g6: LineSegment [constr] StartX=190.257 StartY=40.4 StartZ=0 EndX=291.857 EndY=40.4 EndZ=0
    g7: LineSegment [constr] StartX=291.857 StartY=40.4 StartZ=0 EndX=291.857 EndY=65.8 EndZ=0
    g8: LineSegment [constr] StartX=291.857 StartY=65.8 StartZ=0 EndX=190.257 EndY=65.8 EndZ=0
    g9: LineSegment [constr] StartX=184.257 StartY=52.4 StartZ=0 EndX=184.257 EndY=40.4 EndZ=0
    g10: LineSegment [constr] StartX=184.257 StartY=40.4 StartZ=0 EndX=190.257 EndY=40.4 EndZ=0
    g11: LineSegment [constr] StartX=190.257 StartY=40.4 StartZ=0 EndX=190.257 EndY=52.4 EndZ=0
    g12: LineSegment [constr] StartX=190.257 StartY=52.4 StartZ=0 EndX=184.257 EndY=52.4 EndZ=0
    g13: LineSegment [constr] StartX=291.857 StartY=52.4 StartZ=0 EndX=291.857 EndY=40.4 EndZ=0
    g14: LineSegment [constr] StartX=291.857 StartY=40.4 StartZ=0 EndX=297.857 EndY=40.4 EndZ=0
    g15: LineSegment [constr] StartX=297.857 StartY=40.4 StartZ=0 EndX=297.857 EndY=52.4 EndZ=0
    g16: LineSegment [constr] StartX=297.857 StartY=52.4 StartZ=0 EndX=291.857 EndY=52.4 EndZ=0
    g17: LineSegment [constr] StartX=163.474 StartY=98.2 StartZ=0 EndX=163.474 EndY=72.8 EndZ=0
    g18: LineSegment [constr] StartX=163.474 StartY=72.8 StartZ=0 EndX=265.074 EndY=72.8 EndZ=0
    g19: LineSegment [constr] StartX=265.074 StartY=72.8 StartZ=0 EndX=265.074 EndY=98.2 EndZ=0
    g20: LineSegment [constr] StartX=265.074 StartY=98.2 StartZ=0 EndX=163.474 EndY=98.2 EndZ=0
    g21: LineSegment [constr] StartX=157.474 StartY=84.8 StartZ=0 EndX=157.474 EndY=72.8 EndZ=0
    g22: LineSegment [constr] StartX=157.474 StartY=72.8 StartZ=0 EndX=163.474 EndY=72.8 EndZ=0
    g23: LineSegment [constr] StartX=163.474 StartY=72.8 StartZ=0 EndX=163.474 EndY=84.8 EndZ=0
    g24: LineSegment [constr] StartX=163.474 StartY=84.8 StartZ=0 EndX=157.474 EndY=84.8 EndZ=0
    g25: LineSegment [constr] StartX=265.074 StartY=84.8 StartZ=0 EndX=265.074 EndY=72.8 EndZ=0
    g26: LineSegment [constr] StartX=265.074 StartY=72.8 StartZ=0 EndX=271.074 EndY=72.8 EndZ=0
    g27: LineSegment [constr] StartX=271.074 StartY=72.8 StartZ=0 EndX=271.074 EndY=84.8 EndZ=0
    g28: LineSegment [constr] StartX=271.074 StartY=84.8 StartZ=0 EndX=265.074 EndY=84.8 EndZ=0
    g29: LineSegment [constr] StartX=208.539 StartY=33.4 StartZ=0 EndX=208.539 EndY=8 EndZ=0
    g30: LineSegment [constr] StartX=208.539 StartY=8 StartZ=0 EndX=310.139 EndY=8 EndZ=0
    g31: LineSegment [constr] StartX=310.139 StartY=8 StartZ=0 EndX=310.139 EndY=33.4 EndZ=0
    g32: LineSegment [constr] StartX=310.139 StartY=33.4 StartZ=0 EndX=208.539 EndY=33.4 EndZ=0
    g33: LineSegment [constr] StartX=202.539 StartY=20 StartZ=0 EndX=202.539 EndY=8 EndZ=0
    g34: LineSegment [constr] StartX=202.539 StartY=8 StartZ=0 EndX=208.539 EndY=8 EndZ=0
    g35: LineSegment [constr] StartX=208.539 StartY=8 StartZ=0 EndX=208.539 EndY=20 EndZ=0
    g36: LineSegment [constr] StartX=208.539 StartY=20 StartZ=0 EndX=202.539 EndY=20 EndZ=0
    g37: LineSegment [constr] StartX=310.139 StartY=20 StartZ=0 EndX=310.139 EndY=8 EndZ=0
    g38: LineSegment [constr] StartX=310.139 StartY=8 StartZ=0 EndX=316.139 EndY=8 EndZ=0
    g39: LineSegment [constr] StartX=316.139 StartY=8 StartZ=0 EndX=316.139 EndY=20 EndZ=0
    g40: LineSegment [constr] StartX=316.139 StartY=20 StartZ=0 EndX=310.139 EndY=20 EndZ=0
    g41: LineSegment StartX=0 StartY=0 StartZ=0 EndX=122 EndY=0 EndZ=0
    g42: LineSegment [constr] StartX=8 StartY=177.265 StartZ=0 EndX=8 EndY=-72.0652 EndZ=0
    g43: LineSegment [constr] StartX=113 StartY=141.11 StartZ=0 EndX=113 EndY=26.7674 EndZ=0
    g44: LineSegment StartX=8 StartY=100 StartZ=0 EndX=8 EndY=84.9 EndZ=0
    g45: LineSegment StartX=8 StartY=84.9 StartZ=0 EndX=4 EndY=84.9 EndZ=0
    g46: LineSegment StartX=4 StartY=84.9 StartZ=0 EndX=4 EndY=72.6 EndZ=0
    g47: LineSegment StartX=4 StartY=72.6 StartZ=0 EndX=8 EndY=72.6 EndZ=0
    g48: LineSegment StartX=8 StartY=72.6 StartZ=0 EndX=8 EndY=52.6 EndZ=0
    g49: LineSegment StartX=8 StartY=52.6 StartZ=0 EndX=4 EndY=52.6 EndZ=0
    g50: LineSegment StartX=4 StartY=52.6 StartZ=0 EndX=4 EndY=40.3 EndZ=0
    g51: LineSegment StartX=4 StartY=40.3 StartZ=0 EndX=8 EndY=40.3 EndZ=0
    g52: LineSegment StartX=8 StartY=40.3 StartZ=0 EndX=8 EndY=20.3 EndZ=0
    g53: LineSegment StartX=8 StartY=20.3 StartZ=0 EndX=4 EndY=20.3 EndZ=0
    g54: LineSegment StartX=4 StartY=20.3 StartZ=0 EndX=4 EndY=8 EndZ=0
    g55: LineSegment StartX=4 StartY=8 StartZ=0 EndX=8 EndY=8 EndZ=0
    g56: LineSegment StartX=8 StartY=8 StartZ=0 EndX=8 EndY=5 EndZ=0
    g57: LineSegment [constr] StartX=4 StartY=110.102 StartZ=0 EndX=4 EndY=-9.82312 EndZ=0
    g58: LineSegment StartX=113 StartY=100 StartZ=0 EndX=113 EndY=84.9 EndZ=0
    g59: LineSegment StartX=113 StartY=84.9 StartZ=0 EndX=117.5 EndY=84.9 EndZ=0
    g60: LineSegment StartX=117.5 StartY=84.9 StartZ=0 EndX=117.5 EndY=72.6 EndZ=0
    g61: LineSegment StartX=117.5 StartY=72.6 StartZ=0 EndX=113 EndY=72.6 EndZ=0
    g62: LineSegment StartX=113 StartY=72.6 StartZ=0 EndX=113 EndY=52.6 EndZ=0
    g63: LineSegment StartX=113 StartY=52.6 StartZ=0 EndX=117.5 EndY=52.6 EndZ=0
    g64: LineSegment StartX=117.5 StartY=52.6 StartZ=0 EndX=117.5 EndY=40.3 EndZ=0
    g65: LineSegment StartX=117.5 StartY=40.3 StartZ=0 EndX=113 EndY=40.3 EndZ=0
    g66: LineSegment StartX=113 StartY=40.3 StartZ=0 EndX=113 EndY=20.3 EndZ=0
    g67: LineSegment StartX=113 StartY=20.3 StartZ=0 EndX=117.5 EndY=20.3 EndZ=0
    g68: LineSegment StartX=117.5 StartY=20.3 StartZ=0 EndX=117.5 EndY=8 EndZ=0
    g69: LineSegment StartX=117.5 StartY=8 StartZ=0 EndX=113 EndY=8 EndZ=0
    g70: LineSegment StartX=113 StartY=8 StartZ=0 EndX=113 EndY=5 EndZ=0
    g71: LineSegment [constr] StartX=117.5 StartY=109.281 StartZ=0 EndX=117.5 EndY=-16.6316 EndZ=0
    g72: LineSegment StartX=0 StartY=105 StartZ=0 EndX=0 EndY=0 EndZ=0
  constraints (212):
    c: Coincident(g-1,g0)
    c: Horizontal(g0)
    c: Coincident(g0,g1)
    c: Vertical(g1)
    c: Coincident(g1,g2)
    c: PointOnObject(g2,g-2)
    c: Horizontal(g2)
    c: Horizontal(g3)
    c: Horizontal(g4)
    c: Coincident(g5,g6)
    c: Coincident(g6,g7)
    c: Coincident(g7,g8)
    c: Coincident(g8,g5)
    c: Vertical(g5)
    c: Vertical(g7)
    c: Horizontal(g6)
    c: Horizontal(g8)
    c: DistanceX(g8,g8) = 101.6
    c: DistanceY(g7,g7) = 25.4
    c: Coincident(g9,g10)
    c: Coincident(g10,g11)
    c: Coincident(g11,g12)
    c: Coincident(g12,g9)
    c: Vertical(g9)
    c: Vertical(g11)
    c: Horizontal(g10)
    c: Horizontal(g12)
    c: DistanceX(g12,g12) = 6
    c: DistanceY(g11,g11) = 12
    c: PointOnObject(g11,g5)
    c: Coincident(g13,g14)
    c: Coincident(g14,g15)
    c: Coincident(g15,g16)
    c: Coincident(g16,g13)
    c: Vertical(g13)
    c: Vertical(g15)
    c: Horizontal(g14)
    c: Horizontal(g16)
    c: DistanceX(g16,g16) = 6
    c: DistanceY(g15,g15) = 12
    c: PointOnObject(g13,g7)
    c: DistanceY(g5,g10) = 0
    c: DistanceY(g6,g13) = 0
    c: DistanceX(g3,g3) = 105
    c: Coincident(g17,g18)
    c: Coincident(g18,g19)
    c: Coincident(g19,g20)
    c: Coincident(g20,g17)
    c: Vertical(g17)
    c: Vertical(g19)
    c: Horizontal(g18)
    c: Horizontal(g20)
    c: DistanceX(g20,g20) = 101.6
    c: DistanceY(g19,g19) = 25.4
    c: Coincident(g21,g22)
    c: Coincident(g22,g23)
    c: Coincident(g23,g24)
    c: Coincident(g24,g21)
    c: Vertical(g21)
    c: Vertical(g23)
    c: Horizontal(g22)
    c: Horizontal(g24)
    c: DistanceX(g24,g24) = 6
    c: DistanceY(g23,g23) = 12
    c: PointOnObject(g23,g17)
    c: Coincident(g25,g26)
    c: Coincident(g26,g27)
    c: Coincident(g27,g28)
    c: Coincident(g28,g25)
    c: Vertical(g25)
    c: Vertical(g27)
    c: Horizontal(g26)
    c: Horizontal(g28)
    c: DistanceX(g28,g28) = 6
    c: DistanceY(g27,g27) = 12
    c: PointOnObject(g25,g19)
    c: DistanceY(g17,g22) = 0
    c: DistanceY(g18,g25) = 0
    c: Coincident(g29,g30)
    c: Coincident(g30,g31)
    c: Coincident(g31,g32)
    c: Coincident(g32,g29)
    c: Vertical(g29)
    c: Vertical(g31)
    c: Horizontal(g30)
    c: Horizontal(g32)
    c: DistanceX(g32,g32) = 101.6
    c: DistanceY(g31,g31) = 25.4
    c: Coincident(g33,g34)
    c: Coincident(g34,g35)
    c: Coincident(g35,g36)
    c: Coincident(g36,g33)
    c: Vertical(g33)
    c: Vertical(g35)
    c: Horizontal(g34)
    c: Horizontal(g36)
    c: DistanceX(g36,g36) = 6
    c: DistanceY(g35,g35) = 12
    c: PointOnObject(g35,g29)
    c: Coincident(g37,g38)
    c: Coincident(g38,g39)
    c: Coincident(g39,g40)
    c: Coincident(g40,g37)
    c: Vertical(g37)
    c: Vertical(g39)
    c: Horizontal(g38)
    c: Horizontal(g40)
    c: DistanceX(g40,g40) = 6
    c: DistanceY(g39,g39) = 12
    c: PointOnObject(g37,g31)
    c: DistanceY(g29,g34) = 0
    c: DistanceY(g30,g37) = 0
    c: DistanceY(g0,g29) = 8
    c: Distance(g32,g6) = 7
    c: Distance(g8,g18) = 7
    c: DistanceX(g0,g0) = 122
    c: Coincident(g41,g0)
    c: Coincident(g41,g0)
    c: Vertical(g43)
    c: Distance(g0,g43) = 9
    c: DistanceX(g0,g42) = 8
    c: PointOnObject(g3,g42)
    c: PointOnObject(g4,g42)
    c: PointOnObject(g3,g43)
    c: PointOnObject(g4,g43)
    c: Coincident(g4,g44)
    c: PointOnObject(g44,g42)
    c: Coincident(g44,g45)
    c: Horizontal(g45)
    c: Coincident(g45,g46)
    c: Vertical(g46)
    c: Coincident(g46,g47)
    c: PointOnObject(g47,g42)
    c: Horizontal(g47)
    c: Coincident(g47,g48)
    c: Symmetric(g42,g42,g48)
    c: Coincident(g48,g49)
    c: Horizontal(g49)
    c: Coincident(g49,g50)
    c: Vertical(g50)
    c: Coincident(g50,g51)
    c: Horizontal(g51)
    c: Coincident(g51,g52)
    c: Coincident(g52,g53)
    c: Coincident(g53,g54)
    c: Coincident(g54,g55)
    c: PointOnObject(g55,g42)
    c: Horizontal(g55)
    c: Coincident(g55,g56)
    c: Coincident(g56,g3)
    c: PointOnObject(g51,g42)
    c: Vertical(g52)
    c: Vertical(g54)
    c: Vertical(g57)
    c: PointOnObject(g45,g57)
    c: PointOnObject(g49,g57)
    c: PointOnObject(g53,g57)
    c: DistanceY(g50,g50) = 12.3
    c: DistanceY(g46,g46) = 12.3
    c: DistanceY(g54,g54) = 12.3
    c: Horizontal(g53)
    c: Vertical(g42)
    c: DistanceX(g57,g42) = 4
    c: DistanceY(g56,g56) = 3
    c: DistanceY(g52,g52) = 20
    c: DistanceY(g48,g48) = 20
    c: Coincident(g4,g58)
    c: Vertical(g58)
    c: Coincident(g58,g59)
    c: Horizontal(g59)
    c: Coincident(g59,g60)
    c: Coincident(g60,g61)
    c: Coincident(g61,g62)
    c: Coincident(g62,g63)
    c: Horizontal(g63)
    c: Coincident(g63,g64)
    c: Vertical(g64)
    c: Coincident(g64,g65)
    c: Horizontal(g65)
    c: Coincident(g65,g66)
    c: Vertical(g66)
    c: Coincident(g66,g67)
    c: Horizontal(g67)
    c: Coincident(g67,g68)
    c: Vertical(g68)
    c: Coincident(g68,g69)
    c: Horizontal(g69)
    c: Coincident(g69,g70)
    c: Coincident(g70,g3)
    c: PointOnObject(g62,g43)
    c: Vertical(g62)
    c: PointOnObject(g65,g43)
    c: Vertical(g60)
    c: Horizontal(g61)
    c: Vertical(g71)
    c: PointOnObject(g60,g71)
    c: PointOnObject(g64,g71)
    c: Vertical(g70)
    c: PointOnObject(g67,g71)
    c: DistanceY(g64,g64) = 12.3
    c: DistanceY(g60,g60) = 12.3
    c: DistanceY(g68,g68) = 12.3
    c: DistanceY(g66,g66) = 20
    c: DistanceY(g62,g62) = 20
    c: DistanceX(g43,g71) = 4.5
    c: Coincident(g2,g72)
    c: Coincident(g72,g0)
    c: DistanceY(g4,g1) = 5
    c: DistanceY(g17,g4) = 1.8
    c: DistanceY(g0,g3) = 5
    c: DistanceY(g3,g69) = 3
    c: DistanceY(g72,g72) = 105
FEATURE [PartDesign::Pad] Pad008
  Direction = (0,-1,2e-16)
  Length = 140
  Length2 = 10
  Placement = pos=(0,0,0) rot=(1,0,0;1.5708rad)
  Profile = -> Sketch032
  ReferenceAxis = -> Sketch032 [N_Axis]
  Suppressed = false
  Type = 0
FEATURE [Sketcher::SketchObject] Sketch033
  ArcFitTolerance = 1e-06
  AttachmentSupport = -> [Pad008]
  FullyConstrained = false
  MakeInternals = false
  MapMode = 5
  Placement = pos=(0,4.62e-14,105) rot=(0,0,1;3.14159rad)
  sketch-geometry (5):
    g0: LineSegment StartX=31.939 StartY=166.44 StartZ=0 EndX=-114 EndY=166.44 EndZ=0
    g1: LineSegment StartX=-114 StartY=166.44 StartZ=0 EndX=-114 EndY=-24.3217 EndZ=0
    g2: LineSegment StartX=-114 StartY=-24.3217 StartZ=0 EndX=31.939 EndY=-24.3217 EndZ=0
    g3: LineSegment StartX=31.939 StartY=-24.3217 StartZ=0 EndX=31.939 EndY=166.44 EndZ=0
    g4: LineSegment [constr] StartX=-122 StartY=139.982 StartZ=0 EndX=-122 EndY=-33.6905 EndZ=0
  constraints (12):
    c: Coincident(g0,g1)
    c: Coincident(g1,g2)
    c: Coincident(g2,g3)
    c: Coincident(g3,g0)
    c: Horizontal(g0)
    c: Horizontal(g2)
    c: Vertical(g1)
    c: Vertical(g3)
    c: Distance(g-1,g1) = 114
    c: Vertical(g4)
    c: DistanceX(g4,g-1) = 122
    c: DistanceX(g4,g1) = 8
FEATURE [PartDesign::Pocket] Pocket023
  BaseFeature = -> Pad008
  Direction = (0,0,-1)
  Length = 5
  Length2 = 5
  Placement = pos=(0,0,0) rot=(1,0,0;1.5708rad)
  Profile = -> Sketch033
  ReferenceAxis = -> Sketch033 [N_Axis]
  Suppressed = false
  Type = 1
FEATURE [Sketcher::SketchObject] Sketch034
  ArcFitTolerance = 1e-06
  AttachmentSupport = -> [Pocket023]
  FullyConstrained = false
  MakeInternals = false
  MapMode = 5
  Placement = pos=(114,0,0) rot=(0.707107,0,-0.707107;3.14159rad)
  sketch-geometry (25):
    g0: LineSegment StartX=-71.5 StartY=125 StartZ=0 EndX=-71.5 EndY=15 EndZ=0
    g1: LineSegment StartX=-71.5 StartY=15 StartZ=0 EndX=-54 EndY=15 EndZ=0
    g2: LineSegment StartX=-54 StartY=15 StartZ=0 EndX=-54 EndY=125 EndZ=0
    g3: LineSegment StartX=-54 StartY=125 StartZ=0 EndX=-71.5 EndY=125 EndZ=0
    g4: LineSegment StartX=-39 StartY=125 StartZ=0 EndX=-39 EndY=15 EndZ=0
    g5: LineSegment StartX=-39 StartY=15 StartZ=0 EndX=-21.5 EndY=15 EndZ=0
    g6: LineSegment StartX=-21.5 StartY=15 StartZ=0 EndX=-21.5 EndY=125 EndZ=0
    g7: LineSegment StartX=-21.5 StartY=125 StartZ=0 EndX=-39 EndY=125 EndZ=0
    g8: LineSegment StartX=-114.5 StartY=125 StartZ=0 EndX=-114.5 EndY=15 EndZ=0
    g9: LineSegment StartX=-114.5 StartY=15 StartZ=0 EndX=-89.5 EndY=15 EndZ=0
    g10: LineSegment StartX=-89.5 StartY=15 StartZ=0 EndX=-89.5 EndY=125 EndZ=0
    g11: LineSegment StartX=-89.5 StartY=125 StartZ=0 EndX=-114.5 EndY=125 EndZ=0
    g12: LineSegment StartX=-6.5 StartY=125 StartZ=0 EndX=-6.5 EndY=15 EndZ=0
    g13: LineSegment StartX=-6.5 StartY=15 StartZ=0 EndX=15.5 EndY=15 EndZ=0
    g14: LineSegment StartX=15.5 StartY=15 StartZ=0 EndX=15.5 EndY=125 EndZ=0
    g15: LineSegment StartX=15.5 StartY=125 StartZ=0 EndX=-6.5 EndY=125 EndZ=0
    g16: LineSegment [constr] StartX=-125.86 StartY=125 StartZ=0 EndX=26.0337 EndY=125 EndZ=0
    g17: LineSegment [constr] StartX=-133.161 StartY=15 StartZ=0 EndX=42.6244 EndY=15 EndZ=0
    g18: LineSegment [constr] StartX=-136.946 StartY=140 StartZ=0 EndX=57.8834 EndY=140 EndZ=0
    g19: LineSegment [constr] StartX=-40.4378 StartY=159.765 StartZ=0 EndX=-40.4378 EndY=-27.8418 EndZ=0
    g20: LineSegment [constr] StartX=-52.4378 StartY=160.511 StartZ=0 EndX=-52.4378 EndY=-23.1796 EndZ=0
    g21: LineSegment [constr] StartX=-72.7649 StartY=166.851 StartZ=0 EndX=-72.7649 EndY=-20.7553 EndZ=0
    g22: LineSegment [constr] StartX=-84.7649 StartY=166.851 StartZ=0 EndX=-84.7649 EndY=-20.1958 EndZ=0
    g23: LineSegment [constr] StartX=-19.9889 StartY=166.478 StartZ=0 EndX=-19.9889 EndY=-20.3823 EndZ=0
    g24: LineSegment [constr] StartX=-7.98889 StartY=166.292 StartZ=0 EndX=-7.98889 EndY=-11.9904 EndZ=0
  constraints (63):
    c: Coincident(g0,g1)
    c: Coincident(g1,g2)
    c: Coincident(g2,g3)
    c: Coincident(g3,g0)
    c: Vertical(g0)
    c: Vertical(g2)
    c: Horizontal(g1)
    c: Horizontal(g3)
    c: Coincident(g4,g5)
    c: Coincident(g5,g6)
    c: Coincident(g6,g7)
    c: Coincident(g7,g4)
    c: Vertical(g4)
    c: Vertical(g6)
    c: Horizontal(g5)
    c: Horizontal(g7)
    c: Coincident(g8,g9)
    c: Coincident(g9,g10)
    c: Coincident(g10,g11)
    c: Coincident(g11,g8)
    c: Vertical(g8)
    c: Vertical(g10)
    c: Horizontal(g9)
    c: Horizontal(g11)
    c: Coincident(g12,g13)
    c: Coincident(g13,g14)
    c: Coincident(g14,g15)
    c: Coincident(g15,g12)
    c: Vertical(g12)
    c: Vertical(g14)
    c: Horizontal(g13)
    c: Horizontal(g15)
    c: Horizontal(g16)
    c: PointOnObject(g12,g16)
    c: PointOnObject(g6,g16)
    c: PointOnObject(g2,g16)
    c: PointOnObject(g10,g16)
    c: Horizontal(g17)
    c: PointOnObject(g13,g17)
    c: PointOnObject(g5,g17)
    c: PointOnObject(g1,g17)
    c: PointOnObject(g9,g17)
    c: DistanceX(g5,g5) = 17.5
    c: DistanceX(g13,g13) = 22
    c: DistanceX(g1,g1) = 17.5
    c: DistanceX(g9,g9) = 25
    c: DistanceX(g1,g4) = 15
    c: DistanceX(g9,g0) = 18
    c: DistanceX(g5,g12) = 15
    c: DistanceX(g12,g-1) = 6.5
    c: DistanceY(g-1,g13) = 15
    c: Horizontal(g18)
    c: DistanceY(g16,g18) = 15
    c: Vertical(g19)
    c: Vertical(g20)
    c: Vertical(g21)
    c: Vertical(g22)
    c: Vertical(g23)
    c: Vertical(g24)
    c: Distance(g19,g20) = 12
    c: Distance(g24,g23) = 12
    c: Distance(g22,g21) = 12
    c: Distance(g-1,g18) = 140
FEATURE [PartDesign::Pocket] Pocket024
  BaseFeature = -> Pocket023
  Direction = (1,0,2e-16)
  Length = 5
  Length2 = 5
  Placement = pos=(0,0,0) rot=(1,0,0;1.5708rad)
  Profile = -> Sketch034
  ReferenceAxis = -> Sketch034 [N_Axis]
  Suppressed = false
  Type = 1
FEATURE [Sketcher::SketchObject] Sketch035
  ArcFitTolerance = 1e-06
  AttachmentSupport = -> [Pocket024]
  FullyConstrained = false
  MakeInternals = false
  MapMode = 5
  Placement = pos=(114,0,0) rot=(0.707107,0,-0.707107;3.14159rad)
  sketch-geometry (5):
    g0: LineSegment [constr] StartX=-109.478 StartY=15 StartZ=0 EndX=36.2634 EndY=15 EndZ=0
    g1: LineSegment StartX=-101.479 StartY=15 StartZ=0 EndX=-101.479 EndY=0 EndZ=0
    g2: LineSegment StartX=-101.479 StartY=0 StartZ=0 EndX=-4.83531 EndY=0 EndZ=0
    g3: LineSegment StartX=-4.83531 StartY=0 StartZ=0 EndX=-4.83531 EndY=15 EndZ=0
    g4: LineSegment StartX=-4.83531 StartY=15 StartZ=0 EndX=-101.479 EndY=15 EndZ=0
  constraints (12):
    c: Horizontal(g0)
    c: Coincident(g1,g2)
    c: Coincident(g2,g3)
    c: Coincident(g3,g4)
    c: Coincident(g4,g1)
    c: Vertical(g1)
    c: Vertical(g3)
    c: Horizontal(g2)
    c: Horizontal(g4)
    c: PointOnObject(g1,g0)
    c: PointOnObject(g2,g-1)
    c: DistanceY(g-1,g0) = 15
FEATURE [PartDesign::Pad] Pad009
  BaseFeature = -> Pocket024
  Direction = (-1,0,-2e-16)
  Length = 7
  Length2 = 10
  Placement = pos=(0,0,0) rot=(1,0,0;1.5708rad)
  Profile = -> Sketch035
  ReferenceAxis = -> Sketch035 [N_Axis]
  Reversed = true
  Suppressed = false
  Type = 0
FEATURE [Sketcher::SketchObject] Sketch036
  ArcFitTolerance = 1e-06
  AttachmentSupport = -> [Pad009]
  FullyConstrained = false
  MakeInternals = false
  MapMode = 5
  Placement = pos=(0,1.16e-14,0) rot=(-1,0,0;1.5708rad)
  sketch-geometry (9):
    g0: LineSegment [constr] StartX=118 StartY=-116.011 StartZ=0 EndX=118 EndY=24.4142 EndZ=0
    g1: LineSegment [constr] StartX=151.305 StartY=-99 StartZ=0 EndX=-46.3715 EndY=-99 EndZ=0
    g2: LineSegment [constr] StartX=-15.7875 StartY=-67 StartZ=0 EndX=147.389 EndY=-67 EndZ=0
    g3: LineSegment [constr] StartX=139.37 StartY=-35 StartZ=0 EndX=-40.5904 EndY=-35 EndZ=0
    g4: LineSegment [constr] StartX=128.173 StartY=-4 StartZ=0 EndX=-37.4283 EndY=-4 EndZ=0
    g5: Circle CenterX=118 CenterY=-99 CenterZ=0 NormalX=0 NormalY=0 NormalZ=1 AngleXU=0 Radius=2.25
    g6: Circle CenterX=118 CenterY=-67 CenterZ=0 NormalX=0 NormalY=0 NormalZ=1 AngleXU=0 Radius=2.25
    g7: Circle CenterX=118 CenterY=-35 CenterZ=0 NormalX=0 NormalY=0 NormalZ=1 AngleXU=0 Radius=2.25
    g8: Circle CenterX=118 CenterY=-4 CenterZ=0 NormalX=0 NormalY=0 NormalZ=1 AngleXU=0 Radius=2.25
  constraints (22):
    c: Vertical(g0)
    c: Distance(g-1,g0) = 118
    c: Horizontal(g1)
    c: Horizontal(g2)
    c: Horizontal(g3)
    c: Distance(g-1,g3) = 35
    c: DistanceY(g2,g3) = 32
    c: DistanceY(g1,g2) = 32
    c: Horizontal(g4)
    c: DistanceY(g3,g4) = 31
    c: PointOnObject(g5,g1)
    c: PointOnObject(g6,g2)
    c: PointOnObject(g7,g3)
    c: Diameter(g7) = 4.5
    c: Equal(g6,g7)
    c: Equal(g5,g7)
    c: PointOnObject(g7,g0)
    c: PointOnObject(g6,g0)
    c: PointOnObject(g5,g0)
    c: PointOnObject(g8,g4)
    c: Equal(g8,g7)
    c: PointOnObject(g8,g0)
FEATURE [PartDesign::Pocket] Pocket025
  BaseFeature = -> Pad009
  Direction = (0,-1,-2e-16)
  Length = 6
  Length2 = 5
  Placement = pos=(0,0,0) rot=(1,0,0;1.5708rad)
  Profile = -> Sketch036
  ReferenceAxis = -> Sketch036 [N_Axis]
  Suppressed = false
  Type = 0
FEATURE [Sketcher::SketchObject] Sketch037
  ArcFitTolerance = 1e-06
  AttachmentSupport = -> [Pocket025]
  FullyConstrained = false
  MakeInternals = false
  MapMode = 5
  Placement = pos=(0,-140,0) rot=(1,0,0;1.5708rad)
  sketch-geometry (10):
    g0: LineSegment [constr] StartX=122 StartY=114.328 StartZ=0 EndX=122 EndY=-4.90445 EndZ=0
    g1: LineSegment [constr] StartX=118 StartY=117.52 StartZ=0 EndX=118 EndY=-18.0482 EndZ=0
    g2: LineSegment [constr] StartX=-13.4897 StartY=99 StartZ=0 EndX=178.221 EndY=99 EndZ=0
    g3: LineSegment [constr] StartX=-28.8867 StartY=67 StartZ=0 EndX=169.584 EndY=67 EndZ=0
    g4: LineSegment [constr] StartX=-23.0659 StartY=35 StartZ=0 EndX=151.183 EndY=35 EndZ=0
    g5: LineSegment [constr] StartX=-16.494 StartY=4 StartZ=0 EndX=170.523 EndY=4 EndZ=0
    g6: Circle CenterX=118 CenterY=99 CenterZ=0 NormalX=0 NormalY=0 NormalZ=1 AngleXU=0 Radius=2.25
    g7: Circle CenterX=118 CenterY=67 CenterZ=0 NormalX=0 NormalY=0 NormalZ=1 AngleXU=0 Radius=2.25
    g8: Circle CenterX=118 CenterY=35 CenterZ=0 NormalX=0 NormalY=0 NormalZ=1 AngleXU=0 Radius=2.25
    g9: Circle CenterX=118 CenterY=4 CenterZ=0 NormalX=0 NormalY=0 NormalZ=1 AngleXU=0 Radius=2.25
  constraints (24):
    c: Vertical(g0)
    c: DistanceX(g-1,g0) = 122
    c: Vertical(g1)
    c: DistanceX(g1,g0) = 4
    c: Horizontal(g2)
    c: Horizontal(g3)
    c: Horizontal(g4)
    c: Horizontal(g5)
    c: DistanceY(g-1,g5) = 4
    c: DistanceY(g5,g4) = 31
    c: DistanceY(g4,g3) = 32
    c: DistanceY(g3,g2) = 32
    c: PointOnObject(g6,g2)
    c: Diameter(g6) = 4.5
    c: PointOnObject(g6,g1)
    c: PointOnObject(g7,g3)
    c: Equal(g7,g6)
    c: PointOnObject(g8,g4)
    c: Equal(g8,g6)
    c: PointOnObject(g9,g5)
    c: Equal(g9,g6)
    c: PointOnObject(g7,g1)
    c: PointOnObject(g8,g1)
    c: PointOnObject(g9,g1)
FEATURE [PartDesign::Pocket] Pocket026
  BaseFeature = -> Pocket025
  Direction = (0,1,-2e-16)
  Length = 6
  Length2 = 5
  Placement = pos=(0,0,0) rot=(1,0,0;1.5708rad)
  Profile = -> Sketch037
  ReferenceAxis = -> Sketch037 [N_Axis]
  Suppressed = false
  Type = 0
FEATURE [Sketcher::SketchObject] Sketch038
  ArcFitTolerance = 1e-06
  AttachmentSupport = -> [Pocket026]
  FullyConstrained = false
  MakeInternals = false
  MapMode = 5
  Placement = pos=(122,0,0) rot=(0.707107,0,0.707107;3.14159rad)
  sketch-geometry (11):
    g0: LineSegment [constr] StartX=-12.893 StartY=133 StartZ=0 EndX=139.159 EndY=133 EndZ=0
    g1: LineSegment [constr] StartX=117.601 StartY=8 StartZ=0 EndX=-22.0666 EndY=8 EndZ=0
    g2: LineSegment [constr] StartX=27 StartY=155.142 StartZ=0 EndX=27 EndY=-19.8444 EndZ=0
    g3: LineSegment [constr] StartX=59 StartY=156.977 StartZ=0 EndX=59 EndY=-27.1833 EndZ=0
    g4: LineSegment [constr] StartX=91 StartY=160.646 StartZ=0 EndX=91 EndY=-26.7246 EndZ=0
    g5: Circle CenterX=27 CenterY=133 CenterZ=0 NormalX=0 NormalY=0 NormalZ=1 AngleXU=0 Radius=2.25
    g6: Circle CenterX=59 CenterY=133 CenterZ=0 NormalX=0 NormalY=0 NormalZ=1 AngleXU=0 Radius=2.25
    g7: Circle CenterX=91 CenterY=133 CenterZ=0 NormalX=0 NormalY=0 NormalZ=1 AngleXU=0 Radius=2.25
    g8: Circle CenterX=91 CenterY=8 CenterZ=0 NormalX=0 NormalY=0 NormalZ=1 AngleXU=0 Radius=2.25
    g9: Circle CenterX=59 CenterY=8 CenterZ=0 NormalX=0 NormalY=0 NormalZ=1 AngleXU=0 Radius=2.25
    g10: Circle CenterX=27 CenterY=8 CenterZ=0 NormalX=0 NormalY=0 NormalZ=1 AngleXU=0 Radius=2.25
  constraints (28):
    c: Horizontal(g0)
    c: Horizontal(g1)
    c: Vertical(g2)
    c: Vertical(g3)
    c: Vertical(g4)
    c: DistanceY(g-1,g1) = 8
    c: DistanceY(g-1,g0) = 133
    c: DistanceX(g-1,g2) = 27
    c: DistanceX(g2,g3) = 32
    c: DistanceX(g3,g4) = 32
    c: PointOnObject(g5,g2)
    c: PointOnObject(g6,g3)
    c: PointOnObject(g7,g4)
    c: PointOnObject(g8,g4)
    c: PointOnObject(g9,g3)
    c: PointOnObject(g10,g2)
    c: Diameter(g5) = 4.5
    c: Equal(g6,g7)
    c: Equal(g7,g8)
    c: Equal(g8,g9)
    c: Equal(g9,g10)
    c: Equal(g10,g5)
    c: PointOnObject(g5,g0)
    c: PointOnObject(g6,g0)
    c: PointOnObject(g7,g0)
    c: PointOnObject(g8,g1)
    c: PointOnObject(g9,g1)
    c: PointOnObject(g10,g1)
FEATURE [PartDesign::Pocket] Pocket027
  BaseFeature = -> Pocket026
  Direction = (-1,0,2e-16)
  Length = 8
  Length2 = 5
  Placement = pos=(0,0,0) rot=(1,0,0;1.5708rad)
  Profile = -> Sketch038
  ReferenceAxis = -> Sketch038 [N_Axis]
  Suppressed = false
  Type = 0
FEATURE [PartDesign::Hole] Hole006
  BaseFeature = -> Pocket027
  CustomThreadClearance = 0
  Depth = 3.5
  DepthType = 0
  Diameter = 9
  DrillForDepth = false
  DrillPoint = 0
  DrillPointAngle = 118
  HoleCutCountersinkAngle = 90
  HoleCutCustomValues = false
  HoleCutDepth = 0
  HoleCutDiameter = 6.1
  HoleCutType = 0
  ModelThread = false
  Placement = pos=(0,0,0) rot=(1,0,0;1.5708rad)
  Profile = -> Pocket027 [Edge85,Edge83,Edge81,Edge97,Edge109,Edge111]
  Reversed = true
  Suppressed = false
  Tapered = false
  TaperedAngle = 90
  ThreadClass = 0
  ThreadDepth = 3.5
  ThreadDepthType = 0
  ThreadDirection = 0
  ThreadFit = 0
  ThreadSize = 0
  ThreadType = 0
  Threaded = false
  UseCustomThreadClearance = false
FEATURE [PartDesign::Body] Body007  label="SideV2Long"
  AllowCompound = false
  Group = -> [Sketch032,Pad008,Sketch033,Pocket023,Sketch034,Pocket024,Sketch035,Pad009,Sketch036,Pocket025,Sketch037,Pocket026,Sketch038,Pocket027,Hole006]
  Origin = -> Origin007
  Placement = pos=(1,140,0) rot=(0,0,1;0rad)
  Tip = -> Hole006
FEATURE [PartDesign::Chamfer] Chamfer
  Angle = 45
  Base = -> Hole005 [Edge30,Edge78,Edge12,Edge61]
  BaseFeature = -> Hole005
  ChamferType = 0
  FlipDirection = false
  Placement = pos=(0,0,0) rot=(1,0,0;1.5708rad)
  Size = 5.8
  Size2 = 1
  SupportTransform = false
  Suppressed = false
  UseAllEdges = false
FEATURE [PartDesign::Body] Body005  label="BackV2"
  AllowCompound = false
  Group = -> [Sketch020,Pad005,Sketch021,Pocket014,Sketch022,Pocket015,Sketch023,Pocket016,Sketch024,Pocket017,Sketch025,Pocket018,Hole004,Hole005,Chamfer]
  Origin = -> Origin005
  Placement = pos=(123,140,0) rot=(0,0,1;3.14159rad)
  Tip = -> Chamfer
FEATURE [Sketcher::SketchObject] Sketch046
  ArcFitTolerance = 1e-06
  AttachmentSupport = -> [XY_Plane010]
  FullyConstrained = true
  MakeInternals = false
  MapMode = 5
  sketch-geometry (6):
    g0: LineSegment StartX=-51 StartY=73 StartZ=0 EndX=-51 EndY=-73 EndZ=0
    g1: LineSegment StartX=-51 StartY=-73 StartZ=0 EndX=51 EndY=-73 EndZ=0
    g2: LineSegment StartX=51 StartY=-73 StartZ=0 EndX=51 EndY=73 EndZ=0
    g3: LineSegment StartX=51 StartY=73 StartZ=0 EndX=-51 EndY=73 EndZ=0
    g4: LineSegment [constr] StartX=-51 StartY=73 StartZ=0 EndX=51 EndY=-73 EndZ=0
    g5: LineSegment [constr] StartX=51 StartY=73 StartZ=0 EndX=-51 EndY=-73 EndZ=0
  constraints (16):
    c: Coincident(g0,g1)
    c: Coincident(g1,g2)
    c: Coincident(g2,g3)
    c: Coincident(g3,g0)
    c: Vertical(g0)
    c: Vertical(g2)
    c: Horizontal(g1)
    c: Horizontal(g3)
    c: Coincident(g4,g0)
    c: Coincident(g4,g1)
    c: Coincident(g5,g2)
    c: Coincident(g5,g0)
    c: PointOnObject(g-1,g4)
    c: PointOnObject(g-1,g5)
    c: DistanceY(g0,g0) = 146
    c: DistanceX(g1,g1) = 102
FEATURE [PartDesign::Pad] Pad012
  Direction = (0,0,1)
  Length = 26
  Length2 = 10
  Profile = -> Sketch046
  ReferenceAxis = -> Sketch046 [N_Axis]
  Suppressed = false
  Type = 0
FEATURE [Sketcher::SketchObject] Sketch047
  ArcFitTolerance = 1e-06
  AttachmentSupport = -> [Pad012]
  FullyConstrained = false
  MakeInternals = false
  MapMode = 5
  Placement = pos=(51,0,0) rot=(0.57735,0.57735,0.57735;2.0944rad)
  sketch-geometry (8):
    g0: LineSegment [constr] StartX=-105.942 StartY=6 StartZ=0 EndX=159.863 EndY=6 EndZ=0
    g1: LineSegment [constr] StartX=-56.6 StartY=54.0105 StartZ=0 EndX=-56.6 EndY=-51.0272 EndZ=0
    g2: LineSegment [constr] StartX=45 StartY=52.761 StartZ=0 EndX=45 EndY=-27.7374 EndZ=0
    g3: LineSegment [constr] StartX=3.4 StartY=51.9731 StartZ=0 EndX=3.4 EndY=-32.6534 EndZ=0
    g4: Circle CenterX=45 CenterY=6 CenterZ=0 NormalX=0 NormalY=0 NormalZ=1 AngleXU=0 Radius=2
    g5: Circle CenterX=3.4 CenterY=6 CenterZ=0 NormalX=0 NormalY=0 NormalZ=1 AngleXU=0 Radius=2
    g6: Circle CenterX=-56.6 CenterY=6 CenterZ=0 NormalX=0 NormalY=0 NormalZ=1 AngleXU=0 Radius=2
    g7: LineSegment [constr] StartX=73 StartY=47.2374 StartZ=0 EndX=73 EndY=-20.359 EndZ=0
  constraints (19):
    c: Horizontal(g0)
    c: Distance(g0,g-1) = 6
    c: Vertical(g1)
    c: Vertical(g2)
    c: Vertical(g3)
    c: PointOnObject(g4,g0)
    c: PointOnObject(g5,g0)
    c: PointOnObject(g6,g0)
    c: Diameter(g5) = 4
    c: Equal(g4,g6)
    c: Equal(g6,g5)
    c: PointOnObject(g4,g2)
    c: PointOnObject(g5,g3)
    c: PointOnObject(g6,g1)
    c: Distance(g2,g3) = 41.6
    c: Distance(g1,g3) = 60
    c: Vertical(g7)
    c: DistanceX(g-1,g7) = 73
    c: DistanceX(g2,g7) = 28
FEATURE [PartDesign::Pocket] Pocket033
  BaseFeature = -> Pad012
  Direction = (-1,0,0)
  Length = 5
  Length2 = 5
  Profile = -> Sketch047
  ReferenceAxis = -> Sketch047 [N_Axis]
  Suppressed = false
  Type = 1
FEATURE [PartDesign::Chamfer] Chamfer001
  Angle = 45
  Base = -> Pocket033 [Face3,Face4]
  BaseFeature = -> Pocket033
  ChamferType = 0
  FlipDirection = false
  Size = 2
  Size2 = 1
  SupportTransform = false
  Suppressed = false
  UseAllEdges = false
FEATURE [PartDesign::Body] Body010  label="HDD"
  AllowCompound = false
  Group = -> [Sketch046,Pad012,Sketch047,Pocket033,Chamfer001]
  Origin = -> Origin010
  Placement = pos=(63.5,58.3,8) rot=(0,0,1;3.14159rad)
  Tip = -> Chamfer001
FEATURE [Sketcher::SketchObject] Sketch048
  ArcFitTolerance = 1e-06
  AttachmentSupport = -> [XY_Plane011]
  FullyConstrained = true
  MakeInternals = false
  MapMode = 5
  sketch-geometry (6):
    g0: LineSegment StartX=-51 StartY=73 StartZ=0 EndX=-51 EndY=-73 EndZ=0
    g1: LineSegment StartX=-51 StartY=-73 StartZ=0 EndX=51 EndY=-73 EndZ=0
    g2: LineSegment StartX=51 StartY=-73 StartZ=0 EndX=51 EndY=73 EndZ=0
    g3: LineSegment StartX=51 StartY=73 StartZ=0 EndX=-51 EndY=73 EndZ=0
    g4: LineSegment [constr] StartX=-51 StartY=73 StartZ=0 EndX=51 EndY=-73 EndZ=0
    g5: LineSegment [constr] StartX=51 StartY=73 StartZ=0 EndX=-51 EndY=-73 EndZ=0
  constraints (16):
    c: Coincident(g0,g1)
    c: Coincident(g1,g2)
    c: Coincident(g2,g3)
    c: Coincident(g3,g0)
    c: Vertical(g0)
    c: Vertical(g2)
    c: Horizontal(g1)
    c: Horizontal(g3)
    c: Coincident(g4,g0)
    c: Coincident(g4,g1)
    c: Coincident(g5,g2)
    c: Coincident(g5,g0)
    c: PointOnObject(g-1,g4)
    c: PointOnObject(g-1,g5)
    c: DistanceY(g0,g0) = 146
    c: DistanceX(g1,g1) = 102
FEATURE [PartDesign::Pad] Pad013
  Direction = (0,0,1)
  Length = 26
  Length2 = 10
  Profile = -> Sketch048
  ReferenceAxis = -> Sketch048 [N_Axis]
  Suppressed = false
  Type = 0
FEATURE [Sketcher::SketchObject] Sketch049
  ArcFitTolerance = 1e-06
  AttachmentSupport = -> [Pad013]
  FullyConstrained = false
  MakeInternals = false
  MapMode = 5
  Placement = pos=(51,0,0) rot=(0.57735,0.57735,0.57735;2.0944rad)
  sketch-geometry (8):
    g0: LineSegment [constr] StartX=-105.942 StartY=6 StartZ=0 EndX=159.863 EndY=6 EndZ=0
    g1: LineSegment [constr] StartX=-56.6 StartY=54.0105 StartZ=0 EndX=-56.6 EndY=-51.0272 EndZ=0
    g2: LineSegment [constr] StartX=45 StartY=52.761 StartZ=0 EndX=45 EndY=-27.7374 EndZ=0
    g3: LineSegment [constr] StartX=3.4 StartY=51.9731 StartZ=0 EndX=3.4 EndY=-32.6534 EndZ=0
    g4: Circle CenterX=45 CenterY=6 CenterZ=0 NormalX=0 NormalY=0 NormalZ=1 AngleXU=0 Radius=2
    g5: Circle CenterX=3.4 CenterY=6 CenterZ=0 NormalX=0 NormalY=0 NormalZ=1 AngleXU=0 Radius=2
    g6: Circle CenterX=-56.6 CenterY=6 CenterZ=0 NormalX=0 NormalY=0 NormalZ=1 AngleXU=0 Radius=2
    g7: LineSegment [constr] StartX=73 StartY=47.2374 StartZ=0 EndX=73 EndY=-20.359 EndZ=0
  constraints (19):
    c: Horizontal(g0)
    c: Distance(g0,g-1) = 6
    c: Vertical(g1)
    c: Vertical(g2)
    c: Vertical(g3)
    c: PointOnObject(g4,g0)
    c: PointOnObject(g5,g0)
    c: PointOnObject(g6,g0)
    c: Diameter(g5) = 4
    c: Equal(g4,g6)
    c: Equal(g6,g5)
    c: PointOnObject(g4,g2)
    c: PointOnObject(g5,g3)
    c: PointOnObject(g6,g1)
    c: Distance(g2,g3) = 41.6
    c: Distance(g1,g3) = 60
    c: Vertical(g7)
    c: DistanceX(g-1,g7) = 73
    c: DistanceX(g2,g7) = 28
FEATURE [PartDesign::Pocket] Pocket034
  BaseFeature = -> Pad013
  Direction = (-1,0,0)
  Length = 5
  Length2 = 5
  Profile = -> Sketch049
  ReferenceAxis = -> Sketch049 [N_Axis]
  Suppressed = false
  Type = 1
FEATURE [PartDesign::Chamfer] Chamfer002
  Angle = 45
  Base = -> Pocket034 [Face3,Face4]
  BaseFeature = -> Pocket034
  ChamferType = 0
  FlipDirection = false
  Size = 2
  Size2 = 1
  SupportTransform = false
  Suppressed = false
  UseAllEdges = false
FEATURE [PartDesign::Body] Body011  label="HDD_Inverted"
  AllowCompound = false
  Group = -> [Sketch048,Pad013,Sketch049,Pocket034,Chamfer002]
  Origin = -> Origin011
  Placement = pos=(63.5,58.3,8) rot=(0,0,1;0rad)
  Tip = -> Chamfer002
FEATURE [Sketcher::SketchObject] Sketch056
  ArcFitTolerance = 1e-06
  AttachmentSupport = -> [XY_Plane014]
  FullyConstrained = true
  MakeInternals = false
  MapMode = 5
  sketch-geometry (6):
    g0: LineSegment StartX=-35 StartY=50 StartZ=0 EndX=-35 EndY=-50 EndZ=0
    g1: LineSegment StartX=-35 StartY=-50 StartZ=0 EndX=35 EndY=-50 EndZ=0
    g2: LineSegment StartX=35 StartY=-50 StartZ=0 EndX=35 EndY=50 EndZ=0
    g3: LineSegment StartX=35 StartY=50 StartZ=0 EndX=-35 EndY=50 EndZ=0
    g4: LineSegment [constr] StartX=-35 StartY=50 StartZ=0 EndX=35 EndY=-50 EndZ=0
    g5: LineSegment [constr] StartX=35 StartY=50 StartZ=0 EndX=-35 EndY=-50 EndZ=0
  constraints (16):
    c: Coincident(g0,g1)
    c: Coincident(g1,g2)
    c: Coincident(g2,g3)
    c: Coincident(g3,g0)
    c: Vertical(g0)
    c: Vertical(g2)
    c: Horizontal(g1)
    c: Horizontal(g3)
    c: Coincident(g4,g0)
    c: Coincident(g4,g1)
    c: Coincident(g5,g2)
    c: Coincident(g5,g0)
    c: PointOnObject(g-1,g4)
    c: PointOnObject(g-1,g5)
    c: DistanceY(g0,g0) = 100
    c: DistanceX(g1,g1) = 70
FEATURE [PartDesign::Pad] Pad018
  Direction = (0,0,1)
  Length = 10
  Length2 = 10
  Profile = -> Sketch056
  ReferenceAxis = -> Sketch056 [N_Axis]
  Suppressed = false
  Type = 0
FEATURE [Sketcher::SketchObject] Sketch057
  ArcFitTolerance = 1e-06
  AttachmentSupport = -> [Pad018]
  FullyConstrained = false
  MakeInternals = false
  MapMode = 5
  Placement = pos=(35,0,0) rot=(0.57735,0.57735,0.57735;2.0944rad)
  sketch-geometry (6):
    g0: LineSegment [constr] StartX=-63.1237 StartY=3 StartZ=0 EndX=159.863 EndY=3 EndZ=0
    g1: LineSegment [constr] StartX=36 StartY=18.9953 StartZ=0 EndX=36 EndY=-27.7374 EndZ=0
    g2: LineSegment [constr] StartX=-41 StartY=50.9008 StartZ=0 EndX=-41 EndY=-33.7257 EndZ=0
    g3: Circle CenterX=36 CenterY=3 CenterZ=0 NormalX=0 NormalY=0 NormalZ=1 AngleXU=0 Radius=1.5
    g4: Circle CenterX=-41 CenterY=3 CenterZ=0 NormalX=0 NormalY=0 NormalZ=1 AngleXU=0 Radius=1.5
    g5: LineSegment [constr] StartX=50 StartY=21.3406 StartZ=0 EndX=50 EndY=-20.359 EndZ=0
  constraints (14):
    c: Horizontal(g0)
    c: Distance(g0,g-1) = 3
    c: Vertical(g1)
    c: Vertical(g2)
    c: PointOnObject(g3,g0)
    c: PointOnObject(g4,g0)
    c: Diameter(g4) = 3
    c: PointOnObject(g3,g1)
    c: PointOnObject(g4,g2)
    c: Vertical(g5)
    c: DistanceX(g-1,g5) = 50
    c: DistanceX(g1,g5) = 14
    c: DistanceX(g2,g1) = 77
    c: Equal(g3,g4)
FEATURE [PartDesign::Pocket] Pocket038
  BaseFeature = -> Pad018
  Direction = (-1,0,0)
  Length = 5
  Length2 = 5
  Profile = -> Sketch057
  ReferenceAxis = -> Sketch057 [N_Axis]
  Suppressed = false
  Type = 1
FEATURE [Sketcher::SketchObject] Sketch058
  ArcFitTolerance = 1e-06
  AttachmentSupport = -> [XZ_Plane015]
  FullyConstrained = false
  MakeInternals = false
  MapMode = 5
  Placement = pos=(0,0,0) rot=(1,0,0;1.5708rad)
  sketch-geometry (42):
    g0: LineSegment StartX=0 StartY=105 StartZ=0 EndX=0 EndY=0 EndZ=0
    g1: LineSegment StartX=0 StartY=0 StartZ=0 EndX=119 EndY=0 EndZ=0
    g2: LineSegment StartX=119 StartY=0 StartZ=0 EndX=119 EndY=105 EndZ=0
    g3: LineSegment StartX=119 StartY=105 StartZ=0 EndX=0 EndY=105 EndZ=0
    g4: LineSegment [constr] StartX=-9.32161 StartY=84.9 StartZ=0 EndX=161.836 EndY=84.9 EndZ=0
    g5: LineSegment [constr] StartX=152.139 StartY=72.6 StartZ=0 EndX=-13.3622 EndY=72.6 EndZ=0
    g6: LineSegment [constr] StartX=164.729 StartY=20.3 StartZ=0 EndX=-32.1103 EndY=20.3 EndZ=0
    g7: LineSegment [constr] StartX=-25.0153 StartY=8 StartZ=0 EndX=165.23 EndY=8 EndZ=0
    g8: LineSegment [constr] StartX=-16.2877 StartY=52.6 StartZ=0 EndX=151.152 EndY=52.6 EndZ=0
    g9: LineSegment [constr] StartX=-11.4391 StartY=40.3 StartZ=0 EndX=151.314 EndY=40.3 EndZ=0
    g10: LineSegment StartX=4.5 StartY=20.3 StartZ=0 EndX=8 EndY=20.3 EndZ=0
    g11: LineSegment StartX=8 StartY=20.3 StartZ=0 EndX=8 EndY=40.3 EndZ=0
    g12: LineSegment StartX=8 StartY=40.3 StartZ=0 EndX=4.5 EndY=40.3 EndZ=0
    g13: LineSegment StartX=4.5 StartY=40.3 StartZ=0 EndX=4.5 EndY=52.6 EndZ=0
    g14: LineSegment StartX=4.5 StartY=52.6 StartZ=0 EndX=8 EndY=52.6 EndZ=0
    g15: LineSegment StartX=8 StartY=52.6 StartZ=0 EndX=8 EndY=72.6 EndZ=0
    g16: LineSegment StartX=8 StartY=72.6 StartZ=0 EndX=4.5 EndY=72.6 EndZ=0
    g17: LineSegment StartX=4.5 StartY=72.6 StartZ=0 EndX=4.5 EndY=84.9 EndZ=0
    g18: LineSegment StartX=4.5 StartY=84.9 StartZ=0 EndX=8 EndY=84.9 EndZ=0
    g19: LineSegment StartX=8 StartY=84.9 StartZ=0 EndX=8 EndY=100 EndZ=0
    g20: LineSegment StartX=8 StartY=100 StartZ=0 EndX=111 EndY=100 EndZ=0
    g21: LineSegment StartX=111 StartY=100 StartZ=0 EndX=111 EndY=84.9 EndZ=0
    g22: LineSegment StartX=111 StartY=84.9 StartZ=0 EndX=114.5 EndY=84.9 EndZ=0
    g23: LineSegment StartX=114.5 StartY=84.9 StartZ=0 EndX=114.5 EndY=72.6 EndZ=0
    g24: LineSegment StartX=114.5 StartY=72.6 StartZ=0 EndX=111 EndY=72.6 EndZ=0
    g25: LineSegment StartX=111 StartY=72.6 StartZ=0 EndX=111 EndY=52.6 EndZ=0
    g26: LineSegment StartX=111 StartY=52.6 StartZ=0 EndX=114.5 EndY=52.6 EndZ=0
    g27: LineSegment StartX=114.5 StartY=52.6 StartZ=0 EndX=114.5 EndY=40.3 EndZ=0
    g28: LineSegment StartX=114.5 StartY=40.3 StartZ=0 EndX=111 EndY=40.3 EndZ=0
    g29: LineSegment StartX=111 StartY=40.3 StartZ=0 EndX=111 EndY=20.3 EndZ=0
    g30: LineSegment StartX=111 StartY=20.3 StartZ=0 EndX=114.5 EndY=20.3 EndZ=0
    g31: LineSegment StartX=114.5 StartY=20.3 StartZ=0 EndX=114.5 EndY=8 EndZ=0
    g32: LineSegment StartX=114.5 StartY=8 StartZ=0 EndX=111 EndY=8 EndZ=0
    g33: LineSegment StartX=111 StartY=8 StartZ=0 EndX=111 EndY=5 EndZ=0
    g34: LineSegment StartX=111 StartY=5 StartZ=0 EndX=8 EndY=5 EndZ=0
    g35: LineSegment StartX=8 StartY=5 StartZ=0 EndX=8 EndY=8 EndZ=0
    g36: LineSegment StartX=8 StartY=8 StartZ=0 EndX=4.5 EndY=8 EndZ=0
    g37: LineSegment StartX=4.5 StartY=8 StartZ=0 EndX=4.5 EndY=20.3 EndZ=0
    g38: LineSegment [constr] StartX=8 StartY=126.141 StartZ=0 EndX=8 EndY=-39.2934 EndZ=0
    g39: LineSegment [constr] StartX=111 StartY=118.544 StartZ=0 EndX=111 EndY=-9.87825 EndZ=0
    g40: LineSegment [constr] StartX=4.5 StartY=128.242 StartZ=0 EndX=4.5 EndY=-35.0913 EndZ=0
    g41: LineSegment [constr] StartX=114.5 StartY=121.938 StartZ=0 EndX=114.5 EndY=-10.3631 EndZ=0
  constraints (116):
    c: Coincident(g0,g1)
    c: Coincident(g1,g2)
    c: Coincident(g2,g3)
    c: Coincident(g3,g0)
    c: Vertical(g0)
    c: Vertical(g2)
    c: Horizontal(g1)
    c: Horizontal(g3)
    c: PointOnObject(g0,g-2)
    c: PointOnObject(g1,g-1)
    c: DistanceX(g3,g3) = 119
    c: DistanceY(g2,g2) = 105
    c: Horizontal(g4)
    c: Horizontal(g5)
    c: Horizontal(g6)
    c: Horizontal(g7)
    c: Horizontal(g8)
    c: Distance(g4,g5) = 12.3
    c: Horizontal(g9)
    c: DistanceY(g9,g8) = 12.3
    c: DistanceY(g7,g6) = 12.3
    c: DistanceY(g6,g9) = 20
    c: DistanceY(g8,g5) = 20
    c: DistanceY(g0,g7) = 8
    c: PointOnObject(g10,g6)
    c: PointOnObject(g10,g6)
    c: Coincident(g10,g11)
    c: PointOnObject(g11,g9)
    c: Vertical(g11)
    c: Coincident(g11,g12)
    c: PointOnObject(g12,g9)
    c: Coincident(g12,g13)
    c: PointOnObject(g13,g8)
    c: Vertical(g13)
    c: Coincident(g13,g14)
    c: PointOnObject(g14,g8)
    c: Coincident(g14,g15)
    c: PointOnObject(g15,g5)
    c: Coincident(g15,g16)
    c: PointOnObject(g16,g5)
    c: Coincident(g16,g17)
    c: PointOnObject(g17,g4)
    c: Coincident(g17,g18)
    c: PointOnObject(g18,g4)
    c: Coincident(g18,g19)
    c: Vertical(g19)
    c: Coincident(g19,g20)
    c: Horizontal(g20)
    c: Coincident(g20,g21)
    c: PointOnObject(g21,g4)
    c: Vertical(g21)
    c: Coincident(g21,g22)
    c: PointOnObject(g22,g4)
    c: Coincident(g22,g23)
    c: PointOnObject(g23,g5)
    c: Vertical(g23)
    c: Coincident(g23,g24)
    c: PointOnObject(g24,g5)
    c: Coincident(g24,g25)
    c: PointOnObject(g25,g8)
    c: Coincident(g25,g26)
    c: PointOnObject(g26,g8)
    c: Coincident(g26,g27)
    c: PointOnObject(g27,g9)
    c: Coincident(g27,g28)
    c: PointOnObject(g28,g9)
    c: Coincident(g28,g29)
    c: PointOnObject(g29,g6)
    c: Coincident(g29,g30)
    c: PointOnObject(g30,g6)
    c: Coincident(g30,g31)
    c: PointOnObject(g31,g7)
    c: Vertical(g31)
    c: Coincident(g31,g32)
    c: PointOnObject(g32,g7)
    c: Coincident(g32,g33)
    c: Coincident(g33,g34)
    c: Horizontal(g34)
    c: Coincident(g34,g35)
    c: PointOnObject(g35,g7)
    c: Coincident(g35,g36)
    c: PointOnObject(g36,g7)
    c: Coincident(g36,g37)
    c: Coincident(g37,g10)
    c: Vertical(g38)
    c: Vertical(g39)
    c: Vertical(g15)
    c: Vertical(g37)
    c: Vertical(g17)
    c: PointOnObject(g11,g38)
    c: PointOnObject(g15,g38)
    c: PointOnObject(g18,g38)
    c: PointOnObject(g21,g39)
    c: PointOnObject(g24,g39)
    c: Vertical(g25)
    c: PointOnObject(g28,g39)
    c: Vertical(g29)
    c: Vertical(g40)
    c: Vertical(g41)
    c: PointOnObject(g17,g40)
    c: PointOnObject(g13,g40)
    c: PointOnObject(g10,g40)
    c: PointOnObject(g30,g41)
    c: Vertical(g27)
    c: PointOnObject(g26,g41)
    c: PointOnObject(g23,g41)
    c: DistanceX(g40,g38) = 3.5
    c: DistanceX(g39,g41) = 3.5
    c: Vertical(g35)
    c: PointOnObject(g35,g38)
    c: Vertical(g33)
    c: DistanceX(g0,g38) = 8
    c: DistanceX(g39,g1) = 8
    c: PointOnObject(g33,g39)
    c: DistanceY(g0,g34) = 5
    c: DistanceY(g19,g0) = 5
FEATURE [PartDesign::Pad] Pad019
  Direction = (0,-1,2e-16)
  Length = 15
  Length2 = 10
  Placement = pos=(0,0,0) rot=(1,0,0;1.5708rad)
  Profile = -> Sketch058
  ReferenceAxis = -> Sketch058 [N_Axis]
  Suppressed = false
  Type = 0
FEATURE [Sketcher::SketchObject] Sketch059
  ArcFitTolerance = 1e-06
  AttachmentSupport = -> [Pad019]
  FullyConstrained = false
  MakeInternals = false
  MapMode = 5
  Placement = pos=(0,-15,0) rot=(1,0,0;1.5708rad)
  sketch-geometry (15):
    g0: LineSegment [constr] StartX=-53.9072 StartY=99 StartZ=0 EndX=153.961 EndY=99 EndZ=0
    g1: LineSegment [constr] StartX=157.316 StartY=67 StartZ=0 EndX=-52.328 EndY=67 EndZ=0
    g2: LineSegment [constr] StartX=-52.328 StartY=35 StartZ=0 EndX=189.296 EndY=35 EndZ=0
    g3: LineSegment [constr] StartX=168.371 StartY=4 StartZ=0 EndX=-39.2992 EndY=4 EndZ=0
    g4: LineSegment [constr] StartX=4 StartY=126.825 StartZ=0 EndX=4 EndY=-36.4293 EndZ=0
    g5: LineSegment [constr] StartX=119 StartY=130.378 StartZ=0 EndX=119 EndY=-42.3514 EndZ=0
    g6: LineSegment [constr] StartX=115 StartY=140.643 StartZ=0 EndX=115 EndY=-43.141 EndZ=0
    g7: Circle CenterX=4 CenterY=99 CenterZ=0 NormalX=0 NormalY=0 NormalZ=1 AngleXU=0 Radius=2
    g8: Circle CenterX=4 CenterY=67 CenterZ=0 NormalX=0 NormalY=0 NormalZ=1 AngleXU=0 Radius=2
    g9: Circle CenterX=4 CenterY=35 CenterZ=0 NormalX=0 NormalY=0 NormalZ=1 AngleXU=0 Radius=2
    g10: Circle CenterX=115 CenterY=35 CenterZ=0 NormalX=0 NormalY=0 NormalZ=1 AngleXU=0 Radius=2
    g11: Circle CenterX=115 CenterY=67 CenterZ=0 NormalX=0 NormalY=0 NormalZ=1 AngleXU=0 Radius=2
    g12: Circle CenterX=115 CenterY=99 CenterZ=0 NormalX=0 NormalY=0 NormalZ=1 AngleXU=0 Radius=2
    g13: Circle CenterX=4 CenterY=4 CenterZ=0 NormalX=0 NormalY=0 NormalZ=1 AngleXU=0 Radius=2
    g14: Circle CenterX=115 CenterY=4 CenterZ=0 NormalX=0 NormalY=0 NormalZ=1 AngleXU=0 Radius=2
  constraints (38):
    c: Horizontal(g0)
    c: Horizontal(g1)
    c: Horizontal(g2)
    c: Horizontal(g3)
    c: Vertical(g4)
    c: Vertical(g5)
    c: DistanceX(g-1,g4) = 4
    c: Vertical(g6)
    c: DistanceX(g6,g5) = 4
    c: DistanceX(g-1,g5) = 119
    c: DistanceY(g-1,g2) = 35
    c: DistanceY(g3,g2) = 31
    c: DistanceY(g2,g1) = 32
    c: DistanceY(g1,g0) = 32
    c: PointOnObject(g7,g4)
    c: Diameter(g7) = 4
    c: PointOnObject(g8,g4)
    c: PointOnObject(g9,g4)
    c: PointOnObject(g10,g6)
    c: PointOnObject(g11,g6)
    c: PointOnObject(g12,g6)
    c: PointOnObject(g13,g4)
    c: PointOnObject(g14,g6)
    c: Equal(g14,g13)
    c: Equal(g13,g10)
    c: Equal(g10,g9)
    c: Equal(g9,g8)
    c: Equal(g8,g11)
    c: Equal(g11,g12)
    c: Equal(g12,g7)
    c: PointOnObject(g8,g1)
    c: PointOnObject(g9,g2)
    c: PointOnObject(g13,g3)
    c: PointOnObject(g14,g3)
    c: PointOnObject(g10,g2)
    c: PointOnObject(g11,g1)
    c: PointOnObject(g12,g0)
    c: PointOnObject(g7,g0)
FEATURE [PartDesign::Pocket] Pocket039
  BaseFeature = -> Pad019
  Direction = (0,1,-2e-16)
  Length = 5
  Length2 = 5
  Placement = pos=(0,0,0) rot=(1,0,0;1.5708rad)
  Profile = -> Sketch059
  ReferenceAxis = -> Sketch059 [N_Axis]
  Suppressed = false
  Type = 1
FEATURE [Sketcher::SketchObject] Sketch060
  ArcFitTolerance = 1e-06
  AttachmentSupport = -> [Pocket039]
  FullyConstrained = false
  MakeInternals = false
  MapMode = 5
  Placement = pos=(0,-15,0) rot=(1,0,0;1.5708rad)
  sketch-geometry (12):
    g0: LineSegment [constr] StartX=4 StartY=121.766 StartZ=0 EndX=4 EndY=-28.0641 EndZ=0
    g1: LineSegment [constr] StartX=115 StartY=133.117 StartZ=0 EndX=115 EndY=-24.6096 EndZ=0
    g2: LineSegment [constr] StartX=-20.9224 StartY=89 StartZ=0 EndX=165.823 EndY=89 EndZ=0
    g3: LineSegment [constr] StartX=140.95 StartY=57 StartZ=0 EndX=-25.0679 EndY=57 EndZ=0
    g4: LineSegment [constr] StartX=-28.8186 StartY=25 StartZ=0 EndX=176.878 EndY=25 EndZ=0
    g5: LineSegment [constr] StartX=119 StartY=134.697 StartZ=0 EndX=119 EndY=-24.2147 EndZ=0
    g6: Circle CenterX=4 CenterY=25 CenterZ=0 NormalX=0 NormalY=0 NormalZ=1 AngleXU=0 Radius=2.25
    g7: Circle CenterX=115 CenterY=25 CenterZ=0 NormalX=0 NormalY=0 NormalZ=1 AngleXU=0 Radius=2.25
    g8: Circle CenterX=115 CenterY=57 CenterZ=0 NormalX=0 NormalY=0 NormalZ=1 AngleXU=0 Radius=2.25
    g9: Circle CenterX=115 CenterY=89 CenterZ=0 NormalX=0 NormalY=0 NormalZ=1 AngleXU=0 Radius=2.25
    g10: Circle CenterX=4 CenterY=89 CenterZ=0 NormalX=0 NormalY=0 NormalZ=1 AngleXU=0 Radius=2.25
    g11: Circle CenterX=4 CenterY=57 CenterZ=0 NormalX=0 NormalY=0 NormalZ=1 AngleXU=0 Radius=2.25
  constraints (30):
    c: Vertical(g0)
    c: Vertical(g1)
    c: Horizontal(g2)
    c: Horizontal(g3)
    c: Horizontal(g4)
    c: DistanceY(g-1,g4) = 25
    c: DistanceY(g4,g3) = 32
    c: DistanceY(g3,g2) = 32
    c: DistanceX(g-1,g0) = 4
    c: Vertical(g5)
    c: DistanceX(g-1,g5) = 119
    c: DistanceX(g1,g5) = 4
    c: PointOnObject(g6,g0)
    c: PointOnObject(g7,g1)
    c: PointOnObject(g8,g1)
    c: PointOnObject(g9,g1)
    c: PointOnObject(g10,g0)
    c: PointOnObject(g11,g0)
    c: Diameter(g10) = 4.5
    c: Equal(g10,g11)
    c: Equal(g11,g6)
    c: Equal(g6,g7)
    c: Equal(g7,g8)
    c: Equal(g8,g9)
    c: PointOnObject(g11,g3)
    c: PointOnObject(g10,g2)
    c: PointOnObject(g6,g4)
    c: PointOnObject(g7,g4)
    c: PointOnObject(g8,g3)
    c: PointOnObject(g9,g2)
FEATURE [PartDesign::Pocket] Pocket040
  BaseFeature = -> Pocket039
  Direction = (0,1,-2e-16)
  Length = 6
  Length2 = 5
  Placement = pos=(0,0,0) rot=(1,0,0;1.5708rad)
  Profile = -> Sketch060
  ReferenceAxis = -> Sketch060 [N_Axis]
  Suppressed = false
  Type = 0
FEATURE [PartDesign::Hole] Hole007
  BaseFeature = -> Pocket040
  CustomThreadClearance = 0
  Depth = 4
  DepthType = 0
  Diameter = 6.5
  DrillForDepth = false
  DrillPoint = 0
  DrillPointAngle = 118
  HoleCutCountersinkAngle = 90
  HoleCutCustomValues = false
  HoleCutDepth = 0
  HoleCutDiameter = 6.6
  HoleCutType = 0
  ModelThread = false
  Placement = pos=(0,0,0) rot=(1,0,0;1.5708rad)
  Profile = -> Pocket040 [Edge55,Edge53,Edge51,Edge49,Edge90,Edge88,Edge86,Edge84]
  Reversed = true
  Suppressed = false
  Tapered = false
  TaperedAngle = 90
  ThreadClass = 0
  ThreadDepth = 4
  ThreadDepthType = 0
  ThreadDirection = 0
  ThreadFit = 0
  ThreadSize = 0
  ThreadType = 0
  Threaded = false
  UseCustomThreadClearance = false
FEATURE [Sketcher::SketchObject] Sketch062
  ArcFitTolerance = 1e-06
  AttachmentSupport = -> [XZ_Plane016]
  FullyConstrained = false
  MakeInternals = false
  MapMode = 5
  Placement = pos=(0,0,0) rot=(1,0,0;1.5708rad)
  sketch-geometry (31):
    g0: LineSegment StartX=4 StartY=0 StartZ=0 EndX=-125.536 EndY=0 EndZ=0
    g1: LineSegment StartX=-125.536 StartY=0 StartZ=0 EndX=-125.536 EndY=-1.01 EndZ=0
    g2: LineSegment StartX=-125.536 StartY=-1.01 StartZ=0 EndX=-128.536 EndY=-1.01 EndZ=0
    g3: LineSegment StartX=-128.536 StartY=-1.01 StartZ=0 EndX=-128.536 EndY=0 EndZ=0
    g4: LineSegment StartX=-128.536 StartY=0 StartZ=0 EndX=-141.92 EndY=0 EndZ=0
    g5: LineSegment StartX=-141.92 StartY=0 StartZ=0 EndX=-141.92 EndY=-3.3955 EndZ=0
    g6: LineSegment StartX=-141.92 StartY=-3.3955 StartZ=0 EndX=-147.92 EndY=-3.3955 EndZ=0
    g7: LineSegment StartX=-147.92 StartY=-3.3955 StartZ=0 EndX=-147.92 EndY=3.2 EndZ=0
    g8: LineSegment StartX=-147.92 StartY=3.2 StartZ=0 EndX=-124.257 EndY=3.2 EndZ=0
    g9: LineSegment StartX=-124.257 StartY=3.2 StartZ=0 EndX=-124.257 EndY=8.8 EndZ=0
    g10: LineSegment StartX=-124.257 StartY=8.8 StartZ=0 EndX=-147.92 EndY=8.8 EndZ=0
    g11: LineSegment StartX=-147.92 StartY=8.8 StartZ=0 EndX=-147.92 EndY=16.6996 EndZ=0
    g12: LineSegment StartX=-147.92 StartY=16.6996 StartZ=0 EndX=-141.92 EndY=16.6996 EndZ=0
    g13: LineSegment StartX=-141.92 StartY=16.6996 StartZ=0 EndX=-141.92 EndY=12 EndZ=0
    g14: LineSegment StartX=-141.92 StartY=12 StartZ=0 EndX=-128.536 EndY=12 EndZ=0
    g15: LineSegment StartX=-128.536 StartY=12 StartZ=0 EndX=-128.536 EndY=13.01 EndZ=0
    g16: LineSegment StartX=-128.536 StartY=13.01 StartZ=0 EndX=-125.536 EndY=13.01 EndZ=0
    g17: LineSegment StartX=-125.536 StartY=13.01 StartZ=0 EndX=-125.536 EndY=12 EndZ=0
    g18: LineSegment StartX=-125.536 StartY=12 StartZ=0 EndX=4 EndY=12 EndZ=0
    g19: LineSegment StartX=4 StartY=12 StartZ=0 EndX=4 EndY=0 EndZ=0
    g20: LineSegment [constr] StartX=-177.942 StartY=12 StartZ=0 EndX=14.5003 EndY=12 EndZ=0
    g21: LineSegment [constr] StartX=-125.536 StartY=27.4193 StartZ=0 EndX=-125.536 EndY=-18.7719 EndZ=0
    g22: LineSegment [constr] StartX=-141.92 StartY=22.481 StartZ=0 EndX=-141.92 EndY=-16.4674 EndZ=0
    g23: LineSegment [constr] StartX=-147.92 StartY=19.6726 StartZ=0 EndX=-147.92 EndY=-22.0842 EndZ=0
    g24: Circle CenterX=-66 CenterY=6 CenterZ=0 NormalX=0 NormalY=0 NormalZ=1 AngleXU=0 Radius=1.9
    g25: Circle CenterX=-6 CenterY=6 CenterZ=0 NormalX=0 NormalY=0 NormalZ=1 AngleXU=0 Radius=1.9
    g26: LineSegment [constr] StartX=-174.191 StartY=6 StartZ=0 EndX=-2.85094 EndY=6 EndZ=0
    g27: Circle CenterX=-107.6 CenterY=6 CenterZ=0 NormalX=0 NormalY=0 NormalZ=1 AngleXU=0 Radius=1.9
    g28: Circle CenterX=-17.6 CenterY=6 CenterZ=0 NormalX=0 NormalY=0 NormalZ=1 AngleXU=0 Radius=1.9
    g29: Circle CenterX=-59.2 CenterY=6 CenterZ=0 NormalX=0 NormalY=0 NormalZ=1 AngleXU=0 Radius=1.9
    g30: Circle CenterX=-119.3 CenterY=6 CenterZ=0 NormalX=0 NormalY=0 NormalZ=1 AngleXU=0 Radius=1.9
  constraints (86):
    c: PointOnObject(g0,g-1)
    c: Coincident(g0,g1)
    c: Coincident(g1,g2)
    c: Coincident(g2,g3)
    c: PointOnObject(g3,g-1)
    c: Coincident(g3,g4)
    c: Horizontal(g4)
    c: Coincident(g4,g5)
    c: Coincident(g5,g6)
    c: Coincident(g6,g7)
    c: Coincident(g7,g8)
    c: Horizontal(g8)
    c: Coincident(g8,g9)
    c: Coincident(g9,g10)
    c: Horizontal(g10)
    c: Coincident(g10,g11)
    c: Coincident(g11,g12)
    c: Coincident(g12,g13)
    c: Coincident(g13,g14)
    c: Horizontal(g14)
    c: Coincident(g14,g15)
    c: Coincident(g15,g16)
    c: Horizontal(g16)
    c: Coincident(g16,g17)
    c: Coincident(g17,g18)
    c: Horizontal(g18)
    c: Coincident(g18,g19)
    c: Coincident(g19,g0)
    c: Vertical(g7)
    c: Vertical(g11)
    c: Horizontal(g12)
    c: Horizontal(g6)
    c: Horizontal(g20)
    c: PointOnObject(g17,g20)
    c: PointOnObject(g14,g20)
    c: DistanceY(g0,g20) = 12
    c: Vertical(g15)
    c: Vertical(g17)
    c: Vertical(g1)
    c: Vertical(g3)
    c: Horizontal(g2)
    c: Vertical(g21)
    c: PointOnObject(g0,g21)
    c: PointOnObject(g17,g21)
    c: DistanceX(g16,g16) = 3
    c: DistanceY(g15,g15) = 1.01
    c: DistanceX(g2,g2) = 3
    c: DistanceY(g3,g3) = 1.01
    c: Vertical(g13)
    c: Vertical(g5)
    c: Vertical(g22)
    c: Vertical(g23)
    c: PointOnObject(g7,g23)
    c: PointOnObject(g10,g23)
    c: PointOnObject(g13,g22)
    c: PointOnObject(g4,g22)
    c: DistanceX(g12,g12) = 6
    c: Vertical(g9)
    c: Distance(g8,g-1) = 3.2
    c: Distance(g9,g20) = 3.2
    c: Diameter(g24) = 3.8
    c: Diameter(g25) = 3.8
    c: Horizontal(g26)
    c: PointOnObject(g24,g26)
    c: PointOnObject(g25,g26)
    c: DistanceY(g0,g26) = 6
    c: DistanceX(g24,g25) = 60
    c: PointOnObject(g27,g26)
    c: Diameter(g27) = 3.8
    c: DistanceX(g27,g25) = 101.6
    c: DistanceX(g25,g0) = 10
    c: Horizontal(g0)
    c: Vertical(g19)
    c: Distance(g-1,g0) = 4
    c: DistanceX(g27,g24) = 41.6
    c: DistanceX(g24,g25) = 60
    c: DistanceX(g9,g27) = 16.6574
    c: PointOnObject(g28,g26)
    c: PointOnObject(g29,g26)
    c: DistanceX(g29,g28) = 41.6
    c: Equal(g24,g29)
    c: Equal(g29,g28)
    c: DistanceX(g28,g25) = 11.6
    c: PointOnObject(g30,g26)
    c: Equal(g27,g30)
    c: DistanceX(g30,g27) = 11.7
FEATURE [PartDesign::Pad] Pad020
  Direction = (0,-1,2e-16)
  Length = 4
  Length2 = 6
  Placement = pos=(0,0,0) rot=(1,0,0;1.5708rad)
  Profile = -> Sketch062
  ReferenceAxis = -> Sketch062 [N_Axis]
  Suppressed = false
  Type = 0
FEATURE [Sketcher::SketchObject] Sketch063
  ArcFitTolerance = 1e-06
  AttachmentSupport = -> [Pad020]
  FullyConstrained = false
  MakeInternals = false
  MapMode = 5
  Placement = pos=(0,1.4e-15,0) rot=(-1,0,0;1.5708rad)
  sketch-geometry (11):
    g0: LineSegment [constr] StartX=-161.488 StartY=-6 StartZ=0 EndX=29.2523 EndY=-6 EndZ=0
    g1: Circle CenterX=-107.6 CenterY=-6 CenterZ=0 NormalX=0 NormalY=0 NormalZ=1 AngleXU=0 Radius=4
    g2: Circle CenterX=-6 CenterY=-6 CenterZ=0 NormalX=0 NormalY=0 NormalZ=1 AngleXU=0 Radius=4
    g3: Circle CenterX=-17.6 CenterY=-6 CenterZ=0 NormalX=0 NormalY=0 NormalZ=1 AngleXU=0 Radius=4
    g4: LineSegment [constr] StartX=-59.2 StartY=-24.7493 StartZ=0 EndX=-59.2 EndY=6.79496 EndZ=0
    g5: LineSegment [constr] StartX=-66 StartY=5.43194 StartZ=0 EndX=-66 EndY=-19.7353 EndZ=0
    g6: ArcOfCircle CenterX=-66.118 CenterY=-6 CenterZ=0 NormalX=0 NormalY=0 NormalZ=1 AngleXU=0 Radius=4 StartAngle=1.5708 EndAngle=4.71239
    g7: ArcOfCircle CenterX=-59.2 CenterY=-6 CenterZ=0 NormalX=0 NormalY=0 NormalZ=1 AngleXU=0 Radius=4 StartAngle=4.71239 EndAngle=7.85398
    g8: LineSegment StartX=-66.118 StartY=-2 StartZ=0 EndX=-59.2 EndY=-2 EndZ=0
    g9: LineSegment StartX=-66.118 StartY=-10 StartZ=0 EndX=-59.2 EndY=-10 EndZ=0
    g10: Circle CenterX=-119.3 CenterY=-6 CenterZ=0 NormalX=0 NormalY=0 NormalZ=1 AngleXU=0 Radius=4
  constraints (26):
    c: Horizontal(g0)
    c: Distance(g-1,g0) = 6
    c: PointOnObject(g1,g0)
    c: PointOnObject(g2,g0)
    c: DistanceX(g2,g-1) = 6
    c: DistanceX(g1,g2) = 101.6
    c: Diameter(g1) = 8
    c: Equal(g2,g1)
    c: PointOnObject(g3,g0)
    c: DistanceX(g3,g-1) = 17.6
    c: Vertical(g4)
    c: Vertical(g5)
    c: Distance(g3,g4) = 41.6
    c: Distance(g2,g5) = 60
    c: Tangent(g6,g8) = 1.5708
    c: Tangent(g6,g9) = -1.5708
    c: Tangent(g7,g8) = 1.5708
    c: Tangent(g7,g9) = -1.5708
    c: Equal(g6,g7)
    c: Symmetric(g0,g0,g6)
    c: PointOnObject(g7,g4)
    c: PointOnObject(g7,g0)
    c: Distance(g9,g8) = 8
    c: PointOnObject(g10,g0)
    c: DistanceX(g10,g1) = 11.7
    c: Equal(g10,g1)
FEATURE [PartDesign::Pocket] Pocket042
  BaseFeature = -> Pad020
  Direction = (0,-1,-2e-16)
  Length = 2.5
  Length2 = 5
  Placement = pos=(0,0,0) rot=(1,0,0;1.5708rad)
  Profile = -> Sketch063
  ReferenceAxis = -> Sketch063 [N_Axis]
  Suppressed = false
  Type = 0
FEATURE [PartDesign::Fillet] Fillet015
  Base = -> Pocket042 [Edge5,Edge1]
  BaseFeature = -> Pocket042
  Placement = pos=(0,0,0) rot=(1,0,0;1.5708rad)
  Radius = 2
  SupportTransform = false
  Suppressed = false
  UseAllEdges = false
FEATURE [PartDesign::Fillet] Fillet016
  Base = -> Fillet015 [Face7,Face14]
  BaseFeature = -> Fillet015
  Placement = pos=(0,0,0) rot=(1,0,0;1.5708rad)
  Radius = 1
  SupportTransform = false
  Suppressed = false
  UseAllEdges = false
FEATURE [PartDesign::Fillet] Fillet017
  Base = -> Fillet016 [Edge76,Edge74,Edge70,Edge56,Edge52,Edge48]
  BaseFeature = -> Fillet016
  Placement = pos=(0,0,0) rot=(1,0,0;1.5708rad)
  Radius = 2
  SupportTransform = false
  Suppressed = false
  UseAllEdges = false
FEATURE [PartDesign::Body] Body016  label="side_V2_01"
  AllowCompound = false
  Group = -> [Sketch062,Pad020,Sketch063,Pocket042,Fillet015,Fillet016,Fillet017]
  Origin = -> Origin016
  Placement = pos=(8.5,121,40.5) rot=(0,0,-1;4.71239rad)
  Tip = -> Fillet017
FEATURE [Sketcher::SketchObject] Sketch064
  ArcFitTolerance = 1e-06
  AttachmentSupport = -> [XY_Plane017]
  FullyConstrained = true
  MakeInternals = false
  MapMode = 5
  sketch-geometry (6):
    g0: LineSegment StartX=-51 StartY=73 StartZ=0 EndX=-51 EndY=-73 EndZ=0
    g1: LineSegment StartX=-51 StartY=-73 StartZ=0 EndX=51 EndY=-73 EndZ=0
    g2: LineSegment StartX=51 StartY=-73 StartZ=0 EndX=51 EndY=73 EndZ=0
    g3: LineSegment StartX=51 StartY=73 StartZ=0 EndX=-51 EndY=73 EndZ=0
    g4: LineSegment [constr] StartX=-51 StartY=73 StartZ=0 EndX=51 EndY=-73 EndZ=0
    g5: LineSegment [constr] StartX=51 StartY=73 StartZ=0 EndX=-51 EndY=-73 EndZ=0
  constraints (16):
    c: Coincident(g0,g1)
    c: Coincident(g1,g2)
    c: Coincident(g2,g3)
    c: Coincident(g3,g0)
    c: Vertical(g0)
    c: Vertical(g2)
    c: Horizontal(g1)
    c: Horizontal(g3)
    c: Coincident(g4,g0)
    c: Coincident(g4,g1)
    c: Coincident(g5,g2)
    c: Coincident(g5,g0)
    c: PointOnObject(g-1,g4)
    c: PointOnObject(g-1,g5)
    c: DistanceY(g0,g0) = 146
    c: DistanceX(g1,g1) = 102
FEATURE [PartDesign::Pad] Pad021
  Direction = (0,0,1)
  Length = 26
  Length2 = 10
  Profile = -> Sketch064
  ReferenceAxis = -> Sketch064 [N_Axis]
  Suppressed = false
  Type = 0
FEATURE [Sketcher::SketchObject] Sketch065
  ArcFitTolerance = 1e-06
  AttachmentSupport = -> [Pad021]
  FullyConstrained = false
  MakeInternals = false
  MapMode = 5
  Placement = pos=(51,0,0) rot=(0.57735,0.57735,0.57735;2.0944rad)
  sketch-geometry (8):
    g0: LineSegment [constr] StartX=-105.942 StartY=6 StartZ=0 EndX=159.863 EndY=6 EndZ=0
    g1: LineSegment [constr] StartX=-56.6 StartY=54.0105 StartZ=0 EndX=-56.6 EndY=-51.0272 EndZ=0
    g2: LineSegment [constr] StartX=45 StartY=52.761 StartZ=0 EndX=45 EndY=-27.7374 EndZ=0
    g3: LineSegment [constr] StartX=3.4 StartY=51.9731 StartZ=0 EndX=3.4 EndY=-32.6534 EndZ=0
    g4: Circle CenterX=45 CenterY=6 CenterZ=0 NormalX=0 NormalY=0 NormalZ=1 AngleXU=0 Radius=2
    g5: Circle CenterX=3.4 CenterY=6 CenterZ=0 NormalX=0 NormalY=0 NormalZ=1 AngleXU=0 Radius=2
    g6: Circle CenterX=-56.6 CenterY=6 CenterZ=0 NormalX=0 NormalY=0 NormalZ=1 AngleXU=0 Radius=2
    g7: LineSegment [constr] StartX=73 StartY=47.2374 StartZ=0 EndX=73 EndY=-20.359 EndZ=0
  constraints (19):
    c: Horizontal(g0)
    c: Distance(g0,g-1) = 6
    c: Vertical(g1)
    c: Vertical(g2)
    c: Vertical(g3)
    c: PointOnObject(g4,g0)
    c: PointOnObject(g5,g0)
    c: PointOnObject(g6,g0)
    c: Diameter(g5) = 4
    c: Equal(g4,g6)
    c: Equal(g6,g5)
    c: PointOnObject(g4,g2)
    c: PointOnObject(g5,g3)
    c: PointOnObject(g6,g1)
    c: Distance(g2,g3) = 41.6
    c: Distance(g1,g3) = 60
    c: Vertical(g7)
    c: DistanceX(g-1,g7) = 73
    c: DistanceX(g2,g7) = 28
FEATURE [PartDesign::Pocket] Pocket043
  BaseFeature = -> Pad021
  Direction = (-1,0,0)
  Length = 5
  Length2 = 5
  Profile = -> Sketch065
  ReferenceAxis = -> Sketch065 [N_Axis]
  Suppressed = false
  Type = 1
FEATURE [PartDesign::Chamfer] Chamfer003
  Angle = 45
  Base = -> Pocket043 [Face3,Face4]
  BaseFeature = -> Pocket043
  ChamferType = 0
  FlipDirection = false
  Size = 2
  Size2 = 1
  SupportTransform = false
  Suppressed = false
  UseAllEdges = false
FEATURE [PartDesign::Body] Body017  label="HDD2"
  AllowCompound = false
  Group = -> [Sketch064,Pad021,Sketch065,Pocket043,Chamfer003]
  Origin = -> Origin017
  Placement = pos=(63.5,58.4,40.5) rot=(0,0,1;3.14159rad)
  Tip = -> Chamfer003
FEATURE [Sketcher::SketchObject] Sketch066
  ArcFitTolerance = 1e-06
  AttachmentSupport = -> [XZ_Plane018]
  FullyConstrained = false
  MakeInternals = false
  MapMode = 5
  Placement = pos=(0,0,0) rot=(1,0,0;1.5708rad)
  sketch-geometry (31):
    g0: LineSegment StartX=4 StartY=0 StartZ=0 EndX=-125.536 EndY=0 EndZ=0
    g1: LineSegment StartX=-125.536 StartY=0 StartZ=0 EndX=-125.536 EndY=-1.01 EndZ=0
    g2: LineSegment StartX=-125.536 StartY=-1.01 StartZ=0 EndX=-128.536 EndY=-1.01 EndZ=0
    g3: LineSegment StartX=-128.536 StartY=-1.01 StartZ=0 EndX=-128.536 EndY=0 EndZ=0
    g4: LineSegment StartX=-128.536 StartY=0 StartZ=0 EndX=-141.92 EndY=0 EndZ=0
    g5: LineSegment StartX=-141.92 StartY=0 StartZ=0 EndX=-141.92 EndY=-3.3955 EndZ=0
    g6: LineSegment StartX=-141.92 StartY=-3.3955 StartZ=0 EndX=-147.92 EndY=-3.3955 EndZ=0
    g7: LineSegment StartX=-147.92 StartY=-3.3955 StartZ=0 EndX=-147.92 EndY=3.2 EndZ=0
    g8: LineSegment StartX=-147.92 StartY=3.2 StartZ=0 EndX=-124.257 EndY=3.2 EndZ=0
    g9: LineSegment StartX=-124.257 StartY=3.2 StartZ=0 EndX=-124.257 EndY=8.8 EndZ=0
    g10: LineSegment StartX=-124.257 StartY=8.8 StartZ=0 EndX=-147.92 EndY=8.8 EndZ=0
    g11: LineSegment StartX=-147.92 StartY=8.8 StartZ=0 EndX=-147.92 EndY=16.6996 EndZ=0
    g12: LineSegment StartX=-147.92 StartY=16.6996 StartZ=0 EndX=-141.92 EndY=16.6996 EndZ=0
    g13: LineSegment StartX=-141.92 StartY=16.6996 StartZ=0 EndX=-141.92 EndY=12 EndZ=0
    g14: LineSegment StartX=-141.92 StartY=12 StartZ=0 EndX=-128.536 EndY=12 EndZ=0
    g15: LineSegment StartX=-128.536 StartY=12 StartZ=0 EndX=-128.536 EndY=13.01 EndZ=0
    g16: LineSegment StartX=-128.536 StartY=13.01 StartZ=0 EndX=-125.536 EndY=13.01 EndZ=0
    g17: LineSegment StartX=-125.536 StartY=13.01 StartZ=0 EndX=-125.536 EndY=12 EndZ=0
    g18: LineSegment StartX=-125.536 StartY=12 StartZ=0 EndX=4 EndY=12 EndZ=0
    g19: LineSegment StartX=4 StartY=12 StartZ=0 EndX=4 EndY=0 EndZ=0
    g20: LineSegment [constr] StartX=-177.942 StartY=12 StartZ=0 EndX=14.5003 EndY=12 EndZ=0
    g21: LineSegment [constr] StartX=-125.536 StartY=27.4193 StartZ=0 EndX=-125.536 EndY=-18.7719 EndZ=0
    g22: LineSegment [constr] StartX=-141.92 StartY=22.481 StartZ=0 EndX=-141.92 EndY=-16.4674 EndZ=0
    g23: LineSegment [constr] StartX=-147.92 StartY=19.6726 StartZ=0 EndX=-147.92 EndY=-22.0842 EndZ=0
    g24: Circle CenterX=-66 CenterY=6 CenterZ=0 NormalX=0 NormalY=0 NormalZ=1 AngleXU=0 Radius=1.9
    g25: Circle CenterX=-6 CenterY=6 CenterZ=0 NormalX=0 NormalY=0 NormalZ=1 AngleXU=0 Radius=1.9
    g26: LineSegment [constr] StartX=-174.191 StartY=6 StartZ=0 EndX=-2.85094 EndY=6 EndZ=0
    g27: Circle CenterX=-107.6 CenterY=6 CenterZ=0 NormalX=0 NormalY=0 NormalZ=1 AngleXU=0 Radius=1.9
    g28: Circle CenterX=-17.6 CenterY=6 CenterZ=0 NormalX=0 NormalY=0 NormalZ=1 AngleXU=0 Radius=1.9
    g29: Circle CenterX=-59.2 CenterY=6 CenterZ=0 NormalX=0 NormalY=0 NormalZ=1 AngleXU=0 Radius=1.9
    g30: Circle CenterX=-119.3 CenterY=6 CenterZ=0 NormalX=0 NormalY=0 NormalZ=1 AngleXU=0 Radius=1.9
  constraints (86):
    c: PointOnObject(g0,g-1)
    c: Coincident(g0,g1)
    c: Coincident(g1,g2)
    c: Coincident(g2,g3)
    c: PointOnObject(g3,g-1)
    c: Coincident(g3,g4)
    c: Horizontal(g4)
    c: Coincident(g4,g5)
    c: Coincident(g5,g6)
    c: Coincident(g6,g7)
    c: Coincident(g7,g8)
    c: Horizontal(g8)
    c: Coincident(g8,g9)
    c: Coincident(g9,g10)
    c: Horizontal(g10)
    c: Coincident(g10,g11)
    c: Coincident(g11,g12)
    c: Coincident(g12,g13)
    c: Coincident(g13,g14)
    c: Horizontal(g14)
    c: Coincident(g14,g15)
    c: Coincident(g15,g16)
    c: Horizontal(g16)
    c: Coincident(g16,g17)
    c: Coincident(g17,g18)
    c: Horizontal(g18)
    c: Coincident(g18,g19)
    c: Coincident(g19,g0)
    c: Vertical(g7)
    c: Vertical(g11)
    c: Horizontal(g12)
    c: Horizontal(g6)
    c: Horizontal(g20)
    c: PointOnObject(g17,g20)
    c: PointOnObject(g14,g20)
    c: DistanceY(g0,g20) = 12
    c: Vertical(g15)
    c: Vertical(g17)
    c: Vertical(g1)
    c: Vertical(g3)
    c: Horizontal(g2)
    c: Vertical(g21)
    c: PointOnObject(g0,g21)
    c: PointOnObject(g17,g21)
    c: DistanceX(g16,g16) = 3
    c: DistanceY(g15,g15) = 1.01
    c: DistanceX(g2,g2) = 3
    c: DistanceY(g3,g3) = 1.01
    c: Vertical(g13)
    c: Vertical(g5)
    c: Vertical(g22)
    c: Vertical(g23)
    c: PointOnObject(g7,g23)
    c: PointOnObject(g10,g23)
    c: PointOnObject(g13,g22)
    c: PointOnObject(g4,g22)
    c: DistanceX(g12,g12) = 6
    c: Vertical(g9)
    c: Distance(g8,g-1) = 3.2
    c: Distance(g9,g20) = 3.2
    c: Diameter(g24) = 3.8
    c: Diameter(g25) = 3.8
    c: Horizontal(g26)
    c: PointOnObject(g24,g26)
    c: PointOnObject(g25,g26)
    c: DistanceY(g0,g26) = 6
    c: DistanceX(g24,g25) = 60
    c: PointOnObject(g27,g26)
    c: Diameter(g27) = 3.8
    c: DistanceX(g27,g25) = 101.6
    c: DistanceX(g25,g0) = 10
    c: Horizontal(g0)
    c: Vertical(g19)
    c: Distance(g-1,g0) = 4
    c: DistanceX(g27,g24) = 41.6
    c: DistanceX(g24,g25) = 60
    c: DistanceX(g9,g27) = 16.6574
    c: PointOnObject(g28,g26)
    c: PointOnObject(g29,g26)
    c: DistanceX(g29,g28) = 41.6
    c: Equal(g24,g29)
    c: Equal(g29,g28)
    c: DistanceX(g28,g25) = 11.6
    c: PointOnObject(g30,g26)
    c: Equal(g27,g30)
    c: DistanceX(g30,g27) = 11.7
FEATURE [PartDesign::Pad] Pad022
  Direction = (0,-1,2e-16)
  Length = 4
  Length2 = 6
  Placement = pos=(0,0,0) rot=(1,0,0;1.5708rad)
  Profile = -> Sketch066
  ReferenceAxis = -> Sketch066 [N_Axis]
  Suppressed = false
  Type = 0
FEATURE [Sketcher::SketchObject] Sketch067
  ArcFitTolerance = 1e-06
  AttachmentSupport = -> [Pad022]
  FullyConstrained = false
  MakeInternals = false
  MapMode = 5
  Placement = pos=(0,1.4e-15,0) rot=(-1,0,0;1.5708rad)
  sketch-geometry (11):
    g0: LineSegment [constr] StartX=-161.488 StartY=-6 StartZ=0 EndX=29.2523 EndY=-6 EndZ=0
    g1: Circle CenterX=-107.6 CenterY=-6 CenterZ=0 NormalX=0 NormalY=0 NormalZ=1 AngleXU=0 Radius=4
    g2: Circle CenterX=-6 CenterY=-6 CenterZ=0 NormalX=0 NormalY=0 NormalZ=1 AngleXU=0 Radius=4
    g3: Circle CenterX=-17.6 CenterY=-6 CenterZ=0 NormalX=0 NormalY=0 NormalZ=1 AngleXU=0 Radius=4
    g4: LineSegment [constr] StartX=-59.2 StartY=-24.7493 StartZ=0 EndX=-59.2 EndY=6.79496 EndZ=0
    g5: LineSegment [constr] StartX=-66 StartY=5.43194 StartZ=0 EndX=-66 EndY=-19.7353 EndZ=0
    g6: ArcOfCircle CenterX=-66.118 CenterY=-6 CenterZ=0 NormalX=0 NormalY=0 NormalZ=1 AngleXU=0 Radius=4 StartAngle=1.5708 EndAngle=4.71239
    g7: ArcOfCircle CenterX=-59.2 CenterY=-6 CenterZ=0 NormalX=0 NormalY=0 NormalZ=1 AngleXU=0 Radius=4 StartAngle=4.71239 EndAngle=7.85398
    g8: LineSegment StartX=-66.118 StartY=-2 StartZ=0 EndX=-59.2 EndY=-2 EndZ=0
    g9: LineSegment StartX=-66.118 StartY=-10 StartZ=0 EndX=-59.2 EndY=-10 EndZ=0
    g10: Circle CenterX=-119.3 CenterY=-6 CenterZ=0 NormalX=0 NormalY=0 NormalZ=1 AngleXU=0 Radius=4
  constraints (26):
    c: Horizontal(g0)
    c: Distance(g-1,g0) = 6
    c: PointOnObject(g1,g0)
    c: PointOnObject(g2,g0)
    c: DistanceX(g2,g-1) = 6
    c: DistanceX(g1,g2) = 101.6
    c: Diameter(g1) = 8
    c: Equal(g2,g1)
    c: PointOnObject(g3,g0)
    c: DistanceX(g3,g-1) = 17.6
    c: Vertical(g4)
    c: Vertical(g5)
    c: Distance(g3,g4) = 41.6
    c: Distance(g2,g5) = 60
    c: Tangent(g6,g8) = 1.5708
    c: Tangent(g6,g9) = -1.5708
    c: Tangent(g7,g8) = 1.5708
    c: Tangent(g7,g9) = -1.5708
    c: Equal(g6,g7)
    c: Symmetric(g0,g0,g6)
    c: PointOnObject(g7,g4)
    c: PointOnObject(g7,g0)
    c: Distance(g9,g8) = 8
    c: PointOnObject(g10,g0)
    c: DistanceX(g10,g1) = 11.7
    c: Equal(g10,g1)
FEATURE [PartDesign::Pocket] Pocket044
  BaseFeature = -> Pad022
  Direction = (0,-1,-2e-16)
  Length = 2.5
  Length2 = 5
  Placement = pos=(0,0,0) rot=(1,0,0;1.5708rad)
  Profile = -> Sketch067
  ReferenceAxis = -> Sketch067 [N_Axis]
  Suppressed = false
  Type = 0
FEATURE [PartDesign::Fillet] Fillet018
  Base = -> Pocket044 [Edge5,Edge1]
  BaseFeature = -> Pocket044
  Placement = pos=(0,0,0) rot=(1,0,0;1.5708rad)
  Radius = 2
  SupportTransform = false
  Suppressed = false
  UseAllEdges = false
FEATURE [PartDesign::Fillet] Fillet019
  Base = -> Fillet018 [Face7,Face14]
  BaseFeature = -> Fillet018
  Placement = pos=(0,0,0) rot=(1,0,0;1.5708rad)
  Radius = 1
  SupportTransform = false
  Suppressed = false
  UseAllEdges = false
FEATURE [PartDesign::Fillet] Fillet020
  Base = -> Fillet019 [Edge76,Edge74,Edge70,Edge56,Edge52,Edge48]
  BaseFeature = -> Fillet019
  Placement = pos=(0,0,0) rot=(1,0,0;1.5708rad)
  Radius = 2
  SupportTransform = false
  Suppressed = false
  UseAllEdges = false
FEATURE [PartDesign::Body] Body018  label="side_V2_002"
  AllowCompound = false
  Group = -> [Sketch066,Pad022,Sketch067,Pocket044,Fillet018,Fillet019,Fillet020]
  Origin = -> Origin018
  Placement = pos=(8.5,121,72.8) rot=(0,0,-1;4.71239rad)
  Tip = -> Fillet020
FEATURE [Sketcher::SketchObject] Sketch068
  ArcFitTolerance = 1e-06
  AttachmentSupport = -> [XY_Plane019]
  FullyConstrained = true
  MakeInternals = false
  MapMode = 5
  sketch-geometry (6):
    g0: LineSegment StartX=-51 StartY=73 StartZ=0 EndX=-51 EndY=-73 EndZ=0
    g1: LineSegment StartX=-51 StartY=-73 StartZ=0 EndX=51 EndY=-73 EndZ=0
    g2: LineSegment StartX=51 StartY=-73 StartZ=0 EndX=51 EndY=73 EndZ=0
    g3: LineSegment StartX=51 StartY=73 StartZ=0 EndX=-51 EndY=73 EndZ=0
    g4: LineSegment [constr] StartX=-51 StartY=73 StartZ=0 EndX=51 EndY=-73 EndZ=0
    g5: LineSegment [constr] StartX=51 StartY=73 StartZ=0 EndX=-51 EndY=-73 EndZ=0
  constraints (16):
    c: Coincident(g0,g1)
    c: Coincident(g1,g2)
    c: Coincident(g2,g3)
    c: Coincident(g3,g0)
    c: Vertical(g0)
    c: Vertical(g2)
    c: Horizontal(g1)
    c: Horizontal(g3)
    c: Coincident(g4,g0)
    c: Coincident(g4,g1)
    c: Coincident(g5,g2)
    c: Coincident(g5,g0)
    c: PointOnObject(g-1,g4)
    c: PointOnObject(g-1,g5)
    c: DistanceY(g0,g0) = 146
    c: DistanceX(g1,g1) = 102
FEATURE [PartDesign::Pad] Pad023
  Direction = (0,0,1)
  Length = 26
  Length2 = 10
  Profile = -> Sketch068
  ReferenceAxis = -> Sketch068 [N_Axis]
  Suppressed = false
  Type = 0
FEATURE [Sketcher::SketchObject] Sketch069
  ArcFitTolerance = 1e-06
  AttachmentSupport = -> [Pad023]
  FullyConstrained = false
  MakeInternals = false
  MapMode = 5
  Placement = pos=(51,0,0) rot=(0.57735,0.57735,0.57735;2.0944rad)
  sketch-geometry (8):
    g0: LineSegment [constr] StartX=-105.942 StartY=6 StartZ=0 EndX=159.863 EndY=6 EndZ=0
    g1: LineSegment [constr] StartX=-56.6 StartY=54.0105 StartZ=0 EndX=-56.6 EndY=-51.0272 EndZ=0
    g2: LineSegment [constr] StartX=45 StartY=52.761 StartZ=0 EndX=45 EndY=-27.7374 EndZ=0
    g3: LineSegment [constr] StartX=3.4 StartY=51.9731 StartZ=0 EndX=3.4 EndY=-32.6534 EndZ=0
    g4: Circle CenterX=45 CenterY=6 CenterZ=0 NormalX=0 NormalY=0 NormalZ=1 AngleXU=0 Radius=2
    g5: Circle CenterX=3.4 CenterY=6 CenterZ=0 NormalX=0 NormalY=0 NormalZ=1 AngleXU=0 Radius=2
    g6: Circle CenterX=-56.6 CenterY=6 CenterZ=0 NormalX=0 NormalY=0 NormalZ=1 AngleXU=0 Radius=2
    g7: LineSegment [constr] StartX=73 StartY=47.2374 StartZ=0 EndX=73 EndY=-20.359 EndZ=0
  constraints (19):
    c: Horizontal(g0)
    c: Distance(g0,g-1) = 6
    c: Vertical(g1)
    c: Vertical(g2)
    c: Vertical(g3)
    c: PointOnObject(g4,g0)
    c: PointOnObject(g5,g0)
    c: PointOnObject(g6,g0)
    c: Diameter(g5) = 4
    c: Equal(g4,g6)
    c: Equal(g6,g5)
    c: PointOnObject(g4,g2)
    c: PointOnObject(g5,g3)
    c: PointOnObject(g6,g1)
    c: Distance(g2,g3) = 41.6
    c: Distance(g1,g3) = 60
    c: Vertical(g7)
    c: DistanceX(g-1,g7) = 73
    c: DistanceX(g2,g7) = 28
FEATURE [PartDesign::Pocket] Pocket045
  BaseFeature = -> Pad023
  Direction = (-1,0,0)
  Length = 5
  Length2 = 5
  Profile = -> Sketch069
  ReferenceAxis = -> Sketch069 [N_Axis]
  Suppressed = false
  Type = 1
FEATURE [PartDesign::Chamfer] Chamfer004
  Angle = 45
  Base = -> Pocket045 [Face3,Face4]
  BaseFeature = -> Pocket045
  ChamferType = 0
  FlipDirection = false
  Size = 2
  Size2 = 1
  SupportTransform = false
  Suppressed = false
  UseAllEdges = false
FEATURE [PartDesign::Body] Body019  label="HDD3"
  AllowCompound = false
  Group = -> [Sketch068,Pad023,Sketch069,Pocket045,Chamfer004]
  Origin = -> Origin019
  Placement = pos=(63.5,58.4,72.8) rot=(0,0,1;3.14159rad)
  Tip = -> Chamfer004
FEATURE [PartDesign::Chamfer] Chamfer005
  Angle = 45
  Base = -> Pocket038 [Face3,Face4]
  BaseFeature = -> Pocket038
  ChamferType = 0
  FlipDirection = false
  Size = 1
  Size2 = 1
  SupportTransform = false
  Suppressed = false
  UseAllEdges = false
FEATURE [PartDesign::Body] Body014  label="SSD1"
  AllowCompound = false
  Group = -> [Sketch056,Pad018,Sketch057,Pocket038,Chamfer005]
  Origin = -> Origin014
  Placement = pos=(63.5,55.3,40.5) rot=(0,0,1;3.14159rad)
  Tip = -> Chamfer005
FEATURE [Sketcher::SketchObject] Sketch070
  ArcFitTolerance = 1e-06
  AttachmentSupport = -> [XY_Plane020]
  FullyConstrained = true
  MakeInternals = false
  MapMode = 5
  sketch-geometry (6):
    g0: LineSegment StartX=-35 StartY=50 StartZ=0 EndX=-35 EndY=-50 EndZ=0
    g1: LineSegment StartX=-35 StartY=-50 StartZ=0 EndX=35 EndY=-50 EndZ=0
    g2: LineSegment StartX=35 StartY=-50 StartZ=0 EndX=35 EndY=50 EndZ=0
    g3: LineSegment StartX=35 StartY=50 StartZ=0 EndX=-35 EndY=50 EndZ=0
    g4: LineSegment [constr] StartX=-35 StartY=50 StartZ=0 EndX=35 EndY=-50 EndZ=0
    g5: LineSegment [constr] StartX=35 StartY=50 StartZ=0 EndX=-35 EndY=-50 EndZ=0
  constraints (16):
    c: Coincident(g0,g1)
    c: Coincident(g1,g2)
    c: Coincident(g2,g3)
    c: Coincident(g3,g0)
    c: Vertical(g0)
    c: Vertical(g2)
    c: Horizontal(g1)
    c: Horizontal(g3)
    c: Coincident(g4,g0)
    c: Coincident(g4,g1)
    c: Coincident(g5,g2)
    c: Coincident(g5,g0)
    c: PointOnObject(g-1,g4)
    c: PointOnObject(g-1,g5)
    c: DistanceY(g0,g0) = 100
    c: DistanceX(g1,g1) = 70
FEATURE [PartDesign::Pad] Pad024
  Direction = (0,0,1)
  Length = 10
  Length2 = 10
  Profile = -> Sketch070
  ReferenceAxis = -> Sketch070 [N_Axis]
  Suppressed = false
  Type = 0
FEATURE [Sketcher::SketchObject] Sketch071
  ArcFitTolerance = 1e-06
  AttachmentSupport = -> [Pad024]
  FullyConstrained = false
  MakeInternals = false
  MapMode = 5
  Placement = pos=(35,0,0) rot=(0.57735,0.57735,0.57735;2.0944rad)
  sketch-geometry (6):
    g0: LineSegment [constr] StartX=-63.1237 StartY=3 StartZ=0 EndX=159.863 EndY=3 EndZ=0
    g1: LineSegment [constr] StartX=36 StartY=18.9953 StartZ=0 EndX=36 EndY=-27.7374 EndZ=0
    g2: LineSegment [constr] StartX=-41 StartY=50.9008 StartZ=0 EndX=-41 EndY=-33.7257 EndZ=0
    g3: Circle CenterX=36 CenterY=3 CenterZ=0 NormalX=0 NormalY=0 NormalZ=1 AngleXU=0 Radius=1.5
    g4: Circle CenterX=-41 CenterY=3 CenterZ=0 NormalX=0 NormalY=0 NormalZ=1 AngleXU=0 Radius=1.5
    g5: LineSegment [constr] StartX=50 StartY=21.3406 StartZ=0 EndX=50 EndY=-20.359 EndZ=0
  constraints (14):
    c: Horizontal(g0)
    c: Distance(g0,g-1) = 3
    c: Vertical(g1)
    c: Vertical(g2)
    c: PointOnObject(g3,g0)
    c: PointOnObject(g4,g0)
    c: Diameter(g4) = 3
    c: PointOnObject(g3,g1)
    c: PointOnObject(g4,g2)
    c: Vertical(g5)
    c: DistanceX(g-1,g5) = 50
    c: DistanceX(g1,g5) = 14
    c: DistanceX(g2,g1) = 77
    c: Equal(g3,g4)
FEATURE [PartDesign::Pocket] Pocket046
  BaseFeature = -> Pad024
  Direction = (-1,0,0)
  Length = 5
  Length2 = 5
  Profile = -> Sketch071
  ReferenceAxis = -> Sketch071 [N_Axis]
  Suppressed = false
  Type = 1
FEATURE [PartDesign::Chamfer] Chamfer006
  Angle = 45
  Base = -> Pocket046 [Face3,Face4]
  BaseFeature = -> Pocket046
  ChamferType = 0
  FlipDirection = false
  Size = 1
  Size2 = 1
  SupportTransform = false
  Suppressed = false
  UseAllEdges = false
FEATURE [PartDesign::Body] Body020  label="SSD2"
  AllowCompound = false
  Group = -> [Sketch070,Pad024,Sketch071,Pocket046,Chamfer006]
  Origin = -> Origin020
  Placement = pos=(63.5,55.3,56.5) rot=(0,0,1;3.14159rad)
  Tip = -> Chamfer006
FEATURE [App::DocumentObjectGroup] Group002  label="Placeholders"
  Group = -> [Body016,Body018,Body010,Body017,Body019,Body011,Body014,Body020]
FEATURE [Sketcher::SketchObject] Sketch077
  ArcFitTolerance = 1e-06
  AttachmentSupport = -> [XZ_Plane022]
  FullyConstrained = false
  MakeInternals = false
  MapMode = 5
  Placement = pos=(0,0,0) rot=(1,0,0;1.5708rad)
  sketch-geometry (7):
    g0: LineSegment StartX=4 StartY=0 StartZ=0 EndX=-140 EndY=0 EndZ=0
    g1: LineSegment StartX=-140 StartY=12 StartZ=0 EndX=4 EndY=12 EndZ=0
    g2: LineSegment StartX=4 StartY=12 StartZ=0 EndX=4 EndY=0 EndZ=0
    g3: LineSegment [constr] StartX=-177.942 StartY=12 StartZ=0 EndX=14.5003 EndY=12 EndZ=0
    g4: LineSegment [constr] StartX=-174.191 StartY=6 StartZ=0 EndX=-2.85094 EndY=6 EndZ=0
    g5: LineSegment StartX=-140 StartY=12 StartZ=0 EndX=-140 EndY=0 EndZ=0
    g6: LineSegment [constr] StartX=-136 StartY=22.5308 StartZ=0 EndX=-136 EndY=-12.2751 EndZ=0
  constraints (18):
    c: PointOnObject(g0,g-1)
    c: Horizontal(g1)
    c: Coincident(g1,g2)
    c: Coincident(g2,g0)
    c: Horizontal(g3)
    c: PointOnObject(g1,g3)
    c: DistanceY(g0,g3) = 12
    c: Horizontal(g4)
    c: DistanceY(g0,g4) = 6
    c: Horizontal(g0)
    c: Vertical(g2)
    c: Distance(g-1,g0) = 4
    c: Coincident(g5,g1)
    c: Coincident(g5,g0)
    c: Vertical(g5)
    c: Vertical(g6)
    c: DistanceX(g6,g-1) = 136
    c: DistanceX(g0,g6) = 4
FEATURE [PartDesign::Pad] Pad029
  Direction = (0,-1,2e-16)
  Length = 4
  Length2 = 6
  Placement = pos=(0,0,0) rot=(1,0,0;1.5708rad)
  Profile = -> Sketch077
  ReferenceAxis = -> Sketch077 [N_Axis]
  Suppressed = false
  Type = 0
FEATURE [Sketcher::SketchObject] Sketch078
  ArcFitTolerance = 1e-06
  FullyConstrained = false
  MakeInternals = false
  MapMode = 5
  Placement = pos=(-140,0,0) rot=(0.707107,0,-0.707107;3.14159rad)
  sketch-geometry (7):
    g0: LineSegment StartX=-23 StartY=-5 StartZ=0 EndX=0 EndY=-5 EndZ=0
    g1: LineSegment StartX=0 StartY=-5 StartZ=0 EndX=0 EndY=4 EndZ=0
    g2: LineSegment StartX=0 StartY=4 StartZ=0 EndX=-23 EndY=4 EndZ=0
    g3: LineSegment StartX=-23 StartY=4 StartZ=0 EndX=-23 EndY=-5 EndZ=0
    g4: LineSegment [constr] StartX=-17 StartY=-10.6055 StartZ=0 EndX=-17 EndY=17.4989 EndZ=0
    g5: LineSegment [constr] StartX=-29.9685 StartY=-0.5 StartZ=0 EndX=11.0625 EndY=-0.5 EndZ=0
    g6: Circle CenterX=-17 CenterY=-0.5 CenterZ=0 NormalX=0 NormalY=0 NormalZ=1 AngleXU=0 Radius=1.75
  constraints (19):
    c: Coincident(g0,g1)
    c: Coincident(g1,g2)
    c: Coincident(g2,g3)
    c: Coincident(g3,g0)
    c: Horizontal(g0)
    c: Horizontal(g2)
    c: Vertical(g1)
    c: Vertical(g3)
    c: PointOnObject(g1,g-2)
    c: DistanceY(g-1,g1) = 4
    c: Distance(g0,g-1) = 5
    c: DistanceX(g0,g0) = 23
    c: Vertical(g4)
    c: Horizontal(g5)
    c: DistanceY(g5,g-1) = 0.5
    c: DistanceX(g4,g-1) = 17
    c: PointOnObject(g6,g4)
    c: PointOnObject(g6,g5)
    c: Diameter(g6) = 3.5
FEATURE [PartDesign::Pad] Pad030
  BaseFeature = -> Pad029
  Direction = (-1,-1e-16,-2e-16)
  Length = 4
  Length2 = 10
  Placement = pos=(0,0,0) rot=(1,0,0;1.5708rad)
  Profile = -> Sketch078
  ReferenceAxis = -> Sketch078 [N_Axis]
  Reversed = true
  Suppressed = false
  Type = 0
FEATURE [PartDesign::Pad] Pad031
  BaseFeature = -> Pad030
  Direction = (0,-1,0)
  Length = 16
  Length2 = 10
  Placement = pos=(0,0,0) rot=(1,0,0;1.5708rad)
  Profile = -> Pad030 [Face4]
  Suppressed = false
  Type = 0
FEATURE [PartDesign::Chamfer] Chamfer011
  Angle = 45
  Base = -> Pad031 [Edge3]
  BaseFeature = -> Pad031
  ChamferType = 0
  FlipDirection = false
  Placement = pos=(0,0,0) rot=(1,0,0;1.5708rad)
  Size = 3
  Size2 = 1
  SupportTransform = false
  Suppressed = false
  UseAllEdges = false
FEATURE [PartDesign::Chamfer] Chamfer012
  Angle = 45
  Base = -> Chamfer011 [Edge27]
  BaseFeature = -> Chamfer011
  ChamferType = 0
  FlipDirection = false
  Placement = pos=(0,0,0) rot=(1,0,0;1.5708rad)
  Size = 12
  Size2 = 1
  SupportTransform = false
  Suppressed = false
  UseAllEdges = false
FEATURE [PartDesign::Chamfer] Chamfer013
  Angle = 45
  Base = -> Chamfer012 [Edge15]
  BaseFeature = -> Chamfer012
  ChamferType = 0
  FlipDirection = false
  Placement = pos=(0,0,0) rot=(1,0,0;1.5708rad)
  Size = 15
  Size2 = 1
  SupportTransform = false
  Suppressed = false
  UseAllEdges = false
FEATURE [Sketcher::SketchObject] Sketch079
  ArcFitTolerance = 1e-06
  AttachmentSupport = -> [Chamfer013]
  FullyConstrained = false
  MakeInternals = false
  MapMode = 5
  Placement = pos=(0,2.6e-15,12) rot=(0,0,1;3.14159rad)
  sketch-geometry (9):
    g0: LineSegment StartX=15 StartY=20 StartZ=0 EndX=15 EndY=12 EndZ=0
    g1: LineSegment StartX=15 StartY=12 StartZ=0 EndX=33 EndY=12 EndZ=0
    g2: LineSegment StartX=33 StartY=12 StartZ=0 EndX=33 EndY=20 EndZ=0
    g3: LineSegment StartX=33 StartY=20 StartZ=0 EndX=15 EndY=20 EndZ=0
    g4: LineSegment StartX=92 StartY=20 StartZ=0 EndX=92 EndY=12 EndZ=0
    g5: LineSegment StartX=92 StartY=12 StartZ=0 EndX=110 EndY=12 EndZ=0
    g6: LineSegment StartX=110 StartY=12 StartZ=0 EndX=110 EndY=20 EndZ=0
    g7: LineSegment StartX=110 StartY=20 StartZ=0 EndX=92 EndY=20 EndZ=0
    g8: LineSegment [constr] StartX=-27.5433 StartY=12 StartZ=0 EndX=142.785 EndY=12 EndZ=0
  constraints (26):
    c: Coincident(g0,g1)
    c: Coincident(g1,g2)
    c: Coincident(g2,g3)
    c: Coincident(g3,g0)
    c: Vertical(g0)
    c: Vertical(g2)
    c: Horizontal(g1)
    c: Horizontal(g3)
    c: Coincident(g4,g5)
    c: Coincident(g5,g6)
    c: Coincident(g6,g7)
    c: Coincident(g7,g4)
    c: Vertical(g4)
    c: Vertical(g6)
    c: Horizontal(g5)
    c: Horizontal(g7)
    c: Horizontal(g8)
    c: PointOnObject(g4,g1)
    c: PointOnObject(g1,g8)
    c: DistanceY(g6,g6) = 8
    c: DistanceY(g2,g2) = 8
    c: DistanceX(g1,g1) = 18
    c: DistanceX(g5,g5) = 18
    c: DistanceY(g-1,g8) = 12
    c: Distance(g0,g-2) = 15
    c: DistanceX(g1,g4) = 59
FEATURE [PartDesign::Pad] Pad032
  BaseFeature = -> Chamfer013
  Direction = (0,0,1)
  Length = 14
  Length2 = 10
  Placement = pos=(0,0,0) rot=(1,0,0;1.5708rad)
  Profile = -> Sketch079
  ReferenceAxis = -> Sketch079 [N_Axis]
  Suppressed = false
  Type = 0
FEATURE [PartDesign::Chamfer] Chamfer014
  Angle = 45
  Base = -> Pad032 [Edge62,Edge65,Edge67,Edge70]
  BaseFeature = -> Pad032
  ChamferType = 0
  FlipDirection = false
  Placement = pos=(0,0,0) rot=(1,0,0;1.5708rad)
  Size = 5
  Size2 = 1
  SupportTransform = false
  Suppressed = false
  UseAllEdges = false
FEATURE [Sketcher::SketchObject] Sketch080
  ArcFitTolerance = 1e-06
  AttachmentSupport = -> [Chamfer014]
  FullyConstrained = false
  MakeInternals = false
  MapMode = 5
  Placement = pos=(0,1.3e-15,0) rot=(-1,0,0;1.5708rad)
  sketch-geometry (9):
    g0: LineSegment [constr] StartX=-24.5466 StartY=-56.5173 StartZ=0 EndX=-24.5466 EndY=15.372 EndZ=0
    g1: LineSegment [constr] StartX=-101.547 StartY=-58.8423 StartZ=0 EndX=-101.547 EndY=15.2073 EndZ=0
    g2: LineSegment [constr] StartX=8.4852 StartY=-19 StartZ=0 EndX=-144.415 EndY=-19 EndZ=0
    g3: LineSegment [constr] StartX=13.359 StartY=-4 StartZ=0 EndX=-158.263 EndY=-4 EndZ=0
    g4: Circle CenterX=-24.5466 CenterY=-19 CenterZ=0 NormalX=0 NormalY=0 NormalZ=1 AngleXU=0 Radius=1.75
    g5: Circle CenterX=-101.547 CenterY=-19 CenterZ=0 NormalX=0 NormalY=0 NormalZ=1 AngleXU=0 Radius=1.75
    g6: Circle CenterX=-101.547 CenterY=-4 CenterZ=0 NormalX=0 NormalY=0 NormalZ=1 AngleXU=0 Radius=1.75
    g7: Circle CenterX=-24.5466 CenterY=-4 CenterZ=0 NormalX=0 NormalY=0 NormalZ=1 AngleXU=0 Radius=1.75
    g8: LineSegment [constr] StartX=-115.547 StartY=25.1943 StartZ=0 EndX=-115.547 EndY=-44.0546 EndZ=0
  constraints (21):
    c: Vertical(g1)
    c: Vertical(g0)
    c: Horizontal(g2)
    c: Horizontal(g3)
    c: PointOnObject(g4,g0)
    c: PointOnObject(g5,g1)
    c: PointOnObject(g6,g1)
    c: PointOnObject(g7,g0)
    c: Diameter(g7) = 3.5
    c: Equal(g7,g4)
    c: Equal(g7,g5)
    c: Equal(g5,g6)
    c: PointOnObject(g7,g3)
    c: PointOnObject(g4,g2)
    c: PointOnObject(g6,g3)
    c: PointOnObject(g5,g2)
    c: DistanceX(g5,g4) = 77
    c: DistanceY(g3,g-1) = 4
    c: DistanceY(g2,g-1) = 19
    c: Vertical(g8)
    c: DistanceX(g8,g1) = 14
FEATURE [PartDesign::Pocket] Pocket048
  BaseFeature = -> Chamfer014
  Direction = (0,-1,-2e-16)
  Length = 5
  Length2 = 5
  Placement = pos=(0,0,0) rot=(1,0,0;1.5708rad)
  Profile = -> Sketch080
  ReferenceAxis = -> Sketch080 [N_Axis]
  Suppressed = false
  Type = 1
FEATURE [PartDesign::Fillet] Fillet022
  Base = -> Pocket048 [Edge35,Edge64,Edge78,Edge42]
  BaseFeature = -> Pocket048
  Placement = pos=(0,0,0) rot=(1,0,0;1.5708rad)
  Radius = 3
  SupportTransform = false
  Suppressed = false
  UseAllEdges = false
FEATURE [Sketcher::SketchObject] Sketch081
  ArcFitTolerance = 1e-06
  FullyConstrained = false
  MakeInternals = false
  MapMode = 5
  Placement = pos=(0,0,0) rot=(1,0,0;3.14159rad)
  sketch-geometry (3):
    g0: LineSegment [constr] StartX=22 StartY=38.772 StartZ=0 EndX=22 EndY=-26.6365 EndZ=0
    g1: LineSegment [constr] StartX=-7.13446 StartY=7.5 StartZ=0 EndX=106.04 EndY=7.5 EndZ=0
    g2: Circle CenterX=22 CenterY=7.5 CenterZ=0 NormalX=0 NormalY=0 NormalZ=1 AngleXU=0 Radius=1.9
  constraints (7):
    c: Vertical(g0)
    c: DistanceX(g-1,g0) = 22
    c: Horizontal(g1)
    c: DistanceY(g-1,g1) = 7.5
    c: PointOnObject(g2,g1)
    c: PointOnObject(g2,g0)
    c: Diameter(g2) = 3.8
FEATURE [PartDesign::Pocket] Pocket049
  BaseFeature = -> Hole007
  Direction = (0,0,1)
  Length = 5
  Length2 = 5
  Placement = pos=(0,0,0) rot=(1,0,0;1.5708rad)
  Profile = -> Sketch081
  ReferenceAxis = -> Sketch081 [N_Axis]
  Suppressed = false
  Type = 1
FEATURE [PartDesign::Body] Body015  label="FrontV2"
  AllowCompound = false
  Group = -> [Sketch058,Pad019,Sketch059,Pocket039,Sketch060,Pocket040,Hole007,Sketch081,Pocket049]
  Origin = -> Origin015
  Placement = pos=(4,0,0) rot=(0,0,1;0rad)
  Tip = -> Pocket049
FEATURE [PartDesign::Hole] Hole009
  BaseFeature = -> Fillet022
  CustomThreadClearance = 0
  Depth = 9
  DepthType = 0
  Diameter = 6.5
  DrillForDepth = false
  DrillPoint = 0
  DrillPointAngle = 118
  HoleCutCountersinkAngle = 90
  HoleCutCustomValues = false
  HoleCutDepth = 0
  HoleCutDiameter = 0
  HoleCutType = 0
  ModelThread = false
  Placement = pos=(0,0,0) rot=(1,0,0;1.5708rad)
  Profile = -> Fillet022 [Edge66,Edge67]
  Suppressed = false
  Tapered = false
  TaperedAngle = 90
  ThreadClass = 0
  ThreadDepth = 9
  ThreadDepthType = 0
  ThreadDirection = 0
  ThreadFit = 0
  ThreadSize = 0
  ThreadType = 0
  Threaded = false
  UseCustomThreadClearance = false
FEATURE [PartDesign::Hole] Hole011
  BaseFeature = -> Hole009
  CustomThreadClearance = 0
  Depth = 3
  DepthType = 0
  Diameter = 6.5
  DrillForDepth = false
  DrillPoint = 0
  DrillPointAngle = 118
  HoleCutCountersinkAngle = 90
  HoleCutCustomValues = false
  HoleCutDepth = 0
  HoleCutDiameter = 0
  HoleCutType = 0
  ModelThread = false
  Placement = pos=(0,0,0) rot=(1,0,0;1.5708rad)
  Profile = -> Hole009 [Edge57,Edge47]
  Suppressed = false
  Tapered = false
  TaperedAngle = 90
  ThreadClass = 0
  ThreadDepth = 3
  ThreadDepthType = 0
  ThreadDirection = 0
  ThreadFit = 0
  ThreadSize = 0
  ThreadType = 0
  Threaded = false
  UseCustomThreadClearance = false
FEATURE [Sketcher::SketchObject] Sketch082
  ArcFitTolerance = 1e-06
  AttachmentSupport = -> [Hole011]
  FullyConstrained = false
  MakeInternals = false
  MapMode = 5
  Placement = pos=(0,2.6e-15,12) rot=(0,0,1;3.14159rad)
  sketch-geometry (10):
    g0: LineSegment StartX=36.5178 StartY=17 StartZ=0 EndX=88.6422 EndY=17 EndZ=0
    g1: LineSegment StartX=88.6422 StartY=17 StartZ=0 EndX=88.6422 EndY=9 EndZ=0
    g2: LineSegment StartX=88.6422 StartY=9 StartZ=0 EndX=117.232 EndY=9 EndZ=0
    g3: LineSegment StartX=117.232 StartY=3 StartZ=0 EndX=11.9868 EndY=3 EndZ=0
    g4: LineSegment StartX=11.9868 StartY=9 StartZ=0 EndX=36.5178 EndY=9 EndZ=0
    g5: LineSegment StartX=36.5178 StartY=9 StartZ=0 EndX=36.5178 EndY=17 EndZ=0
    g6: LineSegment [constr] StartX=-10.9114 StartY=9 StartZ=0 EndX=142.263 EndY=9 EndZ=0
    g7: LineSegment [constr] StartX=0.791969 StartY=20 StartZ=0 EndX=135.705 EndY=20 EndZ=0
    g8: LineSegment StartX=11.9868 StartY=9 StartZ=0 EndX=11.9868 EndY=3 EndZ=0
    g9: LineSegment StartX=117.232 StartY=9 StartZ=0 EndX=117.232 EndY=3 EndZ=0
  constraints (24):
    c: Horizontal(g0)
    c: Coincident(g0,g1)
    c: Vertical(g1)
    c: Coincident(g1,g2)
    c: Horizontal(g2)
    c: Horizontal(g3)
    c: Horizontal(g4)
    c: Coincident(g4,g5)
    c: Coincident(g5,g0)
    c: Vertical(g5)
    c: Horizontal(g6)
    c: PointOnObject(g1,g6)
    c: PointOnObject(g4,g6)
    c: Horizontal(g7)
    c: DistanceY(g-1,g7) = 20
    c: DistanceY(g0,g7) = 3
    c: Coincident(g8,g4)
    c: Coincident(g8,g3)
    c: DistanceY(g-1,g3) = 3
    c: DistanceY(g-1,g6) = 9
    c: Vertical(g8)
    c: Coincident(g9,g2)
    c: Coincident(g9,g3)
    c: Vertical(g9)
FEATURE [PartDesign::Pocket] Pocket050
  BaseFeature = -> Hole011
  Direction = (0,0,-1)
  Length = 9
  Length2 = 5
  Placement = pos=(0,0,0) rot=(1,0,0;1.5708rad)
  Profile = -> Sketch082
  ReferenceAxis = -> Sketch082 [N_Axis]
  Suppressed = false
  Type = 0
FEATURE [PartDesign::Body] Body022  label="ssdSideV2_SA001"
  AllowCompound = false
  Group = -> [Sketch077,Pad029,Sketch078,Pad030,Pad031,Chamfer011,Chamfer012,Chamfer013,Sketch079,Pad032,Chamfer014,Sketch080,Pocket048,Fillet022,Hole009,Hole011,Sketch082,Pocket050]
  Origin = -> Origin022
  Placement = pos=(8.5,121,40.5) rot=(0,0,-1;4.71239rad)
  Tip = -> Pocket050
FEATURE [Part::Mirroring] Mirror  label="ssdSideV2_SA001 (mirrored)"
  Base = (-29.825,53,53.5)
  Normal = (-1,0,-1.19209e-07)
  Placement = pos=(186.5,0,0) rot=(0,0,1;0rad)
  Source = -> Body022
FEATURE [Sketcher::SketchObject] Sketch050
  ArcFitTolerance = 1e-06
  AttachmentSupport = -> [XZ_Plane012]
  FullyConstrained = false
  MakeInternals = false
  MapMode = 5
  Placement = pos=(0,0,0) rot=(1,0,0;1.5708rad)
  sketch-geometry (13):
    g0: LineSegment StartX=4 StartY=0 StartZ=0 EndX=-140 EndY=0 EndZ=0
    g1: LineSegment StartX=-140 StartY=12 StartZ=0 EndX=4 EndY=12 EndZ=0
    g2: LineSegment StartX=4 StartY=12 StartZ=0 EndX=4 EndY=0 EndZ=0
    g3: LineSegment [constr] StartX=-177.942 StartY=12 StartZ=0 EndX=14.5003 EndY=12 EndZ=0
    g4: Circle CenterX=-66 CenterY=6 CenterZ=0 NormalX=0 NormalY=0 NormalZ=1 AngleXU=0 Radius=1.9
    g5: Circle CenterX=-6 CenterY=6 CenterZ=0 NormalX=0 NormalY=0 NormalZ=1 AngleXU=0 Radius=1.9
    g6: LineSegment [constr] StartX=-174.191 StartY=6 StartZ=0 EndX=-2.85094 EndY=6 EndZ=0
    g7: Circle CenterX=-107.6 CenterY=6 CenterZ=0 NormalX=0 NormalY=0 NormalZ=1 AngleXU=0 Radius=1.9
    g8: Circle CenterX=-30.4 CenterY=6 CenterZ=0 NormalX=0 NormalY=0 NormalZ=1 AngleXU=0 Radius=1.9
    g9: Circle CenterX=-72 CenterY=6 CenterZ=0 NormalX=0 NormalY=0 NormalZ=1 AngleXU=0 Radius=1.9
    g10: Circle CenterX=-132 CenterY=6 CenterZ=0 NormalX=0 NormalY=0 NormalZ=1 AngleXU=0 Radius=1.9
    g11: LineSegment StartX=-140 StartY=12 StartZ=0 EndX=-140 EndY=0 EndZ=0
    g12: LineSegment [constr] StartX=-136 StartY=22.5308 StartZ=0 EndX=-136 EndY=-12.2751 EndZ=0
  constraints (37):
    c: PointOnObject(g0,g-1)
    c: Horizontal(g1)
    c: Coincident(g1,g2)
    c: Coincident(g2,g0)
    c: Horizontal(g3)
    c: PointOnObject(g1,g3)
    c: DistanceY(g0,g3) = 12
    c: Diameter(g4) = 3.8
    c: Diameter(g5) = 3.8
    c: Horizontal(g6)
    c: PointOnObject(g4,g6)
    c: PointOnObject(g5,g6)
    c: DistanceY(g0,g6) = 6
    c: PointOnObject(g7,g6)
    c: Diameter(g7) = 3.8
    c: DistanceX(g5,g0) = 10
    c: Horizontal(g0)
    c: Vertical(g2)
    c: Distance(g-1,g0) = 4
    c: PointOnObject(g8,g6)
    c: PointOnObject(g9,g6)
    c: Equal(g4,g9)
    c: Equal(g9,g8)
    c: PointOnObject(g10,g6)
    c: Equal(g7,g10)
    c: Coincident(g11,g1)
    c: Coincident(g11,g0)
    c: Vertical(g11)
    c: Vertical(g12)
    c: DistanceX(g12,g-1) = 136
    c: DistanceX(g0,g12) = 4
    c: DistanceX(g9,g8) = 41.6
    c: DistanceX(g10,g9) = 60
    c: DistanceX(g4,g5) = 60
    c: DistanceX(g7,g4) = 41.6
    c: DistanceX(g5,g-1) = 6
    c: DistanceX(g9,g4) = 6
FEATURE [PartDesign::Pad] Pad014
  Direction = (0,-1,2e-16)
  Length = 4
  Length2 = 6
  Placement = pos=(0,0,0) rot=(1,0,0;1.5708rad)
  Profile = -> Sketch050
  ReferenceAxis = -> Sketch050 [N_Axis]
  Suppressed = false
  Type = 0
FEATURE [Sketcher::SketchObject] Sketch051
  ArcFitTolerance = 1e-06
  AttachmentSupport = -> [Pad014]
  FullyConstrained = false
  MakeInternals = false
  MapMode = 5
  Placement = pos=(0,1.3e-15,0) rot=(-1,0,0;1.5708rad)
  sketch-geometry (11):
    g0: LineSegment [constr] StartX=-171.476 StartY=-6 StartZ=0 EndX=27.4761 EndY=-6 EndZ=0
    g1: Circle CenterX=-107.6 CenterY=-6 CenterZ=0 NormalX=0 NormalY=0 NormalZ=1 AngleXU=0 Radius=4
    g2: Circle CenterX=-6 CenterY=-6 CenterZ=0 NormalX=0 NormalY=0 NormalZ=1 AngleXU=0 Radius=4
    g3: Circle CenterX=-30.4 CenterY=-6 CenterZ=0 NormalX=0 NormalY=0 NormalZ=1 AngleXU=0 Radius=4
    g4: LineSegment [constr] StartX=-66 StartY=-25.1807 StartZ=0 EndX=-66 EndY=6.36355 EndZ=0
    g5: LineSegment [constr] StartX=-72 StartY=5.4978 StartZ=0 EndX=-72 EndY=-19.6694 EndZ=0
    g6: ArcOfCircle CenterX=-72 CenterY=-6 CenterZ=0 NormalX=0 NormalY=0 NormalZ=1 AngleXU=0 Radius=4 StartAngle=1.5708 EndAngle=4.71239
    g7: ArcOfCircle CenterX=-66 CenterY=-6 CenterZ=0 NormalX=0 NormalY=0 NormalZ=1 AngleXU=0 Radius=4 StartAngle=4.71239 EndAngle=7.85398
    g8: LineSegment StartX=-72 StartY=-2 StartZ=0 EndX=-66 EndY=-2 EndZ=0
    g9: LineSegment StartX=-72 StartY=-10 StartZ=0 EndX=-66 EndY=-10 EndZ=0
    g10: Circle CenterX=-132 CenterY=-6 CenterZ=0 NormalX=0 NormalY=0 NormalZ=1 AngleXU=0 Radius=4
  constraints (28):
    c: Horizontal(g0)
    c: Distance(g-1,g0) = 6
    c: PointOnObject(g1,g0)
    c: PointOnObject(g2,g0)
    c: DistanceX(g2,g-1) = 6
    c: Diameter(g1) = 8
    c: Equal(g2,g1)
    c: PointOnObject(g3,g0)
    c: Vertical(g4)
    c: Vertical(g5)
    c: Tangent(g6,g8) = 1.5708
    c: Tangent(g6,g9) = -1.5708
    c: Tangent(g7,g8) = 1.5708
    c: Tangent(g7,g9) = -1.5708
    c: Equal(g6,g7)
    c: Symmetric(g0,g0,g6)
    c: PointOnObject(g7,g4)
    c: PointOnObject(g7,g0)
    c: Distance(g9,g8) = 8
    c: PointOnObject(g10,g0)
    c: Equal(g10,g1)
    c: Equal(g2,g3)
    c: PointOnObject(g6,g5)
    c: DistanceX(g4,g2) = 60
    c: DistanceX(g1,g4) = 41.6
    c: DistanceX(g5,g3) = 41.6
    c: DistanceX(g10,g5) = 60
    c: DistanceX(g5,g4) = 6
FEATURE [PartDesign::Pocket] Pocket036
  BaseFeature = -> Pad014
  Direction = (0,-1,-2e-16)
  Length = 2.5
  Length2 = 5
  Placement = pos=(0,0,0) rot=(1,0,0;1.5708rad)
  Profile = -> Sketch051
  ReferenceAxis = -> Sketch051 [N_Axis]
  Suppressed = false
  Type = 0
FEATURE [PartDesign::Fillet] Fillet012
  Base = -> Pocket036 [Edge2,Edge8]
  BaseFeature = -> Pocket036
  Placement = pos=(0,0,0) rot=(1,0,0;1.5708rad)
  Radius = 3
  SupportTransform = false
  Suppressed = false
  UseAllEdges = false
FEATURE [Sketcher::SketchObject] Sketch052
  ArcFitTolerance = 1e-06
  AttachmentSupport = -> [Fillet012]
  FullyConstrained = false
  MakeInternals = false
  MapMode = 5
  Placement = pos=(-140,0,0) rot=(0.707107,0,-0.707107;3.14159rad)
  sketch-geometry (7):
    g0: LineSegment StartX=-23 StartY=-5 StartZ=0 EndX=0 EndY=-5 EndZ=0
    g1: LineSegment StartX=0 StartY=-5 StartZ=0 EndX=0 EndY=4 EndZ=0
    g2: LineSegment StartX=0 StartY=4 StartZ=0 EndX=-23 EndY=4 EndZ=0
    g3: LineSegment StartX=-23 StartY=4 StartZ=0 EndX=-23 EndY=-5 EndZ=0
    g4: LineSegment [constr] StartX=-17 StartY=-10.6055 StartZ=0 EndX=-17 EndY=17.4989 EndZ=0
    g5: LineSegment [constr] StartX=-29.9685 StartY=-0.5 StartZ=0 EndX=11.0625 EndY=-0.5 EndZ=0
    g6: Circle CenterX=-17 CenterY=-0.5 CenterZ=0 NormalX=0 NormalY=0 NormalZ=1 AngleXU=0 Radius=1.75
  constraints (19):
    c: Coincident(g0,g1)
    c: Coincident(g1,g2)
    c: Coincident(g2,g3)
    c: Coincident(g3,g0)
    c: Horizontal(g0)
    c: Horizontal(g2)
    c: Vertical(g1)
    c: Vertical(g3)
    c: PointOnObject(g1,g-2)
    c: DistanceY(g-1,g1) = 4
    c: Distance(g0,g-1) = 5
    c: DistanceX(g0,g0) = 23
    c: Vertical(g4)
    c: Horizontal(g5)
    c: DistanceY(g5,g-1) = 0.5
    c: DistanceX(g4,g-1) = 17
    c: PointOnObject(g6,g4)
    c: PointOnObject(g6,g5)
    c: Diameter(g6) = 3.5
FEATURE [PartDesign::Pad] Pad015
  BaseFeature = -> Fillet012
  Direction = (-1,0,-2e-16)
  Length = 4
  Length2 = 10
  Placement = pos=(0,0,0) rot=(1,0,0;1.5708rad)
  Profile = -> Sketch052
  ReferenceAxis = -> Sketch052 [N_Axis]
  Reversed = true
  Suppressed = false
  Type = 0
FEATURE [PartDesign::Body] Body012  label="hhdSideV2"
  AllowCompound = false
  Group = -> [Sketch050,Pad014,Sketch051,Pocket036,Fillet012,Sketch052,Pad015]
  Origin = -> Origin012
  Placement = pos=(8.5,121,8) rot=(0,0,-1;4.71239rad)
  Tip = -> Pad015
FEATURE [Part::Mirroring] Mirror001  label="hhdSideV2(mirrored)"
  Base = (3.19269,78.5248,0)
  Normal = (-0.999953,0,0)
  Placement = pos=(120.8,0,0) rot=(0,0,1;0rad)
  Source = -> Body012
FEATURE [App::DocumentObjectGroup] Group001  label="V2"
  Group = -> [Body005,Body006,Body007,Body015,Body012,Mirror001,Mirror]
